FCSTD DOCUMENT  (FreeCAD 0.19R)
Label: frame
License: All rights reserved
LicenseURL: http://en.wikipedia.org/wiki/All_rights_reserved
objects: Part::Cylinder×360, Part::MultiFuse×254, Part::Box×222, Part::Cut×205, Part::Feature×133, Part::Chamfer×65, Part::Fillet×41, Part::Extrusion×23, Part::Cone×16, Part::Mirroring×12, App::DocumentObjectGroup×8, Part::RegularPolygon×4, Mesh::Feature×1, Part::Compound×1
note: 1336 computed .brp shape members not serialized (recipe doc carries the construction recipe); baked Part::Feature solids carry a one-line shape summary decoded from their .brp

FEATURE [Part::Box] Box  label="Cube"
  AttacherType = Attacher::AttachEngine3D
  Height = 1
  Length = 430
  Placement = pos=(65,-96,36) rot=(0,0,1;0rad)
  Width = 176
FEATURE [Part::Box] Box001  label="FLOOR"
  AttacherType = Attacher::AttachEngine3D
  Height = 2
  Length = 1568
  Placement = pos=(-800,-101,-32) rot=(0,0,1;0rad)
  Width = 186
FEATURE [Mesh::Feature] truck  label="TRUCK"
  Placement = pos=(-684,-93,62) rot=(0,0,1;0rad)
FEATURE [Part::Box] Box002  label="Cube002"
  AttacherType = Attacher::AttachEngine3D
  Height = 10
  Length = 430
  Placement = pos=(65,-5,25) rot=(0,0,1;0rad)
  Width = 10
FEATURE [Part::Box] Box003  label="Cube003"
  AttacherType = Attacher::AttachEngine3D
  Height = 10
  Length = 430
  Placement = pos=(65,-65,25) rot=(0,0,1;0rad)
  Width = 10
FEATURE [Part::MultiFuse] Fusion  label="Fusion-006"
  Placement = pos=(0,22,0) rot=(0,0,1;0rad)
  Refine = true
  Shapes = -> [Box003,Box002]
FEATURE [Part::Box] Box006  label="Cube006"
  AttacherType = Attacher::AttachEngine3D
  Height = 1
  Length = 55
  Placement = pos=(495,-96,36) rot=(0,1,0;0.314159rad)
  Width = 176
FEATURE [Part::Feature] Fusion001005002004004005002010002003003003001  label="axle_001"
  shape: bbox 59.64 x 183 x 59.64 mm, 5134 faces, 2 solids (baked)
FEATURE [Part::Feature] Fusion001005002004004005002010002003003003002  label="axle_002"
  Placement = pos=(274,0,0) rot=(0,0,1;0rad)
  shape: bbox 59.64 x 183 x 59.64 mm, 5134 faces, 2 solids (baked)
FEATURE [Part::Feature] Fusion001005002004004005002010002003003003003  label="axle_003"
  Placement = pos=(360,0,0) rot=(0,0,1;0rad)
  shape: bbox 59.64 x 183 x 59.64 mm, 5134 faces, 2 solids (baked)
FEATURE [Part::Feature] Fusion001005002004004005002010002003003003004  label="axle_004"
  Placement = pos=(446,0,0) rot=(0,0,1;0rad)
  shape: bbox 59.64 x 183 x 59.64 mm, 5134 faces, 2 solids (baked)
FEATURE [Part::MultiFuse] Fusion001005002004004005002010002003003003005  label="flat"
  Refine = true
  Shapes = -> [Box006,Box]
FEATURE [Part::Cylinder] Cylinder661  label="Cylinder736"
  Angle = 360
  AttacherType = Attacher::AttachEngine3D
  Height = 128
  Placement = pos=(0,-72,-1) rot=(-1,0,0;1.5708rad)
  Radius = 6
FEATURE [Part::Cylinder] Cylinder663  label="Cylinder738"
  Angle = 360
  AttacherType = Attacher::AttachEngine3D
  Height = 166
  Placement = pos=(0,-91,-1) rot=(-1,0,0;1.5708rad)
  Radius = 2.7
FEATURE [Part::Cylinder] Cylinder666  label="Cylinder741"
  Angle = 360
  AttacherType = Attacher::AttachEngine3D
  Height = 12
  Placement = pos=(4,-50,-7) rot=(0,0,1;0rad)
  Radius = 0.75
FEATURE [Part::Cylinder] Cylinder667  label="Cylinder742"
  Angle = 360
  AttacherType = Attacher::AttachEngine3D
  Height = 12
  Placement = pos=(-4,-50,-7) rot=(0,0,1;0rad)
  Radius = 0.75
FEATURE [Part::MultiFuse] Fusion001005002004004005002010002003003003017005  label="Fusion-019"
  Placement = pos=(0,-15,0) rot=(0,0,1;0rad)
  Refine = true
  Shapes = -> [Cylinder666,Cylinder667]
FEATURE [Part::Cylinder] Cylinder668  label="Cylinder743"
  Angle = 360
  AttacherType = Attacher::AttachEngine3D
  Height = 6
  Placement = pos=(4,-50,-7) rot=(0,0,1;0rad)
  Radius = 1.1
FEATURE [Part::Cylinder] Cylinder669  label="Cylinder744"
  Angle = 360
  AttacherType = Attacher::AttachEngine3D
  Height = 6
  Placement = pos=(-4,-50,-7) rot=(0,0,1;0rad)
  Radius = 1.1
FEATURE [Part::MultiFuse] Fusion001005002004004005002010002003003003017006  label="Fusion-020"
  Placement = pos=(0,-15,0) rot=(0,0,1;0rad)
  Refine = true
  Shapes = -> [Cylinder668,Cylinder669]
FEATURE [Part::Box] Box015  label="Cube015"
  AttacherType = Attacher::AttachEngine3D
  Height = 12
  Length = 12
  Placement = pos=(-6,47,-7) rot=(0,0,1;0rad)
  Width = 4
FEATURE [Part::Box] Box016  label="Cube016"
  AttacherType = Attacher::AttachEngine3D
  Height = 12
  Length = 12
  Placement = pos=(-6,-10,-7) rot=(0,0,1;0rad)
  Width = 4
FEATURE [Part::Box] Box018  label="Cube018"
  AttacherType = Attacher::AttachEngine3D
  Height = 12
  Length = 12
  Placement = pos=(-6,-67,-7) rot=(0,0,1;0rad)
  Width = 4
FEATURE [Part::MultiFuse] Fusion001005002004004005002010002003003003017007  label="Fusion-016"
  Refine = true
  Shapes = -> [Fusion001005002004004005002010002003003003017005,Fusion001005002004004005002010002003003003017006]
FEATURE [Part::Feature] Fusion001005002004004005002010002003003003017007001  label="Fusion-018"
  Placement = pos=(0,57,0) rot=(0,0,1;0rad)
  shape: bbox 10.2 x 2.2 x 12 mm, 10 faces, 2 solids (baked)
FEATURE [Part::Feature] Fusion001005002004004005002010002003003003017007002  label="Fusion-017"
  Placement = pos=(0,114,0) rot=(0,0,1;0rad)
  shape: bbox 10.2 x 2.2 x 12 mm, 10 faces, 2 solids (baked)
FEATURE [Part::Cylinder] Cylinder670  label="Cylinder745"
  Angle = 360
  AttacherType = Attacher::AttachEngine3D
  Height = 12
  Placement = pos=(4,-50,-7) rot=(0,0,1;0rad)
  Radius = 0.75
FEATURE [Part::Cylinder] Cylinder671  label="Cylinder746"
  Angle = 360
  AttacherType = Attacher::AttachEngine3D
  Height = 6
  Placement = pos=(4,-50,-1) rot=(0,0,1;0rad)
  Radius = 1.1
FEATURE [Part::MultiFuse] Fusion001005002004004005002010002003003003017007003  label="Fusion-003"
  Placement = pos=(-4,42,0) rot=(0,0,1;0rad)
  Refine = true
  Shapes = -> [Cylinder670,Cylinder671]
FEATURE [Part::MultiFuse] Fusion001005002004004005002010002003003003017007005  label="Fusion-015"
  Refine = true
  Shapes = -> [Fusion001005002004004005002010002003003003017007,Fusion001005002004004005002010002003003003017007002,Fusion001005002004004005002010002003003003017007001]
FEATURE [Part::Box] Box019  label="Cube019"
  AttacherType = Attacher::AttachEngine3D
  Height = 7
  Length = 16
  Placement = pos=(-8,-72,-8) rot=(0,0,1;0rad)
  Width = 128
FEATURE [Part::Box] Box020  label="Cube020"
  AttacherType = Attacher::AttachEngine3D
  Height = 6
  Length = 16
  Placement = pos=(-8,-72,-1) rot=(0,0,1;0rad)
  Width = 128
FEATURE [Part::Cylinder] Cylinder672  label="Cylinder747"
  Angle = 360
  AttacherType = Attacher::AttachEngine3D
  Height = 8
  Placement = pos=(0,-8,28) rot=(0,0,1;0rad)
  Radius = 35
FEATURE [Part::Box] Box024  label="Cube024"
  AttacherType = Attacher::AttachEngine3D
  Height = 10
  Length = 50
  Placement = pos=(65,-46,25) rot=(0,0,1;0rad)
  Width = 25
FEATURE [Part::Feature] Face001
  shape: bbox 59.35 x 2e-07 x 37.17 mm, 1 faces, 0 solids (baked)
FEATURE [Part::Extrusion] Extrude
  Base = -> Face001
  Dir = (0,1,0)
  DirMode = 0
  FaceMakerClass = Part::FaceMakerBullseye
  LengthFwd = 35
  LengthRev = 0
  Placement = pos=(0,-10,0) rot=(0,0,1;0rad)
  Solid = true
  Symmetric = false
FEATURE [Part::MultiFuse] Fusion001005002004004005002010002003003003017007007  label="Fusion-001"
  Placement = pos=(0,13,0) rot=(0,0,1;0rad)
  Refine = true
  Shapes = -> [Box024,Extrude]
FEATURE [Part::Box] Box025  label="Cube025"
  AttacherType = Attacher::AttachEngine3D
  Height = 15
  Length = 430
  Placement = pos=(65,-101,22) rot=(0,0,1;0rad)
  Width = 5
FEATURE [Part::Cylinder] Cylinder673  label="Cylinder748"
  Angle = 360
  AttacherType = Attacher::AttachEngine3D
  Height = 5
  Placement = pos=(280,-101,1) rot=(-1,0,0;1.5708rad)
  Radius = 34
FEATURE [Part::Cylinder] Cylinder674  label="Cylinder749"
  Angle = 360
  AttacherType = Attacher::AttachEngine3D
  Height = 5
  Placement = pos=(365,-101,1) rot=(-1,0,0;1.5708rad)
  Radius = 34
FEATURE [Part::Cylinder] Cylinder675  label="Cylinder750"
  Angle = 360
  AttacherType = Attacher::AttachEngine3D
  Height = 5
  Placement = pos=(451,-101,1) rot=(-1,0,0;1.5708rad)
  Radius = 34
FEATURE [Part::MultiFuse] Fusion001005002004004005002010002003003003017007008  label="Fusion-000"
  Placement = pos=(-5,0,0) rot=(0,0,1;0rad)
  Refine = true
  Shapes = -> [Cylinder675,Cylinder674,Cylinder673]
FEATURE [Part::Cut] Cut012004
  Base = -> Box025
  Refine = true
  Tool = -> Fusion001005002004004005002010002003003003017007008
FEATURE [Part::Cylinder] Cylinder676  label="Cylinder751"
  Angle = 360
  AttacherType = Attacher::AttachEngine3D
  Height = 1
  Placement = pos=(365,-101,1) rot=(-1,0,0;1.5708rad)
  Radius = 35
FEATURE [Part::Cylinder] Cylinder677  label="Cylinder752"
  Angle = 360
  AttacherType = Attacher::AttachEngine3D
  Height = 1
  Placement = pos=(280,-101,1) rot=(-1,0,0;1.5708rad)
  Radius = 35
FEATURE [Part::Cylinder] Cylinder678  label="Cylinder753"
  Angle = 360
  AttacherType = Attacher::AttachEngine3D
  Height = 1
  Placement = pos=(451,-101,1) rot=(-1,0,0;1.5708rad)
  Radius = 35
FEATURE [Part::MultiFuse] Fusion001005002004004005002010002003003003017007009  label="Fusion-007"
  Placement = pos=(-5,0,0) rot=(0,0,1;0rad)
  Refine = true
  Shapes = -> [Cylinder678,Cylinder676,Cylinder677]
FEATURE [Part::Box] Box026  label="Cube026"
  AttacherType = Attacher::AttachEngine3D
  Height = 13
  Length = 430
  Placement = pos=(65,-101,23) rot=(0,0,1;0rad)
  Width = 1
FEATURE [Part::Cut] Cut012005
  Base = -> Box026
  Refine = true
  Tool = -> Fusion001005002004004005002010002003003003017007009
FEATURE [Part::Cut] Cut012006
  Base = -> Cut012004
  Refine = true
  Tool = -> Cut012005
FEATURE [Part::Feature] Face002
  shape: bbox 80.83 x 2e-07 x 47.48 mm, 1 faces, 0 solids (baked)
FEATURE [Part::Feature] Face003
  shape: bbox 84.57 x 2e-07 x 55.62 mm, 1 faces, 0 solids (baked)
FEATURE [Part::Extrusion] Extrude002
  Base = -> Face002
  Dir = (0,1,0)
  DirMode = 0
  FaceMakerClass = Part::FaceMakerBullseye
  LengthFwd = 1
  LengthRev = 0
  Solid = true
  Symmetric = false
FEATURE [Part::Extrusion] Extrude003
  Base = -> Face003
  Dir = (0,1,0)
  DirMode = 0
  FaceMakerClass = Part::FaceMakerBullseye
  LengthFwd = 5
  LengthRev = 0
  Solid = true
  Symmetric = false
FEATURE [Part::Cut] Cut012012
  Base = -> Extrude003
  Refine = true
  Tool = -> Extrude002
FEATURE [Part::Box] Box027  label="Cube027"
  AttacherType = Attacher::AttachEngine3D
  Height = 15
  Length = 49.5
  Placement = pos=(-35,-66,37) rot=(0,0,-1;0.785398rad)
  Width = 5
FEATURE [Part::Box] Box028  label="Cube028"
  AttacherType = Attacher::AttachEngine3D
  Height = 15
  Length = 49.5
  Placement = pos=(-35,-66,37) rot=(0,0,-1;0.785398rad)
  Width = 5
FEATURE [Part::Mirroring] Part__Mirroring  label="Cube028 (Mirror #1)"
  Base = (0,0,0)
  Normal = (0,1,0)
  Placement = pos=(0,-16,0) rot=(0,0,1;0rad)
  Source = -> Box028
FEATURE [Part::Box] Box029  label="Cube029"
  AttacherType = Attacher::AttachEngine3D
  Height = 15
  Length = 5
  Placement = pos=(-35,-66,37) rot=(0,0,-1;0rad)
  Width = 116
FEATURE [Part::MultiFuse] Fusion001005002004004005002010002003003003017007010  label="Fusion-008"
  Placement = pos=(-5,0,0) rot=(0,0,1;0rad)
  Refine = true
  Shapes = -> [Box027,Part__Mirroring,Box029]
FEATURE [Part::Box] Box030  label="Cube030"
  AttacherType = Attacher::AttachEngine3D
  Height = 13
  Length = 49.5
  Placement = pos=(-35,-102,38) rot=(0,0,-1;0rad)
  Width = 2
FEATURE [Part::Box] Box031  label="Cube031"
  AttacherType = Attacher::AttachEngine3D
  Height = 13
  Length = 49.5
  Placement = pos=(-35,84,38) rot=(0,0,-1;0rad)
  Width = 1
FEATURE [Part::Cylinder] Cylinder679  label="Cylinder754"
  Angle = 46
  AttacherType = Attacher::AttachEngine3D
  Height = 7
  Placement = pos=(0,0,0) rot=(0,0,-1;1.97222rad)
  Radius = 109
FEATURE [Part::Cylinder] Cylinder680  label="Cylinder755"
  Angle = 32
  AttacherType = Attacher::AttachEngine3D
  Height = 7
  Placement = pos=(0,0,0) rot=(0,0,-1;1.85005rad)
  Radius = 109
FEATURE [Part::Cylinder] Cylinder681  label="Cylinder756"
  Angle = 41
  AttacherType = Attacher::AttachEngine3D
  Height = 7
  Placement = pos=(0,0,0) rot=(0,0,-1;1.90241rad)
  Radius = 108
FEATURE [Part::Cylinder] Cylinder682  label="Cylinder757"
  Angle = 26
  AttacherType = Attacher::AttachEngine3D
  Height = 7
  Placement = pos=(0,0,0) rot=(0,0,-1;1.79769rad)
  Radius = 110
FEATURE [Part::Cylinder] Cylinder686
  Angle = 360
  AttacherType = Attacher::AttachEngine3D
  Height = 7
  Placement = pos=(-34.1,-43,15.25) rot=(-1,0,0;1.5708rad)
  Radius = 3.5
FEATURE [Part::Box] Box035  label="Cube035"
  AttacherType = Attacher::AttachEngine3D
  Height = 4.3
  Length = 14
  Placement = pos=(-7,-43,-9) rot=(0,0,1;0rad)
  Width = 7
FEATURE [Part::Cylinder] Cylinder691  label="Cylinder762"
  Angle = 360
  AttacherType = Attacher::AttachEngine3D
  Height = 14
  Placement = pos=(-4.5,-50.5,-7) rot=(0,0,1;0rad)
  Radius = 1.25
FEATURE [Part::Cylinder] Cylinder692  label="Cylinder763"
  Angle = 360
  AttacherType = Attacher::AttachEngine3D
  Height = 14
  Placement = pos=(4.5,-50.5,-7) rot=(0,0,1;0rad)
  Radius = 1.25
FEATURE [Part::MultiFuse] Fusion001005002004004005002010002003003003017007017  label="Fusion-011"
  Placement = pos=(0,4,-3) rot=(0,0,1;0rad)
  Refine = true
  Shapes = -> [Cylinder692,Cylinder691]
FEATURE [Part::Cylinder] Cylinder693  label="Cylinder764"
  Angle = 46
  AttacherType = Attacher::AttachEngine3D
  Height = 7
  Placement = pos=(0,0,0) rot=(0,0,-1;1.97222rad)
  Radius = 108
FEATURE [Part::Cylinder] Cylinder694  label="Cylinder765"
  Angle = 46
  AttacherType = Attacher::AttachEngine3D
  Height = 7
  Placement = pos=(0,0,0) rot=(0,0,-1;1.97222rad)
  Radius = 107
FEATURE [Part::Cut] Cut012021
  Base = -> Cylinder682
  Placement = pos=(0,-1,0) rot=(0,0,1;0rad)
  Refine = true
  Tool = -> Cylinder679
FEATURE [Part::Cut] Cut012022
  Base = -> Cylinder680
  Placement = pos=(0,-0.5,0) rot=(0,0,1;0rad)
  Refine = true
  Tool = -> Cylinder693
FEATURE [Part::Cut] Cut012023
  Base = -> Cylinder681
  Refine = true
  Tool = -> Cylinder694
FEATURE [Part::MultiFuse] Fusion001005002004004005002010002003003003017007018  label="Fusion-012"
  Placement = pos=(0,-36,114) rot=(1,0,0;1.5708rad)
  Refine = true
  Shapes = -> [Cut012021,Cut012022,Cut012023]
FEATURE [Part::Cylinder] Cylinder695
  Angle = 360
  AttacherType = Attacher::AttachEngine3D
  Height = 7
  Placement = pos=(-34.1,-43,15.25) rot=(-1,0,0;1.5708rad)
  Radius = 1.5
FEATURE [Part::MultiFuse] Fusion001005002004004005002010002003003003017007019  label="Fusion-013"
  Refine = true
  Shapes = -> [Fusion001005002004004005002010002003003003017007018,Cylinder686]
FEATURE [Part::Cut] Cut012024
  Base = -> Fusion001005002004004005002010002003003003017007019
  Refine = true
  Tool = -> Cylinder695
FEATURE [Part::Fillet] Fillet001003
  Base = -> Cut012024
  Edges = 1 edges r=4: [Edge6]
  Placement = pos=(0,0,-12) rot=(0,0,1;0rad)
FEATURE [Part::MultiFuse] Fusion001005002004004005002010002003003003017007020  label="Fusion-014"
  Refine = true
  Shapes = -> [Box035,Fillet001003]
FEATURE [Part::Box] Box037  label="Cube037"
  AttacherType = Attacher::AttachEngine3D
  Height = 4.3
  Length = 15
  Placement = pos=(-7.5,-43.25,-9) rot=(0,0,1;0rad)
  Width = 7.5
FEATURE [Part::Box] Box038  label="Cube038"
  AttacherType = Attacher::AttachEngine3D
  Height = 1
  Length = 8.5
  Placement = pos=(-4.25,-43,-9) rot=(0,0,1;0rad)
  Width = 7
FEATURE [Part::Box] Box039  label="Cube039"
  AttacherType = Attacher::AttachEngine3D
  Height = 2
  Length = 2
  Placement = pos=(-6.25,-43,-10) rot=(0,0,1;0rad)
  Width = 7
FEATURE [Part::Box] Box040  label="Cube040"
  AttacherType = Attacher::AttachEngine3D
  Height = 2
  Length = 15
  Placement = pos=(-7.5,-49.5,-11) rot=(0,0,1;0rad)
  Width = 20
FEATURE [Part::Box] Box041  label="Cube041"
  AttacherType = Attacher::AttachEngine3D
  Height = 2
  Length = 15
  Placement = pos=(-7.5,-43.25,-11) rot=(0,0,1;0rad)
  Width = 7.5
FEATURE [Part::Cut] Cut012027
  Base = -> Box040
  Refine = true
  Tool = -> Box041
FEATURE [Part::Box] Box042  label="Cube042"
  AttacherType = Attacher::AttachEngine3D
  Height = 2
  Length = 8
  Placement = pos=(-4,-44,-11) rot=(0,0,1;0rad)
  Width = 9
FEATURE [Part::Fillet] Fillet001006
  Base = -> Cut012027
  Edges = 8 edges r=3: [Edge2,Edge4,Edge9,Edge12,Edge14,Edge16,Edge21,Edge24]
FEATURE [Part::MultiFuse] Fusion001005002004004005002010002003003003017007022  label="Fusion-022"
  Placement = pos=(0,0,1) rot=(0,0,1;0rad)
  Refine = true
  Shapes = -> [Box042,Fillet001006]
FEATURE [Part::Fillet] Fillet001007
  Base = -> Fusion001005002004004005002010002003003003017007020
  Edges = 10 edges r=1: [Edge5,Edge7,Edge20,Edge21,Edge32,Edge33,Edge73,Edge74,Edge84,Edge85]
FEATURE [Part::Cut] Cut012028
  Base = -> Fillet001007
  Refine = true
  Tool = -> Box038
FEATURE [Part::Box] Box043  label="Cube043"
  AttacherType = Attacher::AttachEngine3D
  Height = 2
  Length = 2
  Placement = pos=(4.25,-43,-10) rot=(0,0,1;0rad)
  Width = 7
FEATURE [Part::MultiFuse] Fusion001005002004004005002010002003003003017007023  label="Fusion-023"
  Refine = true
  Shapes = -> [Box039,Box043]
FEATURE [Part::Chamfer] Chamfer003
  Base = -> Fusion001005002004004005002010002003003003017007023
  Edges = 2 edges r=1: [Edge4,Edge20]
FEATURE [Part::MultiFuse] Fusion001005002004004005002010002003003003017007024  label="axle-leafspring-left_"
  Refine = true
  Shapes = -> [Cut012028,Chamfer003]
FEATURE [Part::Cylinder] Cylinder696  label="Cylinder766"
  Angle = 360
  AttacherType = Attacher::AttachEngine3D
  Height = 14
  Placement = pos=(-4.5,-50.5,-7) rot=(0,0,1;0rad)
  Radius = 1.25
FEATURE [Part::Cylinder] Cylinder697  label="Cylinder767"
  Angle = 360
  AttacherType = Attacher::AttachEngine3D
  Height = 14
  Placement = pos=(4.5,-50.5,-7) rot=(0,0,1;0rad)
  Radius = 1.25
FEATURE [Part::MultiFuse] Fusion001005002004004005002010002003003003017007024004  label="Fusion-028"
  Placement = pos=(0,18,-3) rot=(0,0,1;0rad)
  Refine = true
  Shapes = -> [Cylinder697,Cylinder696]
FEATURE [Part::Cylinder] Cylinder698  label="Cylinder768"
  Angle = 360
  AttacherType = Attacher::AttachEngine3D
  Height = 13
  Placement = pos=(-4.5,-50.5,-7) rot=(0,0,1;0rad)
  Radius = 3
FEATURE [Part::Cylinder] Cylinder699  label="Cylinder769"
  Angle = 360
  AttacherType = Attacher::AttachEngine3D
  Height = 13
  Placement = pos=(4.5,-50.5,-7) rot=(0,0,1;0rad)
  Radius = 3
FEATURE [Part::MultiFuse] Fusion001005002004004005002010002003003003017007024005  label="Fusion-029"
  Placement = pos=(0,4,-1) rot=(0,0,1;0rad)
  Refine = true
  Shapes = -> [Cylinder699,Cylinder698]
FEATURE [Part::Cylinder] Cylinder700  label="Cylinder770"
  Angle = 360
  AttacherType = Attacher::AttachEngine3D
  Height = 13
  Placement = pos=(4.5,-50.5,-7) rot=(0,0,1;0rad)
  Radius = 3
FEATURE [Part::Cylinder] Cylinder701  label="Cylinder771"
  Angle = 360
  AttacherType = Attacher::AttachEngine3D
  Height = 13
  Placement = pos=(-4.5,-50.5,-7) rot=(0,0,1;0rad)
  Radius = 3
FEATURE [Part::MultiFuse] Fusion001005002004004005002010002003003003017007024006  label="Fusion-030"
  Placement = pos=(0,18,-1) rot=(0,0,1;0rad)
  Refine = true
  Shapes = -> [Cylinder700,Cylinder701]
FEATURE [Part::MultiFuse] Fusion001005002004004005002010002003003003017007024007  label="Fusion-031"
  Refine = true
  Shapes = -> [Fusion001005002004004005002010002003003003017007024005,Fusion001005002004004005002010002003003003017007024006]
FEATURE [Part::MultiFuse] Fusion001005002004004005002010002003003003017007024008  label="Fusion-032"
  Refine = true
  Shapes = -> [Fusion001005002004004005002010002003003003017007024004,Fusion001005002004004005002010002003003003017007017]
FEATURE [Part::Cylinder] Cylinder702  label="Cylinder772"
  Angle = 360
  AttacherType = Attacher::AttachEngine3D
  Height = 14
  Placement = pos=(-4.5,-50.5,-7) rot=(0,0,1;0rad)
  Radius = 1.5
FEATURE [Part::Cylinder] Cylinder703  label="Cylinder773"
  Angle = 360
  AttacherType = Attacher::AttachEngine3D
  Height = 14
  Placement = pos=(4.5,-50.5,-7) rot=(0,0,1;0rad)
  Radius = 1.5
FEATURE [Part::MultiFuse] Fusion001005002004004005002010002003003003017007024009  label="Fusion-033"
  Placement = pos=(0,4,-3) rot=(0,0,1;0rad)
  Refine = true
  Shapes = -> [Cylinder703,Cylinder702]
FEATURE [Part::Cylinder] Cylinder704  label="Cylinder774"
  Angle = 360
  AttacherType = Attacher::AttachEngine3D
  Height = 14
  Placement = pos=(4.5,-50.5,-7) rot=(0,0,1;0rad)
  Radius = 1.5
FEATURE [Part::Cylinder] Cylinder705  label="Cylinder775"
  Angle = 360
  AttacherType = Attacher::AttachEngine3D
  Height = 14
  Placement = pos=(-4.5,-50.5,-7) rot=(0,0,1;0rad)
  Radius = 1.5
FEATURE [Part::MultiFuse] Fusion001005002004004005002010002003003003017007024011  label="Fusion-035"
  Placement = pos=(0,18,-3) rot=(0,0,1;0rad)
  Refine = true
  Shapes = -> [Cylinder704,Cylinder705]
FEATURE [Part::MultiFuse] Fusion001005002004004005002010002003003003017007024010  label="Fusion-034"
  Refine = true
  Shapes = -> [Fusion001005002004004005002010002003003003017007024011,Fusion001005002004004005002010002003003003017007024009]
FEATURE [Part::Cut] Cut012029  label="axle-leafspring-lock-left"
  Base = -> Fusion001005002004004005002010002003003003017007022
  Refine = true
  Tool = -> Fusion001005002004004005002010002003003003017007024010
FEATURE [Part::Cylinder] Cylinder706  label="Cylinder776"
  Angle = 360
  AttacherType = Attacher::AttachEngine3D
  Height = 13
  Placement = pos=(-4.5,-50.5,-7) rot=(0,0,1;0rad)
  Radius = 3
FEATURE [Part::Cylinder] Cylinder707  label="Cylinder777"
  Angle = 360
  AttacherType = Attacher::AttachEngine3D
  Height = 13
  Placement = pos=(4.5,-50.5,-7) rot=(0,0,1;0rad)
  Radius = 3
FEATURE [Part::MultiFuse] Fusion001005002004004005002010002003003003017007024014  label="Fusion-038"
  Placement = pos=(0,4,-1) rot=(0,0,1;0rad)
  Refine = true
  Shapes = -> [Cylinder707,Cylinder706]
FEATURE [Part::Cylinder] Cylinder708  label="Cylinder778"
  Angle = 360
  AttacherType = Attacher::AttachEngine3D
  Height = 13
  Placement = pos=(-4.5,-50.5,-7) rot=(0,0,1;0rad)
  Radius = 3
FEATURE [Part::Cylinder] Cylinder709  label="Cylinder779"
  Angle = 360
  AttacherType = Attacher::AttachEngine3D
  Height = 13
  Placement = pos=(4.5,-50.5,-7) rot=(0,0,1;0rad)
  Radius = 3
FEATURE [Part::MultiFuse] Fusion001005002004004005002010002003003003017007024013  label="Fusion-037"
  Placement = pos=(0,18,-1) rot=(0,0,1;0rad)
  Refine = true
  Shapes = -> [Cylinder709,Cylinder708]
FEATURE [Part::MultiFuse] Fusion001005002004004005002010002003003003017007024015  label="Fusion-039"
  Placement = pos=(0,63,0) rot=(0,0,1;0rad)
  Refine = true
  Shapes = -> [Fusion001005002004004005002010002003003003017007024014,Fusion001005002004004005002010002003003003017007024013]
FEATURE [Part::Box] Box044  label="Cube044"
  AttacherType = Attacher::AttachEngine3D
  Height = 2
  Length = 15
  Placement = pos=(-7.5,-49.5,-11) rot=(0,0,1;0rad)
  Width = 20
FEATURE [Part::Box] Box045  label="Cube045"
  AttacherType = Attacher::AttachEngine3D
  Height = 2
  Length = 15
  Placement = pos=(-7.5,-43.25,-11) rot=(0,0,1;0rad)
  Width = 7.5
FEATURE [Part::Cut] Cut012030
  Base = -> Box044
  Refine = true
  Tool = -> Box045
FEATURE [Part::Fillet] Fillet001008
  Base = -> Cut012030
  Edges = 8 edges r=3: [Edge2,Edge4,Edge9,Edge12,Edge14,Edge16,Edge21,Edge24]
FEATURE [Part::Box] Box046  label="Cube046"
  AttacherType = Attacher::AttachEngine3D
  Height = 2
  Length = 8
  Placement = pos=(-4,-44,-11) rot=(0,0,1;0rad)
  Width = 9
FEATURE [Part::MultiFuse] Fusion001005002004004005002010002003003003017007024016  label="Fusion-040"
  Placement = pos=(0,0,1) rot=(0,0,1;0rad)
  Refine = true
  Shapes = -> [Box046,Fillet001008]
FEATURE [Part::Cylinder] Cylinder710  label="Cylinder780"
  Angle = 360
  AttacherType = Attacher::AttachEngine3D
  Height = 14
  Placement = pos=(4.5,-50.5,-7) rot=(0,0,1;0rad)
  Radius = 1.5
FEATURE [Part::Cylinder] Cylinder711  label="Cylinder781"
  Angle = 360
  AttacherType = Attacher::AttachEngine3D
  Height = 14
  Placement = pos=(-4.5,-50.5,-7) rot=(0,0,1;0rad)
  Radius = 1.5
FEATURE [Part::Cylinder] Cylinder712  label="Cylinder782"
  Angle = 360
  AttacherType = Attacher::AttachEngine3D
  Height = 14
  Placement = pos=(4.5,-50.5,-7) rot=(0,0,1;0rad)
  Radius = 1.5
FEATURE [Part::MultiFuse] Fusion001005002004004005002010002003003003017007024018  label="Fusion-042"
  Placement = pos=(0,18,-3) rot=(0,0,1;0rad)
  Refine = true
  Shapes = -> [Cylinder712,Cylinder711]
FEATURE [Part::Cylinder] Cylinder713  label="Cylinder783"
  Angle = 360
  AttacherType = Attacher::AttachEngine3D
  Height = 14
  Placement = pos=(-4.5,-50.5,-7) rot=(0,0,1;0rad)
  Radius = 1.5
FEATURE [Part::MultiFuse] Fusion001005002004004005002010002003003003017007024017  label="Fusion-041"
  Placement = pos=(0,4,-3) rot=(0,0,1;0rad)
  Refine = true
  Shapes = -> [Cylinder710,Cylinder713]
FEATURE [Part::MultiFuse] Fusion001005002004004005002010002003003003017007024019  label="Fusion-043"
  Refine = true
  Shapes = -> [Fusion001005002004004005002010002003003003017007024018,Fusion001005002004004005002010002003003003017007024017]
FEATURE [Part::Cut] Cut012031  label="axle-leafspring-lock-right"
  Base = -> Fusion001005002004004005002010002003003003017007024016
  Placement = pos=(0,63,0) rot=(0,0,1;0rad)
  Refine = true
  Tool = -> Fusion001005002004004005002010002003003003017007024019
FEATURE [Part::Cylinder] Cylinder714  label="Cylinder784"
  Angle = 360
  AttacherType = Attacher::AttachEngine3D
  Height = 14
  Placement = pos=(-4.5,-50.5,-7) rot=(0,0,1;0rad)
  Radius = 1.25
FEATURE [Part::Cylinder] Cylinder715  label="Cylinder785"
  Angle = 360
  AttacherType = Attacher::AttachEngine3D
  Height = 14
  Placement = pos=(4.5,-50.5,-7) rot=(0,0,1;0rad)
  Radius = 1.25
FEATURE [Part::MultiFuse] Fusion001005002004004005002010002003003003017007024020  label="Fusion-044"
  Placement = pos=(0,4,-3) rot=(0,0,1;0rad)
  Refine = true
  Shapes = -> [Cylinder715,Cylinder714]
FEATURE [Part::Cylinder] Cylinder716  label="Cylinder786"
  Angle = 360
  AttacherType = Attacher::AttachEngine3D
  Height = 14
  Placement = pos=(4.5,-50.5,-7) rot=(0,0,1;0rad)
  Radius = 1.25
FEATURE [Part::Cylinder] Cylinder717  label="Cylinder787"
  Angle = 360
  AttacherType = Attacher::AttachEngine3D
  Height = 14
  Placement = pos=(-4.5,-50.5,-7) rot=(0,0,1;0rad)
  Radius = 1.25
FEATURE [Part::MultiFuse] Fusion001005002004004005002010002003003003017007024022  label="Fusion-046"
  Placement = pos=(0,18,-3) rot=(0,0,1;0rad)
  Refine = true
  Shapes = -> [Cylinder716,Cylinder717]
FEATURE [Part::MultiFuse] Fusion001005002004004005002010002003003003017007024021  label="Fusion-045"
  Placement = pos=(0,63,0) rot=(0,0,1;0rad)
  Refine = true
  Shapes = -> [Fusion001005002004004005002010002003003003017007024022,Fusion001005002004004005002010002003003003017007024020]
FEATURE [Part::MultiFuse] Fusion001005002004004005002010002003003003017007024023  label="Fusion-047"
  Placement = pos=(0,0,0.5) rot=(0,0,1;0rad)
  Refine = true
  Shapes = -> [Fusion001005002004004005002010002003003003017007024008,Fusion001005002004004005002010002003003003017007024021]
FEATURE [Part::Box] Box047  label="Cube047"
  AttacherType = Attacher::AttachEngine3D
  Height = 4.3
  Length = 15
  Placement = pos=(-7.5,19.75,-9) rot=(0,0,1;0rad)
  Width = 7.5
FEATURE [Part::MultiFuse] Fusion001005002004004005002010002003003003017007024024  label="Fusion-048"
  Refine = true
  Shapes = -> [Box047,Box037]
FEATURE [Part::Cut] Cut012032
  Base = -> Cylinder661
  Refine = true
  Tool = -> Fusion001005002004004005002010002003003003017007024024
FEATURE [Part::MultiFuse] Fusion001005002004004005002010002003003003017007024025  label="Fusion-049"
  Refine = true
  Shapes = -> [Fusion001005002004004005002010002003003003017007024007,Fusion001005002004004005002010002003003003017007024015,Cut012032]
FEATURE [Part::Cut] Cut012033
  Base = -> Fusion001005002004004005002010002003003003017007024025
  Refine = true
  Tool = -> Fusion001005002004004005002010002003003003017007024023
FEATURE [Part::MultiFuse] Fusion001005002004004005002010002003003003017007024026  label="Fusion-050"
  Refine = true
  Shapes = -> [Cut012033,Box018,Box016,Box015]
FEATURE [Part::MultiFuse] Fusion001005002004004005002010002003003003017007024027  label="Fusion-051"
  Refine = true
  Shapes = -> [Fusion001005002004004005002010002003003003017007005,Fusion001005002004004005002010002003003003017007003]
FEATURE [Part::Cut] Cut012034
  Base = -> Fusion001005002004004005002010002003003003017007024026
  Refine = true
  Tool = -> Fusion001005002004004005002010002003003003017007024027
FEATURE [Part::Cut] Cut012035
  Base = -> Cut012034
  Refine = true
  Tool = -> Cylinder663
FEATURE [Part::Box] Box048  label="Cube048"
  AttacherType = Attacher::AttachEngine3D
  Height = 14
  Length = 10
  Placement = pos=(-39,-46,0) rot=(0,0,1;0rad)
  Width = 13
FEATURE [Part::Box] Box049  label="Cube049"
  AttacherType = Attacher::AttachEngine3D
  Height = 7
  Length = 15
  Placement = pos=(-39,-46,7) rot=(0,0,1;0rad)
  Width = 13
FEATURE [Part::Box] Box050  label="Cube050"
  AttacherType = Attacher::AttachEngine3D
  Height = 14
  Length = 15
  Placement = pos=(-39,-36,0) rot=(0,0,1;0rad)
  Width = 3
FEATURE [Part::Box] Box051  label="Cube051"
  AttacherType = Attacher::AttachEngine3D
  Height = 7
  Length = 15
  Placement = pos=(-39,-43.25,0) rot=(0,0,1;0rad)
  Width = 7.5
FEATURE [Part::MultiFuse] Fusion001005002004004005002010002003003003017007024028  label="Fusion-052"
  Refine = true
  Shapes = -> [Box048,Box049,Box050]
FEATURE [Part::Cut] Cut012035004
  Base = -> Fusion001005002004004005002010002003003003017007024028
  Refine = true
  Tool = -> Box051
FEATURE [Part::Fillet] Fillet001009
  Base = -> Cut012035004
  Edges = 3 edges r=3: [Edge4,Edge13,Edge22]
FEATURE [Part::Chamfer] Chamfer004
  Base = -> Fillet001009
  Edges = 1 edges r=7: [Edge24]
FEATURE [Part::Cylinder] Cylinder718  label="Cylinder788"
  Angle = 360
  AttacherType = Attacher::AttachEngine3D
  Height = 7.5
  Placement = pos=(-34.1,0,3.25) rot=(-1,0,0;1.5708rad)
  Radius = 1.5
FEATURE [Part::Cylinder] Cylinder719  label="Cylinder789"
  Angle = 360
  AttacherType = Attacher::AttachEngine3D
  Height = 15
  Placement = pos=(-34.1,0,3.25) rot=(-1,0,0;1.5708rad)
  Radius = 1.2
FEATURE [Part::MultiFuse] Fusion001005002004004005002010002003003003017007024029  label="Fusion-053"
  Placement = pos=(0,-47,0) rot=(0,0,1;0rad)
  Refine = true
  Shapes = -> [Cylinder719,Cylinder718]
FEATURE [Part::Cut] Cut012035005
  Base = -> Chamfer004
  Refine = true
  Tool = -> Fusion001005002004004005002010002003003003017007024029
FEATURE [Part::Box] Box052  label="Cube052"
  AttacherType = Attacher::AttachEngine3D
  Height = 22
  Length = 78
  Placement = pos=(-39,-46,14) rot=(0,0,1;0rad)
  Width = 13
FEATURE [Part::Box] Box053  label="Cube053"
  AttacherType = Attacher::AttachEngine3D
  Height = 7
  Length = 14
  Placement = pos=(25,-46,7) rot=(0,0,1;0rad)
  Width = 13
FEATURE [Part::Box] Box054  label="Cube054"
  AttacherType = Attacher::AttachEngine3D
  Height = 11
  Length = 15
  Placement = pos=(25,-36,-4) rot=(0,0,1;0rad)
  Width = 3
FEATURE [Part::Box] Box055  label="Cube055"
  AttacherType = Attacher::AttachEngine3D
  Height = 18
  Length = 10
  Placement = pos=(30,-46,-4) rot=(0,0,1;0rad)
  Width = 13
FEATURE [Part::Box] Box056  label="Cube056"
  AttacherType = Attacher::AttachEngine3D
  Height = 11
  Length = 15
  Placement = pos=(25,-43.25,-4) rot=(0,0,1;0rad)
  Width = 7.5
FEATURE [Part::Cylinder] Cylinder723  label="Cylinder793"
  Angle = 360
  AttacherType = Attacher::AttachEngine3D
  Height = 13
  Placement = pos=(34,-46,-1.55) rot=(-1,0,0;1.5708rad)
  Radius = 1
FEATURE [Part::Fillet] Fillet001012
  Base = -> Cut012035005
  Edges = 1 edges r=3: [Edge13]
FEATURE [Part::Box] Box057  label="Cube057"
  AttacherType = Attacher::AttachEngine3D
  Height = 8
  Length = 50
  Placement = pos=(-25,-46,14) rot=(0,0,1;0rad)
  Width = 3
FEATURE [Part::Cut] Cut012035007
  Base = -> Box052
  Refine = true
  Tool = -> Box057
FEATURE [Part::Box] Box058  label="Cube058"
  AttacherType = Attacher::AttachEngine3D
  Height = 14
  Length = 39
  Placement = pos=(-39,-43,22) rot=(0,0,1;0rad)
  Width = 70
FEATURE [Part::Box] Box059  label="Cube059"
  AttacherType = Attacher::AttachEngine3D
  Height = 10
  Length = 10
  Placement = pos=(-49,-43,12) rot=(0,0,1;0rad)
  Width = 10
FEATURE [Part::Box] Box060  label="Cube060"
  AttacherType = Attacher::AttachEngine3D
  Height = 10
  Length = 10
  Placement = pos=(-49,-40.75,12) rot=(0,0,1;0rad)
  Width = 5.5
FEATURE [Part::Cut] Cut012035009
  Base = -> Box059
  Refine = true
  Tool = -> Box060
FEATURE [Part::Fillet] Fillet001013
  Base = -> Cut012035009
  Edges = 4 edges r=4: [Edge1,Edge3,Edge13,Edge15]
FEATURE [Part::Cylinder] Cylinder724  label="Cylinder794"
  Angle = 360
  AttacherType = Attacher::AttachEngine3D
  Height = 15
  Placement = pos=(-34.1,0,3.25) rot=(-1,0,0;1.5708rad)
  Radius = 1.2
FEATURE [Part::Cylinder] Cylinder725  label="Cylinder795"
  Angle = 360
  AttacherType = Attacher::AttachEngine3D
  Height = 7.5
  Placement = pos=(-34.1,0,3.25) rot=(-1,0,0;1.5708rad)
  Radius = 1.5
FEATURE [Part::MultiFuse] Fusion001005002004004005002010002003003003017007024035  label="Fusion-059"
  Placement = pos=(-10,-45,13.5) rot=(0,0,1;0rad)
  Refine = true
  Shapes = -> [Cylinder724,Cylinder725]
FEATURE [Part::Cut] Cut012035010
  Base = -> Fillet001013
  Placement = pos=(0,0,6) rot=(0,0,1;0rad)
  Refine = true
  Tool = -> Fusion001005002004004005002010002003003003017007024035
FEATURE [Part::Cylinder] Cylinder726  label="Cylinder796"
  Angle = 360
  AttacherType = Attacher::AttachEngine3D
  Height = 4
  Placement = pos=(0,-8,32) rot=(0,0,1;0rad)
  Radius = 30.2
FEATURE [Part::Cut] Cut012035011
  Base = -> Cylinder672
  Refine = true
  Tool = -> Cylinder726
FEATURE [Part::Cylinder] Cylinder727  label="Cylinder797"
  Angle = 360
  AttacherType = Attacher::AttachEngine3D
  Height = 1
  Placement = pos=(0,-8,31) rot=(0,0,1;0rad)
  Radius = 21
FEATURE [Part::Cut] Cut012035012
  Base = -> Cut012035011
  Refine = true
  Tool = -> Cylinder727
FEATURE [Part::Cylinder] Cylinder728  label="Cylinder798"
  Angle = 360
  AttacherType = Attacher::AttachEngine3D
  Height = 5
  Placement = pos=(0,-8,28) rot=(0,0,1;0rad)
  Radius = 30
FEATURE [Part::Cylinder] Cylinder729  label="Cylinder799"
  Angle = 360
  AttacherType = Attacher::AttachEngine3D
  Height = 5
  Placement = pos=(0,-8,28) rot=(0,0,1;0rad)
  Radius = 20
FEATURE [Part::Cut] Cut012035013  label="bearing"
  Base = -> Cylinder728
  Placement = pos=(0,0,4) rot=(0,0,1;0rad)
  Refine = true
  Tool = -> Cylinder729
FEATURE [Part::Cylinder] Cylinder730  label="Cylinder800"
  Angle = 360
  AttacherType = Attacher::AttachEngine3D
  Height = 4
  Placement = pos=(0,-8,34) rot=(0,0,1;0rad)
  Radius = 34
FEATURE [Part::Cut] Cut012035014
  Base = -> Cut012035012
  Refine = true
  Tool = -> Cylinder730
FEATURE [Part::Chamfer] Chamfer007002
  Base = -> Cut012035014
  Edges = 1 edges r=1: [Edge7]
FEATURE [Part::Cylinder] Cylinder743  label="Cylinder813"
  Angle = 360
  AttacherType = Attacher::AttachEngine3D
  Height = 4
  Placement = pos=(0,-8,22) rot=(0,0,1;0rad)
  Radius = 5.6
FEATURE [Part::Cylinder] Cylinder744  label="Cylinder814"
  Angle = 360
  AttacherType = Attacher::AttachEngine3D
  Height = 10
  Placement = pos=(0,-8,22) rot=(0,0,1;0rad)
  Radius = 2.7
FEATURE [Part::Cylinder] Cylinder745  label="Cylinder815"
  Angle = 360
  AttacherType = Attacher::AttachEngine3D
  Height = 9
  Placement = pos=(33,-43.25,5) rot=(-1,0,0;1.5708rad)
  Radius = 4
FEATURE [Part::Box] Box062  label="Cube062"
  AttacherType = Attacher::AttachEngine3D
  Height = 2
  Length = 8
  Placement = pos=(29,-43.25,5) rot=(0,0,1;0rad)
  Width = 8.5
FEATURE [Part::Cylinder] Cylinder747  label="Cylinder817"
  Angle = 360
  AttacherType = Attacher::AttachEngine3D
  Height = 9
  Placement = pos=(-4.5,-50.5,-7) rot=(0,0,1;0rad)
  Radius = 1.6
FEATURE [Part::Cylinder] Cylinder748  label="Cylinder818"
  Angle = 360
  AttacherType = Attacher::AttachEngine3D
  Height = 9
  Placement = pos=(4.5,-50.5,-7) rot=(0,0,1;0rad)
  Radius = 1.6
FEATURE [Part::MultiFuse] Fusion001005002004004005002010002003003003017007024041010004  label="Fusion-074"
  Placement = pos=(0,4,-3) rot=(0,0,1;0rad)
  Refine = true
  Shapes = -> [Cylinder748,Cylinder747]
FEATURE [Part::Cylinder] Cylinder749  label="Cylinder819"
  Angle = 360
  AttacherType = Attacher::AttachEngine3D
  Height = 9
  Placement = pos=(-4.5,-50.5,-7) rot=(0,0,1;0rad)
  Radius = 1.6
FEATURE [Part::Cylinder] Cylinder750  label="Cylinder820"
  Angle = 360
  AttacherType = Attacher::AttachEngine3D
  Height = 9
  Placement = pos=(4.5,-50.5,-7) rot=(0,0,1;0rad)
  Radius = 1.6
FEATURE [Part::MultiFuse] Fusion001005002004004005002010002003003003017007024041010005  label="Fusion-075"
  Placement = pos=(0,18,-3) rot=(0,0,1;0rad)
  Refine = true
  Shapes = -> [Cylinder750,Cylinder749]
FEATURE [Part::MultiFuse] Fusion001005002004004005002010002003003003017007024041010006  label="Fusion-076"
  Refine = true
  Shapes = -> [Fusion001005002004004005002010002003003003017007024041010005,Fusion001005002004004005002010002003003003017007024041010004]
FEATURE [Part::Cylinder] Cylinder751  label="Cylinder821"
  Angle = 360
  AttacherType = Attacher::AttachEngine3D
  Height = 9
  Placement = pos=(-4.5,-50.5,-7) rot=(0,0,1;0rad)
  Radius = 1.6
FEATURE [Part::Cylinder] Cylinder752  label="Cylinder822"
  Angle = 360
  AttacherType = Attacher::AttachEngine3D
  Height = 9
  Placement = pos=(4.5,-50.5,-7) rot=(0,0,1;0rad)
  Radius = 1.6
FEATURE [Part::MultiFuse] Fusion001005002004004005002010002003003003017007024041010007  label="Fusion-077"
  Placement = pos=(0,4,-3) rot=(0,0,1;0rad)
  Refine = true
  Shapes = -> [Cylinder752,Cylinder751]
FEATURE [Part::Cylinder] Cylinder753  label="Cylinder823"
  Angle = 360
  AttacherType = Attacher::AttachEngine3D
  Height = 9
  Placement = pos=(4.5,-50.5,-7) rot=(0,0,1;0rad)
  Radius = 1.6
FEATURE [Part::Cylinder] Cylinder754  label="Cylinder824"
  Angle = 360
  AttacherType = Attacher::AttachEngine3D
  Height = 9
  Placement = pos=(-4.5,-50.5,-7) rot=(0,0,1;0rad)
  Radius = 1.6
FEATURE [Part::MultiFuse] Fusion001005002004004005002010002003003003017007024041010009  label="Fusion-079"
  Placement = pos=(0,18,-3) rot=(0,0,1;0rad)
  Refine = true
  Shapes = -> [Cylinder753,Cylinder754]
FEATURE [Part::MultiFuse] Fusion001005002004004005002010002003003003017007024041010008  label="Fusion-078"
  Placement = pos=(0,63,0) rot=(0,0,1;0rad)
  Refine = true
  Shapes = -> [Fusion001005002004004005002010002003003003017007024041010009,Fusion001005002004004005002010002003003003017007024041010007]
FEATURE [Part::MultiFuse] Fusion001005002004004005002010002003003003017007024041010010  label="Fusion-080"
  Refine = true
  Shapes = -> [Fusion001005002004004005002010002003003003017007024041010006,Fusion001005002004004005002010002003003003017007024041010008]
FEATURE [Part::Cut] Cut012035015003002
  Base = -> Cut012035
  Refine = true
  Tool = -> Fusion001005002004004005002010002003003003017007024041010010
FEATURE [Part::Feature] Cut012035015003002001  label="Cut012035015003003"
  shape: bbox 15 x 128 x 13 mm, 125 faces (baked)
FEATURE [Part::Cut] Cut012035015003002002  label="axle-upper-part"
  Base = -> Cut012035015003002
  Refine = true
  Tool = -> Box019
FEATURE [Part::Cut] Cut012035015003002003  label="axle-lower-part"
  Base = -> Cut012035015003002001
  Refine = true
  Tool = -> Box020
FEATURE [Part::Box] Box063  label="Cube063"
  AttacherType = Attacher::AttachEngine3D
  Height = 3
  Length = 70
  Placement = pos=(-35,-43,37) rot=(0,0,1;0rad)
  Width = 70
FEATURE [Part::Cylinder] Cylinder755  label="Cylinder825"
  Angle = 360
  AttacherType = Attacher::AttachEngine3D
  Height = 8
  Placement = pos=(0,-8,31.5) rot=(0,0,1;0rad)
  Radius = 19.5
FEATURE [Part::Cylinder] Cylinder756  label="Cylinder826"
  Angle = 360
  AttacherType = Attacher::AttachEngine3D
  Height = 3
  Placement = pos=(0,-8,34.5) rot=(0,0,1;0rad)
  Radius = 33.5
FEATURE [Part::Cylinder] Cylinder757  label="Cylinder827"
  Angle = 360
  AttacherType = Attacher::AttachEngine3D
  Height = 3
  Placement = pos=(0,-8,34.5) rot=(0,0,1;0rad)
  Radius = 30.2
FEATURE [Part::Cut] Cut012035015003002004  label="Cut0000"
  Base = -> Cylinder756
  Refine = true
  Tool = -> Cylinder757
FEATURE [Part::Chamfer] Chamfer007008
  Base = -> Cut012035015003002004
  Edges = 1 edges r=1.3: [Edge5]
FEATURE [Part::MultiFuse] Fusion001005002004004005002010002003003003017007024041010011  label="Fusion-081"
  Refine = true
  Shapes = -> [Box063,Cylinder755,Chamfer007008]
FEATURE [Part::Cylinder] Cylinder758  label="Cylinder828"
  Angle = 360
  AttacherType = Attacher::AttachEngine3D
  Height = 10
  Placement = pos=(0,-8,31.5) rot=(0,0,1;0rad)
  Radius = 2.5
FEATURE [Part::Cut] Cut012035015003002005
  Base = -> Fusion001005002004004005002010002003003003017007024041010011
  Refine = true
  Tool = -> Cylinder758
FEATURE [Part::Cylinder] Cylinder759  label="Cylinder829"
  Angle = 360
  AttacherType = Attacher::AttachEngine3D
  Height = 10
  Placement = pos=(30,-38,30) rot=(0,0,1;0rad)
  Radius = 1.6
FEATURE [Part::Cylinder] Cylinder760  label="Cylinder830"
  Angle = 360
  AttacherType = Attacher::AttachEngine3D
  Height = 10
  Placement = pos=(-30,-38,30) rot=(0,0,1;0rad)
  Radius = 1.6
FEATURE [Part::Cylinder] Cylinder761  label="Cylinder831"
  Angle = 360
  AttacherType = Attacher::AttachEngine3D
  Height = 10
  Placement = pos=(30,22,30) rot=(0,0,1;0rad)
  Radius = 1.6
FEATURE [Part::Cylinder] Cylinder762  label="Cylinder832"
  Angle = 360
  AttacherType = Attacher::AttachEngine3D
  Height = 10
  Placement = pos=(-30,22,30) rot=(0,0,1;0rad)
  Radius = 1.6
FEATURE [Part::MultiFuse] Fusion001005002004004005002010002003003003017007024041010012  label="Fusion-082"
  Refine = true
  Shapes = -> [Cylinder762,Cylinder759,Cylinder761,Cylinder760]
FEATURE [Part::Cut] Cut012035015003002006
  Base = -> Cut012035015003002005
  Refine = true
  Tool = -> Fusion001005002004004005002010002003003003017007024041010012
FEATURE [Part::Cylinder] Cylinder763  label="Cylinder833"
  Angle = 360
  AttacherType = Attacher::AttachEngine3D
  Height = 10
  Placement = pos=(0,5,30) rot=(0,0,1;0rad)
  Radius = 1.25
FEATURE [Part::Cylinder] Cylinder764  label="Cylinder834"
  Angle = 360
  AttacherType = Attacher::AttachEngine3D
  Height = 10
  Placement = pos=(0,-21,30) rot=(0,0,1;0rad)
  Radius = 1.25
FEATURE [Part::MultiFuse] Fusion001005002004004005002010002003003003017007024041010013  label="Fusion-083"
  Refine = true
  Shapes = -> [Cylinder764,Cylinder763]
FEATURE [Part::Cut] Cut012035015003002007  label="rotation-upper-platform_"
  Base = -> Cut012035015003002006
  Refine = true
  Tool = -> Fusion001005002004004005002010002003003003017007024041010013
FEATURE [Part::Box] Box064  label="Cube064"
  AttacherType = Attacher::AttachEngine3D
  Height = 10
  Length = 55
  Placement = pos=(-35,-43,40) rot=(0,0,1;0rad)
  Width = 35
FEATURE [Part::Cylinder] Cylinder766  label="Cylinder836"
  Angle = 360
  AttacherType = Attacher::AttachEngine3D
  Height = 10
  Placement = pos=(-30,-38,30) rot=(0,0,1;0rad)
  Radius = 1.25
FEATURE [Part::Cylinder] Cylinder767  label="Cylinder837"
  Angle = 360
  AttacherType = Attacher::AttachEngine3D
  Height = 10
  Placement = pos=(30,-38,30) rot=(0,0,1;0rad)
  Radius = 1.25
FEATURE [Part::Cylinder] Cylinder768  label="Cylinder838"
  Angle = 360
  AttacherType = Attacher::AttachEngine3D
  Height = 10
  Placement = pos=(0,-21,40) rot=(0,0,1;0rad)
  Radius = 1.6
FEATURE [Part::MultiFuse] Fusion001005002004004005002010002003003003017007024041010015  label="Fusion-085"
  Placement = pos=(0,0,10) rot=(0,0,1;0rad)
  Refine = true
  Shapes = -> [Cylinder766,Cylinder767]
FEATURE [Part::Cylinder] Cylinder769  label="Cylinder839"
  Angle = 360
  AttacherType = Attacher::AttachEngine3D
  Height = 3
  Placement = pos=(0,-21,47) rot=(0,0,1;0rad)
  Radius = 3.2
FEATURE [Part::MultiFuse] Fusion001005002004004005002010002003003003017007024041010016  label="Fusion-086"
  Refine = true
  Shapes = -> [Cylinder769,Cylinder768]
FEATURE [Part::Cylinder] Cylinder770  label="Cylinder840"
  Angle = 360
  AttacherType = Attacher::AttachEngine3D
  Height = 25
  Placement = pos=(-23,-43,45) rot=(-1,0,0;1.5708rad)
  Radius = 3.2
FEATURE [Part::Cylinder] Cylinder771  label="Cylinder841"
  Angle = 360
  AttacherType = Attacher::AttachEngine3D
  Height = 35
  Placement = pos=(-23,-43,45) rot=(-1,0,0;1.5708rad)
  Radius = 1.6
FEATURE [Part::Cylinder] Cylinder772  label="Cylinder842"
  Angle = 360
  AttacherType = Attacher::AttachEngine3D
  Height = 50
  Placement = pos=(-23,-43,45) rot=(-1,0,0;1.5708rad)
  Radius = 1.25
FEATURE [Part::MultiFuse] Fusion001005002004004005002010002003003003017007024041010017  label="Fusion-087"
  Refine = true
  Shapes = -> [Cylinder772,Cylinder771,Cylinder770]
FEATURE [Part::Cylinder] Cylinder773  label="Cylinder843"
  Angle = 360
  AttacherType = Attacher::AttachEngine3D
  Height = 35
  Placement = pos=(-23,-43,45) rot=(-1,0,0;1.5708rad)
  Radius = 1.6
FEATURE [Part::Cylinder] Cylinder774  label="Cylinder844"
  Angle = 360
  AttacherType = Attacher::AttachEngine3D
  Height = 25
  Placement = pos=(-23,-43,45) rot=(-1,0,0;1.5708rad)
  Radius = 3.2
FEATURE [Part::Cylinder] Cylinder775  label="Cylinder845"
  Angle = 360
  AttacherType = Attacher::AttachEngine3D
  Height = 50
  Placement = pos=(-23,-43,45) rot=(-1,0,0;1.5708rad)
  Radius = 1.25
FEATURE [Part::MultiFuse] Fusion001005002004004005002010002003003003017007024041010018  label="Fusion-088"
  Placement = pos=(38,0,0) rot=(0,0,1;0rad)
  Refine = true
  Shapes = -> [Cylinder775,Cylinder773,Cylinder774]
FEATURE [Part::Cylinder] Cylinder776  label="Cylinder846"
  Angle = 360
  AttacherType = Attacher::AttachEngine3D
  Height = 25
  Placement = pos=(-23,-43,45) rot=(-1,0,0;1.5708rad)
  Radius = 3.2
FEATURE [Part::Cylinder] Cylinder777  label="Cylinder847"
  Angle = 360
  AttacherType = Attacher::AttachEngine3D
  Height = 50
  Placement = pos=(-23,-43,45) rot=(-1,0,0;1.5708rad)
  Radius = 1.25
FEATURE [Part::Cylinder] Cylinder778  label="Cylinder848"
  Angle = 360
  AttacherType = Attacher::AttachEngine3D
  Height = 35
  Placement = pos=(-23,-43,45) rot=(-1,0,0;1.5708rad)
  Radius = 1.6
FEATURE [Part::MultiFuse] Fusion001005002004004005002010002003003003017007024041010019  label="Fusion-089"
  Placement = pos=(68,0,0) rot=(0,0,1;0rad)
  Refine = true
  Shapes = -> [Cylinder777,Cylinder778,Cylinder776]
FEATURE [Part::Cylinder] Cylinder779  label="Cylinder849"
  Angle = 360
  AttacherType = Attacher::AttachEngine3D
  Height = 25
  Placement = pos=(-23,-43,45) rot=(-1,0,0;1.5708rad)
  Radius = 3.2
FEATURE [Part::Cylinder] Cylinder780  label="Cylinder850"
  Angle = 360
  AttacherType = Attacher::AttachEngine3D
  Height = 50
  Placement = pos=(-23,-43,45) rot=(-1,0,0;1.5708rad)
  Radius = 1.25
FEATURE [Part::Cylinder] Cylinder781  label="Cylinder851"
  Angle = 360
  AttacherType = Attacher::AttachEngine3D
  Height = 35
  Placement = pos=(-23,-43,45) rot=(-1,0,0;1.5708rad)
  Radius = 1.6
FEATURE [Part::MultiFuse] Fusion001005002004004005002010002003003003017007024041010020  label="Fusion-090"
  Placement = pos=(83,0,-11.5) rot=(0,0,1;0rad)
  Refine = true
  Shapes = -> [Cylinder780,Cylinder781,Cylinder779]
FEATURE [Part::Cylinder] Cylinder788  label="Cylinder858"
  Angle = 360
  AttacherType = Attacher::AttachEngine3D
  Height = 35
  Placement = pos=(-23,-43,45) rot=(-1,0,0;1.5708rad)
  Radius = 1.6
FEATURE [Part::MultiFuse] Fusion001005002004004005002010002003003003017007024041010014  label="Fusion-084"
  Refine = true
  Shapes = -> [Fusion001005002004004005002010002003003003017007007,Box064,Cylinder788]
FEATURE [Part::Cylinder] Cylinder789  label="Cylinder859"
  Angle = 360
  AttacherType = Attacher::AttachEngine3D
  Height = 24.5
  Placement = pos=(70,-43,30) rot=(-1,0,0;1.5708rad)
  Radius = 1.6
FEATURE [Part::Cylinder] Cylinder790  label="Cylinder860"
  Angle = 360
  AttacherType = Attacher::AttachEngine3D
  Height = 24.5
  Placement = pos=(90,-43,30) rot=(-1,0,0;1.5708rad)
  Radius = 1.6
FEATURE [Part::Cylinder] Cylinder791  label="Cylinder861"
  Angle = 360
  AttacherType = Attacher::AttachEngine3D
  Height = 24.5
  Placement = pos=(110,-43,30) rot=(-1,0,0;1.5708rad)
  Radius = 1.6
FEATURE [Part::MultiFuse] Fusion001005002004004005002010002003003003017007024041010024  label="Fusion-094"
  Refine = true
  Shapes = -> [Cylinder789,Cylinder791,Cylinder790]
FEATURE [Part::MultiFuse] Fusion001005002004004005002010002003003003017007024041010025  label="Fusion-095"
  Refine = true
  Shapes = -> [Fusion001005002004004005002010002003003003017007024041010024,Fusion001005002004004005002010002003003003017007024041010015,Fusion001005002004004005002010002003003003017007024041010016]
FEATURE [Part::Cylinder] Cylinder792  label="Cylinder862"
  Angle = 360
  AttacherType = Attacher::AttachEngine3D
  Height = 5
  Placement = pos=(-40,14,45) rot=(0,1,0;1.5708rad)
  Radius = 1.6
FEATURE [Part::Cylinder] Cylinder793  label="Cylinder863"
  Angle = 360
  AttacherType = Attacher::AttachEngine3D
  Height = 5
  Placement = pos=(-40,-30,45) rot=(0,1,0;1.5708rad)
  Radius = 1.6
FEATURE [Part::Cone] Cone
  Angle = 360
  AttacherType = Attacher::AttachEngine3D
  Height = 2.5
  Placement = pos=(-40,-30,45) rot=(0,1,0;1.5708rad)
  Radius1 = 3
  Radius2 = 1.6
FEATURE [Part::Cone] Cone001
  Angle = 360
  AttacherType = Attacher::AttachEngine3D
  Height = 2.5
  Placement = pos=(-40,14,45) rot=(0,1,0;1.5708rad)
  Radius1 = 3
  Radius2 = 1.6
FEATURE [Part::Cylinder] Cylinder794  label="Cylinder864"
  Angle = 360
  AttacherType = Attacher::AttachEngine3D
  Height = 15
  Placement = pos=(-40,14,45) rot=(0,1,0;1.5708rad)
  Radius = 1.25
FEATURE [Part::Cylinder] Cylinder795  label="Cylinder865"
  Angle = 360
  AttacherType = Attacher::AttachEngine3D
  Height = 15
  Placement = pos=(-40,-30,45) rot=(0,1,0;1.5708rad)
  Radius = 1.25
FEATURE [Part::MultiFuse] Fusion001005002004004005002010002003003003017007024041010023002  label="Fusion-097"
  Refine = true
  Shapes = -> [Cylinder792,Cylinder794,Cone001]
FEATURE [Part::MultiFuse] Fusion001005002004004005002010002003003003017007024041010023003  label="Fusion-098"
  Refine = true
  Shapes = -> [Cylinder793,Cylinder795,Cone]
FEATURE [Part::Feature] Fusion001005002004004005002010002003003003017007024041010023003001  label="Fusion-100"
  shape: bbox 15 x 6 x 6 mm, 6 faces (baked)
FEATURE [Part::MultiFuse] Fusion001005002004004005002010002003003003017007024041010023003002  label="Fusion-101"
  Refine = true
  Shapes = -> [Fusion001005002004004005002010002003003003017007024041010023002,Fusion001005002004004005002010002003003003017007024041010023003]
FEATURE [Part::Feature] Face
  shape: bbox 2e-07 x 5.5 x 16.5 mm, 1 faces, 0 solids (baked)
FEATURE [Part::Extrusion] Extrude004
  Base = -> Face
  Dir = (-1,0,0)
  DirMode = 0
  FaceMakerClass = Part::FaceMakerBullseye
  LengthFwd = 3
  LengthRev = 0
  Solid = true
  Symmetric = false
FEATURE [Part::MultiFuse] Fusion001005002004004005002010002003003003017007024041010023003003  label="Fusion-102"
  Refine = true
  Shapes = -> [Cut012012,Extrude004]
FEATURE [Part::Box] Box065  label="Cube065"
  AttacherType = Attacher::AttachEngine3D
  Height = 15
  Length = 5
  Placement = pos=(-3,-101,37) rot=(0,0,-1;0rad)
  Width = 186
FEATURE [Part::Box] Box066  label="Cube066"
  AttacherType = Attacher::AttachEngine3D
  Height = 15
  Length = 2
  Placement = pos=(-5,-101,37) rot=(0,0,-1;0rad)
  Width = 5
FEATURE [Part::Box] Box067  label="Cube067"
  AttacherType = Attacher::AttachEngine3D
  Height = 15
  Length = 2
  Placement = pos=(-5,80,37) rot=(0,0,-1;0rad)
  Width = 5
FEATURE [Part::MultiFuse] Fusion001005002004004005002010002003003003017007024041010023003003003  label="Fusion-105"
  Refine = true
  Shapes = -> [Fusion001005002004004005002010002003003003017007010,Box066,Box067]
FEATURE [Part::MultiFuse] Fusion001005002004004005002010002003003003017007024041010023003003004  label="Fusion-106"
  Refine = true
  Shapes = -> [Box065,Box030,Box031]
FEATURE [Part::Cut] Cut012035015003002009004
  Base = -> Fusion001005002004004005002010002003003003017007024041010023003003003
  Refine = true
  Tool = -> Fusion001005002004004005002010002003003003017007024041010023003003004
FEATURE [Part::Feature] Fusion001005002004004005002010002003003003017007024041010023003003006006003001  label="Fusion-121"
  shape: bbox 75.97 x 184 x 4 mm, 48 faces, 8 solids (baked)
FEATURE [Part::Cut] Cut012035015003002009007
  Base = -> Cut012035015003002009004
  Refine = true
  Tool = -> Fusion001005002004004005002010002003003003017007024041010023003003006006003001
FEATURE [Part::Cut] Cut012035015003002009008  label="border-front"
  Base = -> Cut012035015003002009007
  Refine = true
  Tool = -> Fusion001005002004004005002010002003003003017007024041010023003002
FEATURE [Part::Cylinder] Cylinder812  label="Cylinder882"
  Angle = 360
  AttacherType = Attacher::AttachEngine3D
  Height = 4
  Placement = pos=(0,0,0) rot=(-1,0,0;1.5708rad)
  Radius = 1.2
FEATURE [Part::Cylinder] Cylinder813  label="Cylinder883"
  Angle = 360
  AttacherType = Attacher::AttachEngine3D
  Height = 4
  Placement = pos=(0,0,0) rot=(-1,0,0;1.5708rad)
  Radius = 1.2
FEATURE [Part::Cone] Cone010
  Angle = 360
  AttacherType = Attacher::AttachEngine3D
  Height = 1
  Placement = pos=(0,0,0) rot=(-1,0,0;1.5708rad)
  Radius1 = 2
  Radius2 = 1.2
FEATURE [Part::Cylinder] Cylinder814  label="Cylinder884"
  Angle = 360
  AttacherType = Attacher::AttachEngine3D
  Height = 7
  Placement = pos=(0,0,0) rot=(-1,0,0;1.5708rad)
  Radius = 0.8
FEATURE [Part::Cone] Cone011
  Angle = 360
  AttacherType = Attacher::AttachEngine3D
  Height = 1
  Placement = pos=(0,0,0) rot=(-1,0,0;1.5708rad)
  Radius1 = 2
  Radius2 = 1.2
FEATURE [Part::MultiFuse] Fusion001005002004004005002010002003003003017007024041010023003003006006003002  label="Fusion-122"
  Placement = pos=(46,-100,47) rot=(0,0,1;0rad)
  Refine = true
  Shapes = -> [Cone010,Cylinder812,Cylinder814]
FEATURE [Part::Cylinder] Cylinder815  label="Cylinder885"
  Angle = 360
  AttacherType = Attacher::AttachEngine3D
  Height = 7
  Placement = pos=(0,0,0) rot=(-1,0,0;1.5708rad)
  Radius = 0.8
FEATURE [Part::MultiFuse] Fusion001005002004004005002010002003003003017007024041010023003003006006003003  label="Fusion-123"
  Placement = pos=(2,-100,47) rot=(0,0,1;0rad)
  Refine = true
  Shapes = -> [Cone011,Cylinder813,Cylinder815]
FEATURE [Part::MultiFuse] Fusion001005002004004005002010002003003003017007024041010023003003006006003004  label="Fusion-124"
  Refine = true
  Shapes = -> [Fusion001005002004004005002010002003003003017007024041010023003003006006003002,Fusion001005002004004005002010002003003003017007024041010023003003006006003003]
FEATURE [Part::RegularPolygon] RegularPolygon  label="Regular polygon"
  AttacherType = Attacher::AttachEngine3D
  Circumradius = 3
  Polygon = 6
FEATURE [Part::Extrusion] Extrude005
  Base = -> RegularPolygon
  Dir = (0,0,1)
  DirMode = 2
  FaceMakerClass = Part::FaceMakerBullseye
  LengthFwd = 10.3
  LengthRev = 0
  Placement = pos=(110,-8,30) rot=(1,0,0;1.5708rad)
  Solid = true
  Symmetric = false
FEATURE [Part::RegularPolygon] RegularPolygon001  label="Regular polygon001"
  AttacherType = Attacher::AttachEngine3D
  Circumradius = 3
  Polygon = 6
FEATURE [Part::Extrusion] Extrude006
  Base = -> RegularPolygon001
  Dir = (0,0,1)
  DirMode = 2
  FaceMakerClass = Part::FaceMakerBullseye
  LengthFwd = 10.3
  LengthRev = 0
  Placement = pos=(90,-8,30) rot=(1,0,0;1.5708rad)
  Solid = true
  Symmetric = false
FEATURE [Part::RegularPolygon] RegularPolygon002  label="Regular polygon002"
  AttacherType = Attacher::AttachEngine3D
  Circumradius = 3
  Polygon = 6
FEATURE [Part::Extrusion] Extrude007
  Base = -> RegularPolygon002
  Dir = (0,0,1)
  DirMode = 2
  FaceMakerClass = Part::FaceMakerBullseye
  LengthFwd = 10.3
  LengthRev = 0
  Placement = pos=(70,-8,30) rot=(1,0,0;1.5708rad)
  Solid = true
  Symmetric = false
FEATURE [Part::MultiFuse] Fusion001005002004004005002010002003003003017007024041010023003003006006003005  label="Fusion-125"
  Refine = true
  Shapes = -> [Extrude005,Extrude006,Extrude007]
FEATURE [Part::MultiFuse] Fusion001005002004004005002010002003003003017007024041010023003003006006003006  label="Fusion000"
  Refine = true
  Shapes = -> [Fusion001005002004004005002010002003003003017007024041010017,Fusion001005002004004005002010002003003003017007024041010018,Fusion001005002004004005002010002003003003017007024041010019,Fusion001005002004004005002010002003003003017007024041010020]
FEATURE [Part::Feature] Fusion001005002004004005002010002003003003017007024041010023003003006006003006001  label="Fusion001"
  shape: bbox 89.4 x 50 x 17.9 mm, 28 faces, 4 solids (baked)
FEATURE [Part::RegularPolygon] RegularPolygon003  label="Regular polygon003"
  AttacherType = Attacher::AttachEngine3D
  Circumradius = 4.7
  Polygon = 6
FEATURE [Part::Extrusion] Extrude008
  Base = -> RegularPolygon003
  Dir = (0,0,1)
  DirMode = 2
  FaceMakerClass = Part::FaceMakerBullseye
  LengthFwd = 10
  LengthRev = 0
  Placement = pos=(0,-8,40) rot=(0,0,1;0rad)
  Solid = true
  Symmetric = false
FEATURE [Part::Cut] Cut012035015003002009009
  Base = -> Fusion001005002004004005002010002003003003017007024041010014
  Refine = true
  Tool = -> Extrude008
FEATURE [Part::Cut] Cut012035015003002009010
  Base = -> Cut012035015003002009009
  Refine = true
  Tool = -> Fusion001005002004004005002010002003003003017007024041010025
FEATURE [Part::Cylinder] Cylinder816  label="Cylinder886"
  Angle = 360
  AttacherType = Attacher::AttachEngine3D
  Height = 3
  Placement = pos=(-12,-46,44) rot=(-1,0,0;1.5708rad)
  Radius = 1.6
FEATURE [Part::Cylinder] Cylinder817  label="Cylinder887"
  Angle = 360
  AttacherType = Attacher::AttachEngine3D
  Height = 15
  Placement = pos=(-12,-46,44) rot=(-1,0,0;1.5708rad)
  Radius = 1.25
FEATURE [Part::MultiFuse] Fusion001005002004004005002010002003003003017007024041010023003003006006003006002  label="Fusion-126"
  Placement = pos=(0,0,-0.5) rot=(0,0,1;0rad)
  Refine = true
  Shapes = -> [Cylinder817,Cylinder816]
FEATURE [Part::Cylinder] Cylinder818  label="Cylinder888"
  Angle = 360
  AttacherType = Attacher::AttachEngine3D
  Height = 3
  Placement = pos=(-12,-46,44) rot=(-1,0,0;1.5708rad)
  Radius = 1.6
FEATURE [Part::Cylinder] Cylinder819  label="Cylinder889"
  Angle = 360
  AttacherType = Attacher::AttachEngine3D
  Height = 15
  Placement = pos=(-12,-46,44) rot=(-1,0,0;1.5708rad)
  Radius = 1.25
FEATURE [Part::MultiFuse] Fusion001005002004004005002010002003003003017007024041010023003003006006003006003  label="Fusion-127"
  Placement = pos=(50,0,-0.5) rot=(0,0,1;0rad)
  Refine = true
  Shapes = -> [Cylinder819,Cylinder818]
FEATURE [Part::Cylinder] Cylinder822  label="Cylinder892"
  Angle = 360
  AttacherType = Attacher::AttachEngine3D
  Height = 3
  Placement = pos=(-12,-46,44) rot=(-1,0,0;1.5708rad)
  Radius = 1.6
FEATURE [Part::Cylinder] Cylinder823  label="Cylinder893"
  Angle = 360
  AttacherType = Attacher::AttachEngine3D
  Height = 15
  Placement = pos=(-12,-46,44) rot=(-1,0,0;1.5708rad)
  Radius = 1.25
FEATURE [Part::MultiFuse] Fusion001005002004004005002010002003003003017007024041010023003003006006003006004  label="Fusion-128"
  Placement = pos=(60,0,-5) rot=(0,0,1;0rad)
  Refine = true
  Shapes = -> [Cylinder823,Cylinder822]
FEATURE [Part::Cylinder] Cylinder824  label="Cylinder894"
  Angle = 360
  AttacherType = Attacher::AttachEngine3D
  Height = 3
  Placement = pos=(-12,-46,44) rot=(-1,0,0;1.5708rad)
  Radius = 1.6
FEATURE [Part::Cylinder] Cylinder825  label="Cylinder895"
  Angle = 360
  AttacherType = Attacher::AttachEngine3D
  Height = 15
  Placement = pos=(-12,-46,44) rot=(-1,0,0;1.5708rad)
  Radius = 1.25
FEATURE [Part::MultiFuse] Fusion001005002004004005002010002003003003017007024041010023003003006006003006005  label="Fusion-129"
  Placement = pos=(74.5,0,-15) rot=(0,0,1;0rad)
  Refine = true
  Shapes = -> [Cylinder825,Cylinder824]
FEATURE [Part::MultiFuse] Fusion001005002004004005002010002003003003017007024041010023003003006006003006007  label="Fusion-131"
  Refine = true
  Shapes = -> [Fusion001005002004004005002010002003003003017007024041010023003003006006003006003,Fusion001005002004004005002010002003003003017007024041010023003003006006003006002]
FEATURE [Part::MultiFuse] Fusion001005002004004005002010002003003003017007024041010023003003006006003006008  label="Fusion-132"
  Refine = true
  Shapes = -> [Fusion001005002004004005002010002003003003017007024041010023003003006006003006004,Fusion001005002004004005002010002003003003017007024041010023003003006006003006005]
FEATURE [Part::Cut] Cut012035015003002009014
  Base = -> Cut012035015003002009010
  Refine = true
  Tool = -> Fusion001005002004004005002010002003003003017007024041010023003003006006003005
FEATURE [Part::Cut] Cut012035015003002009015
  Base = -> Cut012035015003002009014
  Refine = true
  Tool = -> Fusion001005002004004005002010002003003003017007024041010023003003006006003006007
FEATURE [Part::Cut] Cut012035015003002009022
  Base = -> Cut012035015003002009015
  Refine = true
  Tool = -> Fusion001005002004004005002010002003003003017007024041010023003003006006003006008
FEATURE [Part::Cut] Cut012035015003002009023
  Base = -> Cut012035015003002009022
  Refine = true
  Tool = -> Fusion001005002004004005002010002003003003017007024041010023003001
FEATURE [Part::Cylinder] Cylinder831  label="Cylinder901"
  Angle = 360
  AttacherType = Attacher::AttachEngine3D
  Height = 10
  Placement = pos=(53,-38,34) rot=(0,1,0;0.785398rad)
  Radius = 1.25
FEATURE [Part::Cut] Cut012035015003002009024  label="frame-front-left-000"
  Base = -> Cut012035015003002009023
  Refine = true
  Tool = -> Cylinder831
FEATURE [Part::Feature] Cut012035015003002009024001  label="frame-front-left-001"
  shape: bbox 150 x 35 x 37.17 mm, 66 faces (baked)
FEATURE [Part::Mirroring] Part__Mirroring004  label="frame-front-right-000"
  Base = (0,0,0)
  Normal = (0,1,0)
  Placement = pos=(0,-16,0) rot=(0,0,1;0rad)
  Source = -> Cut012035015003002009024001
FEATURE [Part::Cut] Cut012035015003002009024002  label="frame-front-left"
  Base = -> Cut012035015003002009024
  Refine = true
  Tool = -> Fusion001005002004004005002010002003003003017007024041010023003003006006003006
FEATURE [Part::Cut] Cut012035015003002009024003  label="frame-front-right"
  Base = -> Part__Mirroring004
  Refine = true
  Tool = -> Fusion001005002004004005002010002003003003017007024041010023003003006006003006001
FEATURE [Part::Cylinder] Cylinder837  label="Cylinder907"
  Angle = 360
  AttacherType = Attacher::AttachEngine3D
  Height = 8
  Placement = pos=(0,-8,28) rot=(0,0,1;0rad)
  Radius = 35
FEATURE [Part::MultiFuse] Fusion001005002004004005002010002003003003017007024041006  label="Fusion-071"
  Refine = true
  Shapes = -> [Cylinder743,Cylinder744]
FEATURE [Part::Box] Box081  label="Cube081"
  AttacherType = Attacher::AttachEngine3D
  Height = 6
  Length = 78
  Placement = pos=(-39,-43,22) rot=(0,0,1;0rad)
  Width = 70
FEATURE [Part::MultiFuse] Fusion001005002004004005002010002003003003017007024041010023003003006006003006008008  label="Fusion-141"
  Refine = true
  Shapes = -> [Box058,Box081]
FEATURE [Part::Cut] Cut012035015003002009024007
  Base = -> Fusion001005002004004005002010002003003003017007024041010023003003006006003006008008
  Refine = true
  Tool = -> Cylinder837
FEATURE [Part::MultiFuse] Fusion001005002004004005002010002003003003017007024041010023003003006006003006008009  label="Fusion-142"
  Refine = true
  Shapes = -> [Cut012035015003002009024007,Chamfer007002]
FEATURE [Part::Box] Box082  label="Cube082"
  AttacherType = Attacher::AttachEngine3D
  Height = 14
  Length = 14.2
  Placement = pos=(-39,-43,22) rot=(0,0,1;0rad)
  Width = 10.2
FEATURE [Part::Box] Box083  label="Cube083"
  AttacherType = Attacher::AttachEngine3D
  Height = 14
  Length = 14.2
  Placement = pos=(-39,16.8,22) rot=(0,0,1;0rad)
  Width = 10.2
FEATURE [Part::Box] Box084  label="Cube084"
  AttacherType = Attacher::AttachEngine3D
  Height = 14
  Length = 50
  Placement = pos=(-25,-46,22) rot=(0,0,1;0rad)
  Width = 13
FEATURE [Part::Cut] Cut012035015003002009024011
  Base = -> Cut012035007
  Refine = true
  Tool = -> Box084
FEATURE [Part::Box] Box085  label="Cube085"
  AttacherType = Attacher::AttachEngine3D
  Height = 14
  Length = 14
  Placement = pos=(25,-46,28) rot=(0,0,1;0rad)
  Width = 13
FEATURE [Part::Cut] Cut012035015003002009024012
  Base = -> Cut012035015003002009024011
  Refine = true
  Tool = -> Box085
FEATURE [Part::Box] Box086  label="Cube086"
  AttacherType = Attacher::AttachEngine3D
  Height = 10
  Length = 50
  Placement = pos=(-25,-46,4) rot=(0,0,1;0rad)
  Width = 13
FEATURE [Part::Box] Box087  label="Cube087"
  AttacherType = Attacher::AttachEngine3D
  Height = 14
  Length = 14.2
  Placement = pos=(24.8,16.8,22) rot=(0,0,1;0rad)
  Width = 10.2
FEATURE [Part::Box] Box088  label="Cube088"
  AttacherType = Attacher::AttachEngine3D
  Height = 14
  Length = 14.2
  Placement = pos=(24.8,-43,22) rot=(0,0,1;0rad)
  Width = 10.2
FEATURE [Part::MultiFuse] Fusion001005002004004005002010002003003003017007024041010023003003006006003006008013  label="Fusion-147"
  Refine = true
  Shapes = -> [Box083,Box088,Box087,Box082]
FEATURE [Part::Cut] Cut012035015003002009024015
  Base = -> Fusion001005002004004005002010002003003003017007024041010023003003006006003006008009
  Refine = true
  Tool = -> Fusion001005002004004005002010002003003003017007024041006
FEATURE [Part::Cut] Cut012035015003002009024016
  Base = -> Cut012035015003002009024015
  Refine = true
  Tool = -> Fusion001005002004004005002010002003003003017007024041010023003003006006003006008013
FEATURE [Part::Cylinder] Cylinder840  label="Cylinder910"
  Angle = 360
  AttacherType = Attacher::AttachEngine3D
  Height = 12
  Placement = pos=(-32,-45,29) rot=(-1,0,0;1.5708rad)
  Radius = 1.6
FEATURE [Part::Cylinder] Cylinder841  label="Cylinder911"
  Angle = 360
  AttacherType = Attacher::AttachEngine3D
  Height = 21
  Placement = pos=(-32,-41,29) rot=(-1,0,0;1.5708rad)
  Radius = 1.2
FEATURE [Part::Cylinder] Cylinder844  label="Cylinder914"
  Angle = 360
  AttacherType = Attacher::AttachEngine3D
  Height = 8
  Placement = pos=(25,-29,14) rot=(0,0,1;0rad)
  Radius = 1.6
FEATURE [Part::Cylinder] Cylinder846  label="Cylinder916"
  Angle = 360
  AttacherType = Attacher::AttachEngine3D
  Height = 8
  Placement = pos=(-25,-29,14) rot=(0,0,1;0rad)
  Radius = 1.6
FEATURE [Part::Cylinder] Cylinder847  label="Cylinder917"
  Angle = 360
  AttacherType = Attacher::AttachEngine3D
  Height = 13.5
  Placement = pos=(25,-29,14) rot=(0,0,1;0rad)
  Radius = 1.2
FEATURE [Part::Cylinder] Cylinder848  label="Cylinder918"
  Angle = 360
  AttacherType = Attacher::AttachEngine3D
  Height = 17
  Placement = pos=(-25,-29,14) rot=(0,0,1;0rad)
  Radius = 1.2
FEATURE [Part::MultiFuse] Fusion001005002004004005002010002003003003017007024041010023003003006006003006008017  label="Fusion-151"
  Placement = pos=(6,-9,0) rot=(0,0,1;0rad)
  Refine = true
  Shapes = -> [Cylinder848,Cylinder846]
FEATURE [Part::MultiFuse] Fusion001005002004004005002010002003003003017007024041010023003003006006003006008018  label="Fusion-152"
  Placement = pos=(-6,-9,0) rot=(0,0,1;0rad)
  Refine = true
  Shapes = -> [Cylinder844,Cylinder847]
FEATURE [Part::Cylinder] Cylinder849  label="Cylinder919"
  Angle = 360
  AttacherType = Attacher::AttachEngine3D
  Height = 3
  Placement = pos=(-32,-45,29) rot=(-1,0,0;1.5708rad)
  Radius = 2.8
FEATURE [Part::MultiFuse] Fusion001005002004004005002010002003003003017007024041010023003003006006003006008019  label="Fusion-153"
  Refine = true
  Shapes = -> [Cylinder840,Cylinder849,Cylinder841]
FEATURE [Part::Cylinder] Cylinder850  label="Cylinder920"
  Angle = 360
  AttacherType = Attacher::AttachEngine3D
  Height = 3
  Placement = pos=(-32,-45,29) rot=(-1,0,0;1.5708rad)
  Radius = 2.8
FEATURE [Part::Cylinder] Cylinder851  label="Cylinder921"
  Angle = 360
  AttacherType = Attacher::AttachEngine3D
  Height = 21
  Placement = pos=(-32,-41,29) rot=(-1,0,0;1.5708rad)
  Radius = 1.2
FEATURE [Part::Cylinder] Cylinder852  label="Cylinder922"
  Angle = 360
  AttacherType = Attacher::AttachEngine3D
  Height = 12
  Placement = pos=(-32,-45,29) rot=(-1,0,0;1.5708rad)
  Radius = 1.6
FEATURE [Part::MultiFuse] Fusion001005002004004005002010002003003003017007024041010023003003006006003006008020  label="Fusion-154"
  Placement = pos=(67,0,-5) rot=(0,0,1;0rad)
  Refine = true
  Shapes = -> [Cylinder852,Cylinder850,Cylinder851]
FEATURE [Part::Feature] Fusion001005002004004005002010002003003003017007024041010023003003006006003006008021001  label="Fusion-156"
  shape: bbox 72.6 x 25 x 17.8 mm, 24 faces, 4 solids (baked)
FEATURE [Part::Feature] Part__Mirroring005001  label="Fusion-157"
  Placement = pos=(0,-16,0) rot=(0,0,1;0rad)
  shape: bbox 72.6 x 25 x 17.8 mm, 24 faces, 4 solids (baked)
FEATURE [Part::MultiFuse] Fusion001005002004004005002010002003003003017007024041010023003003006006003006008021002  label="Fusion-158"
  Refine = true
  Shapes = -> [Part__Mirroring005001,Fusion001005002004004005002010002003003003017007024041010023003003006006003006008021001]
FEATURE [Part::Cut] Cut012035015003002009024017  label="rotation-lower-platform_"
  Base = -> Cut012035015003002009024016
  Refine = true
  Tool = -> Fusion001005002004004005002010002003003003017007024041010023003003006006003006008021002
FEATURE [Part::Feature] Face005
  Placement = pos=(0,0,-2) rot=(0,0,1;0rad)
  shape: bbox 93.5 x 193.6 x 2e-07 mm, 1 faces, 0 solids (baked)
FEATURE [Part::Extrusion] Extrude010
  Base = -> Face005
  Dir = (0,0,1)
  DirMode = 0
  FaceMakerClass = Part::FaceMakerBullseye
  LengthFwd = 2
  LengthRev = 0
  Solid = true
  Symmetric = false
FEATURE [Part::Cut] Cut012035015003002009024019
  Base = -> Fusion001005002004004005002010002003003003017007024041010023003003
  Refine = true
  Tool = -> Fusion001005002004004005002010002003003003017007024041010023003003006006003004
FEATURE [Part::Feature] Face006
  shape: bbox 16.5 x 193.6 x 16.5 mm, 1 faces, 0 solids (baked)
FEATURE [Part::Extrusion] Extrude011
  Base = -> Face006
  Dir = (0,0,-1)
  DirMode = 0
  FaceMakerClass = Part::FaceMakerBullseye
  LengthFwd = 2
  LengthRev = 0
  Solid = false
  Symmetric = false
FEATURE [Part::Feature] Cut012035015003002009024006001  label="Cut012035015003002009024020"
  shape: bbox 34.48 x 53 x 31.93 mm, 29 faces (baked)
FEATURE [Part::Feature] Part__Mirroring005002002002001  label="Cut012035015003002009024021 (Mirror #3)001"
  Placement = pos=(0,-16,0) rot=(0,0,1;0rad)
  shape: bbox 34.48 x 53 x 31.93 mm, 29 faces (baked)
FEATURE [Part::Box] Box089  label="Cube089"
  AttacherType = Attacher::AttachEngine3D
  Height = 29
  Length = 109
  Placement = pos=(-39,-43.2,23) rot=(0,0,1;0rad)
  Width = 70.4
FEATURE [Part::MultiFuse] Fusion001005002004004005002010002003003003017007024041010023003003006006003006008021003  label="Fusion-159"
  Refine = true
  Shapes = -> [Cut012035015003002009024006001,Part__Mirroring005002002002001]
FEATURE [Part::Cut] Cut012035015003002009024006002
  Base = -> Fusion001005002004004005002010002003003003017007024041010023003003006006003006008021003
  Refine = true
  Tool = -> Box089
FEATURE [Part::Box] Box090  label="Cube090"
  AttacherType = Attacher::AttachEngine3D
  Height = 29
  Length = 109
  Placement = pos=(-39,-43.2,23) rot=(0,0,1;0rad)
  Width = 70.4
FEATURE [Part::Feature] Cut012035015003002009024005001  label="Cut012035015003002009024006003"
  shape: bbox 85 x 53.18 x 10 mm, 49 faces (baked)
FEATURE [Part::Feature] Part__Mirroring005002002002002001  label="Cut012035015003002009024006004 (Mirror #3)001"
  Placement = pos=(0,-16,0) rot=(0,0,1;0rad)
  shape: bbox 85 x 53.18 x 10 mm, 49 faces (baked)
FEATURE [Part::MultiFuse] Fusion001005002004004005002010002003003003017007024041010023003003006006003006008021005  label="Fusion-161"
  Refine = true
  Shapes = -> [Part__Mirroring005002002002002001,Cut012035015003002009024005001]
FEATURE [Part::Cut] Cut012035015003002009024006003  label="Cut012035015003002009024006004"
  Base = -> Fusion001005002004004005002010002003003003017007024041010023003003006006003006008021005
  Refine = true
  Tool = -> Box090
FEATURE [Part::MultiFuse] Fusion001005002004004005002010002003003003017007024041010023003003006006003006008021006  label="upper-plate-front"
  Refine = true
  Shapes = -> [Cut012035015003002009024006003,Extrude010]
FEATURE [Part::Box] Box091  label="Cube091"
  AttacherType = Attacher::AttachEngine3D
  Height = 3
  Length = 2.2
  Placement = pos=(48,-96,49) rot=(0,0,1;0rad)
  Width = 176
FEATURE [Part::Box] Box092  label="Cube092"
  AttacherType = Attacher::AttachEngine3D
  Height = 14
  Length = 2.2
  Placement = pos=(64.8,-96,25) rot=(0,0,1;0rad)
  Width = 176
FEATURE [Part::MultiFuse] Fusion001005002004004005002010002003003003017007024041010023003003006006003006008021007  label="Fusion-162"
  Refine = true
  Shapes = -> [Box092,Box091]
FEATURE [Part::MultiFuse] Fusion001005002004004005002010002003003003017007024041010023003003006006003006008021008  label="Fusion-163"
  Refine = true
  Shapes = -> [Extrude011,Cut012035015003002009024006002]
FEATURE [Part::Cut] Cut012035015003002009024006004  label="upper-plate-front-slope_"
  Base = -> Fusion001005002004004005002010002003003003017007024041010023003003006006003006008021008
  Refine = true
  Tool = -> Fusion001005002004004005002010002003003003017007024041010023003003006006003006008021007
FEATURE [Part::Cylinder] Cylinder853  label="Cylinder923"
  Angle = 360
  AttacherType = Attacher::AttachEngine3D
  Height = 4
  Placement = pos=(0,0,0) rot=(-1,0,0;1.5708rad)
  Radius = 1.2
FEATURE [Part::Cone] Cone012
  Angle = 360
  AttacherType = Attacher::AttachEngine3D
  Height = 1
  Placement = pos=(0,0,0) rot=(-1,0,0;1.5708rad)
  Radius1 = 2
  Radius2 = 1.2
FEATURE [Part::Cylinder] Cylinder854  label="Cylinder924"
  Angle = 360
  AttacherType = Attacher::AttachEngine3D
  Height = 7
  Placement = pos=(0,0,0) rot=(-1,0,0;1.5708rad)
  Radius = 0.8
FEATURE [Part::MultiFuse] Fusion001005002004004005002010002003003003017007024041010023003003006006003006008021009  label="Fusion-164"
  Placement = pos=(52,-100,43.5) rot=(0,0,1;0rad)
  Refine = true
  Shapes = -> [Cone012,Cylinder853,Cylinder854]
FEATURE [Part::Cone] Cone013
  Angle = 360
  AttacherType = Attacher::AttachEngine3D
  Height = 1
  Placement = pos=(0,0,0) rot=(-1,0,0;1.5708rad)
  Radius1 = 2
  Radius2 = 1.2
FEATURE [Part::Cylinder] Cylinder855  label="Cylinder925"
  Angle = 360
  AttacherType = Attacher::AttachEngine3D
  Height = 4
  Placement = pos=(0,0,0) rot=(-1,0,0;1.5708rad)
  Radius = 1.2
FEATURE [Part::Cylinder] Cylinder856  label="Cylinder926"
  Angle = 360
  AttacherType = Attacher::AttachEngine3D
  Height = 7
  Placement = pos=(0,0,0) rot=(-1,0,0;1.5708rad)
  Radius = 0.8
FEATURE [Part::MultiFuse] Fusion001005002004004005002010002003003003017007024041010023003003006006003006008021010  label="Fusion-165"
  Placement = pos=(60,-100,35.5) rot=(0,0,1;0rad)
  Refine = true
  Shapes = -> [Cone013,Cylinder855,Cylinder856]
FEATURE [Part::MultiFuse] Fusion001005002004004005002010002003003003017007024041010023003003006006003006008021011  label="Fusion-166"
  Refine = true
  Shapes = -> [Fusion001005002004004005002010002003003003017007024041010023003003006006003006008021010,Fusion001005002004004005002010002003003003017007024041010023003003006006003006008021009]
FEATURE [Part::Cut] Cut012035015003002009024006005  label="border-front-left"
  Base = -> Cut012035015003002009024019
  Refine = true
  Tool = -> Fusion001005002004004005002010002003003003017007024041010023003003006006003006008021011
FEATURE [Part::Feature] Part__Mirroring005002002002002002001  label="border-front-right"
  Placement = pos=(0,-16,0) rot=(0,0,1;0rad)
  shape: bbox 84.57 x 5.5 x 55.62 mm, 28 faces (baked)
FEATURE [Part::Box] Box093  label="Cube093"
  AttacherType = Attacher::AttachEngine3D
  Height = 14
  Length = 10
  Placement = pos=(-39,-46,0) rot=(0,0,1;0rad)
  Width = 13
FEATURE [Part::Box] Box094  label="Cube094"
  AttacherType = Attacher::AttachEngine3D
  Height = 7
  Length = 15
  Placement = pos=(-39,-46,7) rot=(0,0,1;0rad)
  Width = 13
FEATURE [Part::Box] Box095  label="Cube095"
  AttacherType = Attacher::AttachEngine3D
  Height = 14
  Length = 15
  Placement = pos=(-39,-36,0) rot=(0,0,1;0rad)
  Width = 3
FEATURE [Part::Box] Box096  label="Cube096"
  AttacherType = Attacher::AttachEngine3D
  Height = 7
  Length = 15
  Placement = pos=(-39,-43.25,0) rot=(0,0,1;0rad)
  Width = 7.5
FEATURE [Part::MultiFuse] Fusion001005002004004005002010002003003003017007024041010023003003006006003006008021012  label="Fusion-167"
  Refine = true
  Shapes = -> [Box093,Box094,Box095]
FEATURE [Part::Cut] Cut012035015003002009024006006
  Base = -> Fusion001005002004004005002010002003003003017007024041010023003003006006003006008021012
  Refine = true
  Tool = -> Box096
FEATURE [Part::Fillet] Fillet001016
  Base = -> Cut012035015003002009024006006
  Edges = 3 edges r=3: [Edge4,Edge13,Edge22]
FEATURE [Part::Chamfer] Chamfer007018
  Base = -> Fillet001016
  Edges = 1 edges r=7: [Edge24]
FEATURE [Part::Cylinder] Cylinder857  label="Cylinder927"
  Angle = 360
  AttacherType = Attacher::AttachEngine3D
  Height = 7.5
  Placement = pos=(-34.1,0,3.25) rot=(-1,0,0;1.5708rad)
  Radius = 1.5
FEATURE [Part::Cylinder] Cylinder858  label="Cylinder928"
  Angle = 360
  AttacherType = Attacher::AttachEngine3D
  Height = 15
  Placement = pos=(-34.1,0,3.25) rot=(-1,0,0;1.5708rad)
  Radius = 1.2
FEATURE [Part::MultiFuse] Fusion001005002004004005002010002003003003017007024041010023003003006006003006008021013  label="Fusion-168"
  Placement = pos=(0,-47,0) rot=(0,0,1;0rad)
  Refine = true
  Shapes = -> [Cylinder858,Cylinder857]
FEATURE [Part::Cut] Cut012035015003002009024006007
  Base = -> Chamfer007018
  Refine = true
  Tool = -> Fusion001005002004004005002010002003003003017007024041010023003003006006003006008021013
FEATURE [Part::Fillet] Fillet001017
  Base = -> Cut012035015003002009024006007
  Edges = 1 edges r=3: [Edge13]
FEATURE [Part::Box] Box098  label="Cube098"
  AttacherType = Attacher::AttachEngine3D
  Height = 7
  Length = 14
  Placement = pos=(25,-46,7) rot=(0,0,1;0rad)
  Width = 13
FEATURE [Part::Box] Box099  label="Cube099"
  AttacherType = Attacher::AttachEngine3D
  Height = 11
  Length = 15
  Placement = pos=(25,-36,-4) rot=(0,0,1;0rad)
  Width = 3
FEATURE [Part::Box] Box100  label="Cube100"
  AttacherType = Attacher::AttachEngine3D
  Height = 18
  Length = 10
  Placement = pos=(30,-46,-4) rot=(0,0,1;0rad)
  Width = 13
FEATURE [Part::Box] Box101  label="Cube101"
  AttacherType = Attacher::AttachEngine3D
  Height = 11
  Length = 15
  Placement = pos=(25,-43.25,-4) rot=(0,0,1;0rad)
  Width = 7.5
FEATURE [Part::MultiFuse] Fusion001005002004004005002010002003003003017007024041010023003003006006003006008021014  label="Fusion-169"
  Refine = true
  Shapes = -> [Box100,Box098,Box099]
FEATURE [Part::Cut] Cut012035015003002009024006008
  Base = -> Fusion001005002004004005002010002003003003017007024041010023003003006006003006008021014
  Refine = true
  Tool = -> Box101
FEATURE [Part::Fillet] Fillet001019
  Base = -> Cut012035015003002009024006008
  Edges = 3 edges r=3: [Edge4,Edge13,Edge16]
FEATURE [Part::Chamfer] Chamfer007019
  Base = -> Fillet001019
  Edges = 1 edges: [Edge30 r1=11 r2=6]
FEATURE [Part::Cylinder] Cylinder859  label="Cylinder929"
  Angle = 360
  AttacherType = Attacher::AttachEngine3D
  Height = 13
  Placement = pos=(35,-46,-1.55) rot=(-1,0,0;1.5708rad)
  Radius = 1
FEATURE [Part::Fillet] Fillet001020
  Base = -> Chamfer007019
  Edges = 1 edges r=3: [Edge12]
FEATURE [Part::Cylinder] Cylinder862  label="Cylinder932"
  Angle = 360
  AttacherType = Attacher::AttachEngine3D
  Height = 13
  Placement = pos=(33,-46,5) rot=(-1,0,0;1.5708rad)
  Radius = 4
FEATURE [Part::Cut] Cut012035015003002009024006012
  Base = -> Fillet001020
  Placement = pos=(-1,0,0) rot=(0,0,1;0rad)
  Refine = true
  Tool = -> Cylinder859
FEATURE [Part::Box] Box105  label="Cube105"
  AttacherType = Attacher::AttachEngine3D
  Height = 2
  Length = 8
  Placement = pos=(29,-43.25,5) rot=(0,0,1;0rad)
  Width = 7.5
FEATURE [Part::MultiFuse] Fusion001005002004004005002010002003003003017007024041010023003003006006003006008021016  label="Fusion-171"
  Refine = true
  Shapes = -> [Box105,Cylinder862,Cut012035015003002009024006012]
FEATURE [Part::MultiFuse] Fusion001005002004004005002010002003003003017007024041010023003003006006003006008021017  label="Fusion-172"
  Refine = true
  Shapes = -> [Fusion001005002004004005002010002003003003017007024041010023003003006006003006008021016,Fillet001017]
FEATURE [Part::Box] Box108  label="Cube108"
  AttacherType = Attacher::AttachEngine3D
  Height = 10
  Length = 50
  Placement = pos=(-25,-46,4) rot=(0,0,1;0rad)
  Width = 13
FEATURE [Part::Cut] Cut012035015003002009024006015
  Base = -> Fusion001005002004004005002010002003003003017007024041010023003003006006003006008021017
  Placement = pos=(450,0,0) rot=(0,0,1;0rad)
  Refine = true
  Tool = -> Box108
FEATURE [Part::Cylinder] Cylinder863  label="Cylinder933"
  Angle = 360
  AttacherType = Attacher::AttachEngine3D
  Height = 12
  Placement = pos=(-32,-45,29) rot=(-1,0,0;1.5708rad)
  Radius = 1.6
FEATURE [Part::Cylinder] Cylinder864  label="Cylinder934"
  Angle = 360
  AttacherType = Attacher::AttachEngine3D
  Height = 21
  Placement = pos=(-32,-41,29) rot=(-1,0,0;1.5708rad)
  Radius = 1.2
FEATURE [Part::Cylinder] Cylinder865  label="Cylinder935"
  Angle = 360
  AttacherType = Attacher::AttachEngine3D
  Height = 8
  Placement = pos=(25,-29,14) rot=(0,0,1;0rad)
  Radius = 1.6
FEATURE [Part::Cylinder] Cylinder866  label="Cylinder936"
  Angle = 360
  AttacherType = Attacher::AttachEngine3D
  Height = 8
  Placement = pos=(-25,-29,14) rot=(0,0,1;0rad)
  Radius = 1.6
FEATURE [Part::Cylinder] Cylinder867  label="Cylinder937"
  Angle = 360
  AttacherType = Attacher::AttachEngine3D
  Height = 13.5
  Placement = pos=(25,-29,14) rot=(0,0,1;0rad)
  Radius = 1.2
FEATURE [Part::Cylinder] Cylinder868  label="Cylinder938"
  Angle = 360
  AttacherType = Attacher::AttachEngine3D
  Height = 17
  Placement = pos=(-25,-29,14) rot=(0,0,1;0rad)
  Radius = 1.2
FEATURE [Part::MultiFuse] Fusion001005002004004005002010002003003003017007024041010023003003006006003006008021019  label="Fusion-174"
  Placement = pos=(6,-9,0) rot=(0,0,1;0rad)
  Refine = true
  Shapes = -> [Cylinder868,Cylinder866]
FEATURE [Part::MultiFuse] Fusion001005002004004005002010002003003003017007024041010023003003006006003006008021020  label="Fusion-175"
  Placement = pos=(-6,-9,0) rot=(0,0,1;0rad)
  Refine = true
  Shapes = -> [Cylinder865,Cylinder867]
FEATURE [Part::Cylinder] Cylinder869  label="Cylinder939"
  Angle = 360
  AttacherType = Attacher::AttachEngine3D
  Height = 3
  Placement = pos=(-32,-45,29) rot=(-1,0,0;1.5708rad)
  Radius = 2.8
FEATURE [Part::MultiFuse] Fusion001005002004004005002010002003003003017007024041010023003003006006003006008021021  label="Fusion-176"
  Refine = true
  Shapes = -> [Cylinder863,Cylinder869,Cylinder864]
FEATURE [Part::Cylinder] Cylinder870  label="Cylinder940"
  Angle = 360
  AttacherType = Attacher::AttachEngine3D
  Height = 3
  Placement = pos=(-32,-45,29) rot=(-1,0,0;1.5708rad)
  Radius = 2.8
FEATURE [Part::Cylinder] Cylinder871  label="Cylinder941"
  Angle = 360
  AttacherType = Attacher::AttachEngine3D
  Height = 21
  Placement = pos=(-32,-41,29) rot=(-1,0,0;1.5708rad)
  Radius = 1.2
FEATURE [Part::Cylinder] Cylinder872  label="Cylinder942"
  Angle = 360
  AttacherType = Attacher::AttachEngine3D
  Height = 12
  Placement = pos=(-32,-45,29) rot=(-1,0,0;1.5708rad)
  Radius = 1.6
FEATURE [Part::MultiFuse] Fusion001005002004004005002010002003003003017007024041010023003003006006003006008021022  label="Fusion-177"
  Placement = pos=(67,0,-5) rot=(0,0,1;0rad)
  Refine = true
  Shapes = -> [Cylinder872,Cylinder870,Cylinder871]
FEATURE [Part::MultiFuse] Fusion001005002004004005002010002003003003017007024041010023003003006006003006008021023  label="Fusion-178"
  Refine = true
  Shapes = -> [Fusion001005002004004005002010002003003003017007024041010023003003006006003006008021019,Fusion001005002004004005002010002003003003017007024041010023003003006006003006008021022,Fusion001005002004004005002010002003003003017007024041010023003003006006003006008021021,Fusion001005002004004005002010002003003003017007024041010023003003006006003006008021020]
FEATURE [Part::Box] Box110  label="Cube110"
  AttacherType = Attacher::AttachEngine3D
  Height = 10
  Length = 78
  Placement = pos=(411,-43.2,25) rot=(0,0,1;0rad)
  Width = 10.2
FEATURE [Part::Box] Box111  label="Cube111"
  AttacherType = Attacher::AttachEngine3D
  Height = 11
  Length = 50
  Placement = pos=(425,-43,14) rot=(0,0,1;0rad)
  Width = 10
FEATURE [Part::Box] Box112  label="Cube112"
  AttacherType = Attacher::AttachEngine3D
  Height = 21
  Length = 14
  Placement = pos=(411,-46,14) rot=(0,0,1;0rad)
  Width = 13
FEATURE [Part::Box] Box113  label="Cube113"
  AttacherType = Attacher::AttachEngine3D
  Height = 21
  Length = 14
  Placement = pos=(475,-46,14) rot=(0,0,1;0rad)
  Width = 13
FEATURE [Part::MultiFuse] Fusion001005002004004005002010002003003003017007024041010023003003006006003006008021024  label="Fusion-179"
  Refine = true
  Shapes = -> [Box112,Box111,Box113]
FEATURE [Part::Cut] Cut012035015003002009024006016
  Base = -> Fusion001005002004004005002010002003003003017007024041010023003003006006003006008021024
  Refine = true
  Tool = -> Box110
FEATURE [Part::MultiFuse] Fusion001005002004004005002010002003003003017007024041010023003003006006003006008021025  label="Fusion-180"
  Refine = true
  Shapes = -> [Cut012035015003002009024006015,Cut012035015003002009024006016]
FEATURE [Part::Cylinder] Cylinder873  label="Cylinder943"
  Angle = 360
  AttacherType = Attacher::AttachEngine3D
  Height = 24.5
  Placement = pos=(70,-43,30) rot=(-1,0,0;1.5708rad)
  Radius = 1.7
FEATURE [Part::Cylinder] Cylinder874  label="Cylinder944"
  Angle = 360
  AttacherType = Attacher::AttachEngine3D
  Height = 24.5
  Placement = pos=(90,-43,30) rot=(-1,0,0;1.5708rad)
  Radius = 1.7
FEATURE [Part::Cylinder] Cylinder875  label="Cylinder945"
  Angle = 360
  AttacherType = Attacher::AttachEngine3D
  Height = 24.5
  Placement = pos=(110,-43,30) rot=(-1,0,0;1.5708rad)
  Radius = 1.7
FEATURE [Part::MultiFuse] Fusion001005002004004005002010002003003003017007024041010023003003006006003006008021026  label="Fusion-181"
  Refine = true
  Shapes = -> [Cylinder873,Cylinder875,Cylinder874]
FEATURE [Part::Box] Box114  label="Cube114"
  AttacherType = Attacher::AttachEngine3D
  Height = 10.6
  Length = 50
  Placement = pos=(65,-33,24.7) rot=(0,0,1;0rad)
  Width = 10
FEATURE [Part::Box] Box115  label="Cube115"
  AttacherType = Attacher::AttachEngine3D
  Height = 14
  Length = 50
  Placement = pos=(65,-37,23) rot=(0,0,1;0rad)
  Width = 10
FEATURE [Part::Cut] Cut012035015003002009024006017
  Base = -> Box115
  Refine = true
  Tool = -> Box114
FEATURE [Part::Cut] Cut012035015003002009024006018  label="frame-front-HOLES"
  Base = -> Cut012035015003002009024006017
  Refine = true
  Tool = -> Fusion001005002004004005002010002003003003017007024041010023003003006006003006008021026
FEATURE [Part::Cylinder] Cylinder876  label="Cylinder946"
  Angle = 360
  AttacherType = Attacher::AttachEngine3D
  Height = 11
  Placement = pos=(431,-38,14) rot=(0,0,1;0rad)
  Radius = 1.6
FEATURE [Part::Cylinder] Cylinder877  label="Cylinder947"
  Angle = 360
  AttacherType = Attacher::AttachEngine3D
  Height = 11
  Placement = pos=(469,-38,14) rot=(0,0,1;0rad)
  Radius = 1.6
FEATURE [Part::Cylinder] Cylinder878  label="Cylinder948"
  Angle = 360
  AttacherType = Attacher::AttachEngine3D
  Height = 11
  Placement = pos=(418,-49,30) rot=(-1,0,0;1.5708rad)
  Radius = 1.6
FEATURE [Part::Cylinder] Cylinder879  label="Cylinder949"
  Angle = 360
  AttacherType = Attacher::AttachEngine3D
  Height = 4.4
  Placement = pos=(418,-49,30) rot=(-1,0,0;1.5708rad)
  Radius = 3.2
FEATURE [Part::MultiFuse] Fusion001005002004004005002010002003003003017007024041010023003003006006003006008021027  label="Fusion-182"
  Refine = true
  Shapes = -> [Cylinder879,Cylinder878]
FEATURE [Part::Cylinder] Cylinder880  label="Cylinder950"
  Angle = 360
  AttacherType = Attacher::AttachEngine3D
  Height = 11
  Placement = pos=(418,-49,30) rot=(-1,0,0;1.5708rad)
  Radius = 1.6
FEATURE [Part::Cylinder] Cylinder881  label="Cylinder951"
  Angle = 360
  AttacherType = Attacher::AttachEngine3D
  Height = 4.4
  Placement = pos=(418,-49,30) rot=(-1,0,0;1.5708rad)
  Radius = 3.2
FEATURE [Part::MultiFuse] Fusion001005002004004005002010002003003003017007024041010023003003006006003006008021028  label="Fusion-183"
  Placement = pos=(64,0,0) rot=(0,0,1;0rad)
  Refine = true
  Shapes = -> [Cylinder881,Cylinder880]
FEATURE [Part::MultiFuse] Fusion001005002004004005002010002003003003017007024041010023003003006006003006008021029  label="Fusion-184"
  Refine = true
  Shapes = -> [Cylinder876,Fusion001005002004004005002010002003003003017007024041010023003003006006003006008021028,Cylinder877,Fusion001005002004004005002010002003003003017007024041010023003003006006003006008021027]
FEATURE [Part::Cylinder] Cylinder882  label="Cylinder952"
  Angle = 360
  AttacherType = Attacher::AttachEngine3D
  Height = 11
  Placement = pos=(418,-49,30) rot=(-1,0,0;1.5708rad)
  Radius = 1.7
FEATURE [Part::Cylinder] Cylinder883  label="Cylinder953"
  Angle = 360
  AttacherType = Attacher::AttachEngine3D
  Height = 11
  Placement = pos=(431,-38,14) rot=(0,0,1;0rad)
  Radius = 1.7
FEATURE [Part::Cylinder] Cylinder884  label="Cylinder954"
  Angle = 360
  AttacherType = Attacher::AttachEngine3D
  Height = 1
  Placement = pos=(418,-49,30) rot=(-1,0,0;1.5708rad)
  Radius = 3.2
FEATURE [Part::Cylinder] Cylinder885  label="Cylinder955"
  Angle = 360
  AttacherType = Attacher::AttachEngine3D
  Height = 11
  Placement = pos=(469,-38,14) rot=(0,0,1;0rad)
  Radius = 1.7
FEATURE [Part::Cylinder] Cylinder886  label="Cylinder956"
  Angle = 360
  AttacherType = Attacher::AttachEngine3D
  Height = 11
  Placement = pos=(418,-49,30) rot=(-1,0,0;1.5708rad)
  Radius = 1.7
FEATURE [Part::MultiFuse] Fusion001005002004004005002010002003003003017007024041010023003003006006003006008021030  label="Fusion-185"
  Placement = pos=(64,0,0) rot=(0,0,1;0rad)
  Refine = true
  Shapes = -> [Cylinder884,Cylinder886]
FEATURE [Part::Cylinder] Cylinder887  label="Cylinder957"
  Angle = 360
  AttacherType = Attacher::AttachEngine3D
  Height = 1
  Placement = pos=(418,-49,30) rot=(-1,0,0;1.5708rad)
  Radius = 3.2
FEATURE [Part::MultiFuse] Fusion001005002004004005002010002003003003017007024041010023003003006006003006008021032  label="Fusion-187"
  Refine = true
  Shapes = -> [Cylinder887,Cylinder882]
FEATURE [Part::Box] Box116  label="Cube116"
  AttacherType = Attacher::AttachEngine3D
  Height = 10.6
  Length = 78
  Placement = pos=(411,-43.3,24.7) rot=(0,0,1;0rad)
  Width = 10.6
FEATURE [Part::Box] Box117  label="Cube117"
  AttacherType = Attacher::AttachEngine3D
  Height = 13
  Length = 78
  Placement = pos=(411,-46,22) rot=(0,0,1;0rad)
  Width = 15
FEATURE [Part::Cut] Cut012035015003002009024006020
  Base = -> Box117
  Refine = true
  Tool = -> Box116
FEATURE [Part::MultiFuse] Fusion001005002004004005002010002003003003017007024041010023003003006006003006008021033  label="Fusion-188"
  Refine = true
  Shapes = -> [Cylinder883,Fusion001005002004004005002010002003003003017007024041010023003003006006003006008021032,Cylinder885,Fusion001005002004004005002010002003003003017007024041010023003003006006003006008021030]
FEATURE [Part::Cut] Cut012035015003002009024006021  label="frame-rear-axle-HOLES"
  Base = -> Cut012035015003002009024006020
  Refine = true
  Tool = -> Fusion001005002004004005002010002003003003017007024041010023003003006006003006008021033
FEATURE [Part::Cylinder] Cylinder888  label="Cylinder958"
  Angle = 360
  AttacherType = Attacher::AttachEngine3D
  Height = 182
  Placement = pos=(490,-99,30) rot=(-1,0,0;1.5708rad)
  Radius = 2.5
FEATURE [Part::Box] Box118  label="Cube118"
  AttacherType = Attacher::AttachEngine3D
  Height = 10
  Length = 50
  Placement = pos=(445,-33,25) rot=(0,0,1;0rad)
  Width = 25
FEATURE [Part::Box] Box123  label="Cube123"
  AttacherType = Attacher::AttachEngine3D
  Height = 5
  Length = 11
  Placement = pos=(-51.5,19.5,28.5) rot=(0,0,1;0rad)
  Width = 5
FEATURE [Part::Box] Box124  label="Cube124"
  AttacherType = Attacher::AttachEngine3D
  Height = 5
  Length = 11
  Placement = pos=(-51.5,-40.5,28.5) rot=(0,0,1;0rad)
  Width = 5
FEATURE [Part::Box] Box125  label="Cube125"
  AttacherType = Attacher::AttachEngine3D
  Height = 5
  Length = 106
  Placement = pos=(-51.5,24.5,28.5) rot=(0,0,1;3.42084rad)
  Width = 5
FEATURE [Part::Box] Box127  label="Cube127"
  AttacherType = Attacher::AttachEngine3D
  Height = 5
  Length = 14
  Placement = pos=(-160,-12,28.5) rot=(0,0,1;0rad)
  Width = 8
FEATURE [Part::Box] Box128  label="Cube128"
  AttacherType = Attacher::AttachEngine3D
  Height = 5
  Length = 5
  Placement = pos=(-68.5,-34.5,28.5) rot=(0,0,1;0rad)
  Width = 53
FEATURE [Part::Box] Box129  label="Cube129"
  AttacherType = Attacher::AttachEngine3D
  Height = 5
  Length = 10
  Placement = pos=(-119.5,-28.5,28.5) rot=(0,0,1;0rad)
  Width = 33
FEATURE [Part::Chamfer] Chamfer007023
  Base = -> Box129
  Edges = 2 edges: [Edge1 r1=3 r2=5,Edge3 r1=3 r2=5]
  Placement = pos=(17,4,0) rot=(0,0,1;0rad)
FEATURE [Part::Cylinder] Cylinder897  label="Cylinder967"
  Angle = 360
  AttacherType = Attacher::AttachEngine3D
  Height = 10
  Placement = pos=(-66,-34.5,24) rot=(0,0,1;0rad)
  Radius = 0.8
FEATURE [Part::Cylinder] Cylinder898  label="Cylinder968"
  Angle = 360
  AttacherType = Attacher::AttachEngine3D
  Height = 10
  Placement = pos=(-66,-28.5,24) rot=(0,0,1;0rad)
  Radius = 0.8
FEATURE [Part::MultiFuse] Fusion001005002004004005002010002003003003017007024041010023003003006006003006008021041  label="Fusion-196"
  Refine = true
  Shapes = -> [Cylinder897,Cylinder898]
FEATURE [Part::Cylinder] Cylinder899  label="Cylinder969"
  Angle = 360
  AttacherType = Attacher::AttachEngine3D
  Height = 10
  Placement = pos=(-66,-34.5,24) rot=(0,0,1;0rad)
  Radius = 0.8
FEATURE [Part::Cylinder] Cylinder900  label="Cylinder970"
  Angle = 360
  AttacherType = Attacher::AttachEngine3D
  Height = 10
  Placement = pos=(-66,-28.5,24) rot=(0,0,1;0rad)
  Radius = 0.8
FEATURE [Part::MultiFuse] Fusion001005002004004005002010002003003003017007024041010023003003006006003006008021042  label="Fusion-197"
  Placement = pos=(0,47,0) rot=(0,0,1;0rad)
  Refine = true
  Shapes = -> [Cylinder899,Cylinder900]
FEATURE [Part::Cylinder] Cylinder901  label="Cylinder971"
  Angle = 360
  AttacherType = Attacher::AttachEngine3D
  Height = 25
  Placement = pos=(-161,-8,30.75) rot=(0,1,0;1.5708rad)
  Radius = 1.5
FEATURE [Part::Cylinder] Cylinder902  label="Cylinder972"
  Angle = 360
  AttacherType = Attacher::AttachEngine3D
  Height = 65
  Placement = pos=(-44.1,-40.5,30.75) rot=(-1,0,0;1.5708rad)
  Radius = 1.5
FEATURE [Part::MultiFuse] Fusion001005002004004005002010002003003003017007024041010023003003006006003006008021043  label="Fusion-198"
  Placement = pos=(0,0,-8) rot=(0,0,1;0rad)
  Refine = true
  Shapes = -> [Fusion001005002004004005002010002003003003017007024041010023003003006006003006008021041,Fusion001005002004004005002010002003003003017007024041010023003003006006003006008021042,Cylinder901,Cylinder902]
FEATURE [Part::Feature] Part__Mirroring005002002002002002002002001  label="Cube130 (Mirror #3)001"
  Placement = pos=(0,-16,0) rot=(0,0,1;0rad)
  shape: bbox 103.3 x 34.02 x 5 mm, 6 faces (baked)
FEATURE [Part::MultiFuse] Fusion001005002004004005002010002003003003017007024041010023003003006006003006008021044  label="Fusion-199"
  Placement = pos=(0,0,-8) rot=(0,0,1;0rad)
  Refine = true
  Shapes = -> [Box123,Chamfer007023,Part__Mirroring005002002002002002002002001,Box127,Box128,Box125,Box124]
FEATURE [Part::Cylinder] Cylinder903  label="Cylinder973"
  Angle = 360
  AttacherType = Attacher::AttachEngine3D
  Height = 182
  Placement = pos=(403,-99,30) rot=(-1,0,0;1.5708rad)
  Radius = 2.5
FEATURE [Part::Cylinder] Cylinder904  label="Cylinder974"
  Angle = 360
  AttacherType = Attacher::AttachEngine3D
  Height = 182
  Placement = pos=(317,-99,30) rot=(-1,0,0;1.5708rad)
  Radius = 2.5
FEATURE [Part::Cylinder] Cylinder905  label="Cylinder975"
  Angle = 360
  AttacherType = Attacher::AttachEngine3D
  Height = 182
  Placement = pos=(231,-99,30) rot=(-1,0,0;1.5708rad)
  Radius = 2.5
FEATURE [Part::Cylinder] Cylinder906  label="Cylinder976"
  Angle = 360
  AttacherType = Attacher::AttachEngine3D
  Height = 184
  Placement = pos=(317,-100,30) rot=(-1,0,0;1.5708rad)
  Radius = 1.65
FEATURE [Part::Cylinder] Cylinder907  label="Cylinder977"
  Angle = 360
  AttacherType = Attacher::AttachEngine3D
  Height = 184
  Placement = pos=(231,-100,30) rot=(-1,0,0;1.5708rad)
  Radius = 1.65
FEATURE [Part::Cylinder] Cylinder908  label="Cylinder978"
  Angle = 360
  AttacherType = Attacher::AttachEngine3D
  Height = 184
  Placement = pos=(403,-100,30) rot=(-1,0,0;1.5708rad)
  Radius = 1.65
FEATURE [Part::Cylinder] Cylinder911  label="Cylinder981"
  Angle = 360
  AttacherType = Attacher::AttachEngine3D
  Height = 184
  Placement = pos=(414,-100,30) rot=(-1,0,0;1.5708rad)
  Radius = 1.65
FEATURE [Part::Cylinder] Cylinder912  label="Cylinder982"
  Angle = 360
  AttacherType = Attacher::AttachEngine3D
  Height = 184
  Placement = pos=(392,-100,30) rot=(-1,0,0;1.5708rad)
  Radius = 1.65
FEATURE [Part::Cylinder] Cylinder913  label="Cylinder983"
  Angle = 360
  AttacherType = Attacher::AttachEngine3D
  Height = 184
  Placement = pos=(328,-100,30) rot=(-1,0,0;1.5708rad)
  Radius = 1.65
FEATURE [Part::Cylinder] Cylinder914  label="Cylinder984"
  Angle = 360
  AttacherType = Attacher::AttachEngine3D
  Height = 184
  Placement = pos=(306,-100,30) rot=(-1,0,0;1.5708rad)
  Radius = 1.65
FEATURE [Part::Cylinder] Cylinder915  label="Cylinder985"
  Angle = 360
  AttacherType = Attacher::AttachEngine3D
  Height = 184
  Placement = pos=(242,-100,30) rot=(-1,0,0;1.5708rad)
  Radius = 1.65
FEATURE [Part::Box] Box133  label="Cube133"
  AttacherType = Attacher::AttachEngine3D
  Height = 10
  Length = 193
  Placement = pos=(226,-46,25) rot=(0,0,1;0rad)
  Width = 3
FEATURE [Part::MultiFuse] Fusion001005002004004005002010002003003003017007024041010023003003006006003006008021045  label="Fusion-200"
  Refine = true
  Shapes = -> [Cylinder906,Cylinder907,Cylinder908,Cylinder911,Cylinder912,Cylinder913,Cylinder914,Cylinder915]
FEATURE [Part::Cut] Cut
  Base = -> Box133
  Placement = pos=(0,-8,68) rot=(1,0,0;1.5708rad)
  Refine = true
  Tool = -> Fusion001005002004004005002010002003003003017007024041010023003003006006003006008021045
FEATURE [Part::Cylinder] Cylinder
  Angle = 360
  AttacherType = Attacher::AttachEngine3D
  Height = 30
  Placement = pos=(255,-38,0) rot=(0,0,1;0rad)
  Radius = 1.65
FEATURE [Part::Cylinder] Cylinder916  label="Cylinder986"
  Angle = 360
  AttacherType = Attacher::AttachEngine3D
  Height = 30
  Placement = pos=(293,-38,0) rot=(0,0,1;0rad)
  Radius = 1.65
FEATURE [Part::Cylinder] Cylinder917  label="Cylinder987"
  Angle = 360
  AttacherType = Attacher::AttachEngine3D
  Height = 30
  Placement = pos=(341,-38,0) rot=(0,0,1;0rad)
  Radius = 1.65
FEATURE [Part::Cylinder] Cylinder918  label="Cylinder988"
  Angle = 360
  AttacherType = Attacher::AttachEngine3D
  Height = 30
  Placement = pos=(379,-38,0) rot=(0,0,1;0rad)
  Radius = 1.65
FEATURE [Part::MultiFuse] Fusion001005002004004005002010002003003003017007024041010023003003006006003006008021046  label="Fusion-201"
  Refine = true
  Shapes = -> [Cylinder,Cylinder917,Cylinder916,Cylinder918]
FEATURE [Part::Cut] Cut012035015003002009024006019003  label="leafspring-attach-rear-HOLESTOOL"
  Base = -> Cut
  Refine = true
  Tool = -> Fusion001005002004004005002010002003003003017007024041010023003003006006003006008021046
FEATURE [Part::Box] Box134  label="Cube134"
  AttacherType = Attacher::AttachEngine3D
  Height = 17.6
  Length = 8
  Placement = pos=(547,-96,2.5) rot=(0,0,1;0rad)
  Width = 88
FEATURE [Part::Cylinder] Cylinder919  label="Cylinder989"
  Angle = 360
  AttacherType = Attacher::AttachEngine3D
  Height = 59
  Placement = pos=(560,-101,10.8) rot=(-1,0,0;1.5708rad)
  Radius = 1.5
FEATURE [Part::Box] Box138  label="Cube138"
  AttacherType = Attacher::AttachEngine3D
  Height = 15
  Length = 1
  Placement = pos=(554,-101,2.5) rot=(0,0,1;0rad)
  Width = 5
FEATURE [Part::Feature] Face010
  shape: bbox 74.7 x 2e-07 x 37.45 mm, 1 faces, 0 solids (baked)
FEATURE [Part::Feature] Face011
  shape: bbox 76.16 x 2e-07 x 40.23 mm, 1 faces, 0 solids (baked)
FEATURE [Part::Extrusion] Extrude013
  Base = -> Face010
  Dir = (0,1,0)
  DirMode = 0
  FaceMakerClass = Part::FaceMakerBullseye
  LengthFwd = 1
  LengthRev = 0
  Solid = true
  Symmetric = false
FEATURE [Part::Extrusion] Extrude014
  Base = -> Face011
  Dir = (0,1,0)
  DirMode = 0
  FaceMakerClass = Part::FaceMakerBullseye
  LengthFwd = 5
  LengthRev = 0
  Solid = true
  Symmetric = false
FEATURE [Part::Cut] Cut012035015003002009024006019004
  Base = -> Extrude013
  Refine = true
  Tool = -> Box138
FEATURE [Part::Cylinder] Cylinder920  label="Cylinder990"
  Angle = 46
  AttacherType = Attacher::AttachEngine3D
  Height = 7
  Placement = pos=(0,0,0) rot=(0,0,-1;1.97222rad)
  Radius = 109
FEATURE [Part::Cylinder] Cylinder921  label="Cylinder991"
  Angle = 32
  AttacherType = Attacher::AttachEngine3D
  Height = 7
  Placement = pos=(0,0,0) rot=(0,0,-1;1.85005rad)
  Radius = 109
FEATURE [Part::Cylinder] Cylinder922  label="Cylinder992"
  Angle = 41
  AttacherType = Attacher::AttachEngine3D
  Height = 7
  Placement = pos=(0,0,0) rot=(0,0,-1;1.90241rad)
  Radius = 108
FEATURE [Part::Cylinder] Cylinder923  label="Cylinder993"
  Angle = 26
  AttacherType = Attacher::AttachEngine3D
  Height = 7
  Placement = pos=(0,0,0) rot=(0,0,-1;1.79769rad)
  Radius = 110
FEATURE [Part::Cut] Cut012035015003002009024006019007
  Base = -> Cylinder923
  Placement = pos=(0,-1,0) rot=(0,0,1;0rad)
  Refine = true
  Tool = -> Cylinder920
FEATURE [Part::Cylinder] Cylinder924  label="Cylinder994"
  Angle = 360
  AttacherType = Attacher::AttachEngine3D
  Height = 7
  Placement = pos=(-34.1,-43,15.25) rot=(-1,0,0;1.5708rad)
  Radius = 3.5
FEATURE [Part::Box] Box139  label="Cube139"
  AttacherType = Attacher::AttachEngine3D
  Height = 4.3
  Length = 14
  Placement = pos=(-7,-43,-9) rot=(0,0,1;0rad)
  Width = 7
FEATURE [Part::Cylinder] Cylinder925  label="Cylinder995"
  Angle = 46
  AttacherType = Attacher::AttachEngine3D
  Height = 7
  Placement = pos=(0,0,0) rot=(0,0,-1;1.97222rad)
  Radius = 108
FEATURE [Part::Cut] Cut012035015003002009024006019008
  Base = -> Cylinder921
  Placement = pos=(0,-0.5,0) rot=(0,0,1;0rad)
  Refine = true
  Tool = -> Cylinder925
FEATURE [Part::Cylinder] Cylinder926  label="Cylinder996"
  Angle = 46
  AttacherType = Attacher::AttachEngine3D
  Height = 7
  Placement = pos=(0,0,0) rot=(0,0,-1;1.97222rad)
  Radius = 107
FEATURE [Part::Cut] Cut012035015003002009024006019006
  Base = -> Cylinder922
  Refine = true
  Tool = -> Cylinder926
FEATURE [Part::MultiFuse] Fusion001005002004004005002010002003003003017007024041010023003003006006003006008021047  label="Fusion-202"
  Placement = pos=(0,-36,114) rot=(1,0,0;1.5708rad)
  Refine = true
  Shapes = -> [Cut012035015003002009024006019007,Cut012035015003002009024006019008,Cut012035015003002009024006019006]
FEATURE [Part::Cylinder] Cylinder927  label="Cylinder997"
  Angle = 360
  AttacherType = Attacher::AttachEngine3D
  Height = 7
  Placement = pos=(-34.1,-43,15.25) rot=(-1,0,0;1.5708rad)
  Radius = 1.5
FEATURE [Part::MultiFuse] Fusion001005002004004005002010002003003003017007024041010023003003006006003006008021048  label="Fusion-203"
  Refine = true
  Shapes = -> [Fusion001005002004004005002010002003003003017007024041010023003003006006003006008021047,Cylinder924]
FEATURE [Part::Cut] Cut012035015003002009024006019009
  Base = -> Fusion001005002004004005002010002003003003017007024041010023003003006006003006008021048
  Refine = true
  Tool = -> Cylinder927
FEATURE [Part::Box] Box140  label="Cube140"
  AttacherType = Attacher::AttachEngine3D
  Height = 1
  Length = 8.5
  Placement = pos=(-4.25,-43,-9) rot=(0,0,1;0rad)
  Width = 7
FEATURE [Part::Box] Box141  label="Cube141"
  AttacherType = Attacher::AttachEngine3D
  Height = 2
  Length = 2
  Placement = pos=(-6.25,-43,-10) rot=(0,0,1;0rad)
  Width = 7
FEATURE [Part::Box] Box142  label="Cube142"
  AttacherType = Attacher::AttachEngine3D
  Height = 2
  Length = 2
  Placement = pos=(4.25,-43,-10) rot=(0,0,1;0rad)
  Width = 7
FEATURE [Part::MultiFuse] Fusion001005002004004005002010002003003003017007024041010023003003006006003006008021050  label="Fusion-205"
  Refine = true
  Shapes = -> [Box141,Box142]
FEATURE [Part::Chamfer] Chamfer007024
  Base = -> Fusion001005002004004005002010002003003003017007024041010023003003006006003006008021050
  Edges = 2 edges r=1: [Edge4,Edge20]
FEATURE [Part::Chamfer] Chamfer
  Base = -> Cut012035015003002009024006019009
  Edges = 1 edges: [Edge6 r1=2.6 r2=15]
  Placement = pos=(0,0,-12) rot=(0,0,1;0rad)
FEATURE [Part::MultiFuse] Fusion001005002004004005002010002003003003017007024041010023003003006006003006008021051  label="Fusion-206"
  Refine = true
  Shapes = -> [Chamfer,Box139]
FEATURE [Part::Cut] Cut012035015003002009024006019010
  Base = -> Fusion001005002004004005002010002003003003017007024041010023003003006006003006008021051
  Refine = true
  Tool = -> Box140
FEATURE [Part::Fillet] Fillet
  Base = -> Cut012035015003002009024006019010
  Edges = 10 edges r=1: [Edge7,Edge11,Edge24,Edge28,Edge31,Edge49,Edge51,Edge55,Edge68,Edge72]
FEATURE [Part::MultiFuse] Fusion001005002004004005002010002003003003017007024041010023003003006006003006008021052  label="axle-leafspring-left_OLD"
  Refine = true
  Shapes = -> [Chamfer007024,Fillet]
FEATURE [Part::Box] Box144  label="Cube144"
  AttacherType = Attacher::AttachEngine3D
  Height = 10
  Length = 11
  Placement = pos=(484,-76,25) rot=(0,0,1;0rad)
  Width = 10
FEATURE [Part::Cylinder] Cylinder928  label="Cylinder998"
  Angle = 360
  AttacherType = Attacher::AttachEngine3D
  Height = 182
  Placement = pos=(546,-99,13) rot=(-1,0,0;1.5708rad)
  Radius = 2.5
FEATURE [Part::Box] Box145  label="Cube145"
  AttacherType = Attacher::AttachEngine3D
  Height = 15
  Length = 11
  Placement = pos=(555,-48,2.5) rot=(0,0,1;0rad)
  Width = 4
FEATURE [Part::Chamfer] Chamfer007025
  Base = -> Box145
  Edges = 1 edges: [Edge6 r1=3.6 r2=10.999]
FEATURE [Part::Chamfer] Chamfer007026
  Base = -> Chamfer007025
  Edges = 1 edges: [Edge3 r1=1.1 r2=10.999]
FEATURE [Part::Fillet] Fillet001021
  Base = -> Chamfer007026
  Edges = 2 edges r=4: [Edge2,Edge3]
FEATURE [Part::Chamfer] Chamfer007027
  Base = -> Box134
  Edges = 1 edges: [Edge6 r1=2.6 r2=7.999]
FEATURE [Part::Chamfer] Chamfer007028
  Base = -> Chamfer007027
  Edges = 1 edges: [Edge11 r1=7.999 r2=2.6]
FEATURE [Part::Cone] Cone015
  Angle = 360
  AttacherType = Attacher::AttachEngine3D
  Height = 1
  Placement = pos=(0,0,0) rot=(-1,0,0;1.5708rad)
  Radius1 = 2
  Radius2 = 1.2
FEATURE [Part::Cylinder] Cylinder931  label="Cylinder1001"
  Angle = 360
  AttacherType = Attacher::AttachEngine3D
  Height = 4
  Placement = pos=(0,0,0) rot=(-1,0,0;1.5708rad)
  Radius = 1.2
FEATURE [Part::Cylinder] Cylinder932  label="Cylinder1002"
  Angle = 360
  AttacherType = Attacher::AttachEngine3D
  Height = 17
  Placement = pos=(0,0,0) rot=(-1,0,0;1.5708rad)
  Radius = 0.8
FEATURE [Part::MultiFuse] Fusion001005002004004005002010002003003003017007024041010023003003006006003006008021054  label="Fusion-208"
  Placement = pos=(551,-100,15) rot=(0,0,1;0rad)
  Refine = true
  Shapes = -> [Cone015,Cylinder931,Cylinder932]
FEATURE [Part::Feature] Fusion001005002004004005002010002003003003017007024041010023003003006006003006008021054001  label="Fusion-209"
  Placement = pos=(551,-100,7.5) rot=(0,0,1;0rad)
  shape: bbox 4 x 17 x 4 mm, 6 faces (baked)
FEATURE [Part::Feature] Fusion001005002004004005002010002003003003017007024041010023003003006006003006008021054002  label="Fusion-210"
  Placement = pos=(531,-100,19) rot=(0,0,1;0rad)
  shape: bbox 4 x 17 x 4 mm, 6 faces (baked)
FEATURE [Part::Feature] Fusion001005002004004005002010002003003003017007024041010023003003006006003006008021054003  label="Fusion-211"
  Placement = pos=(499,-100,29.5) rot=(0,0,1;0rad)
  shape: bbox 4 x 17 x 4 mm, 6 faces (baked)
FEATURE [Part::Feature] Fusion001005002004004005002010002003003003017007024041010023003003006006003006008021054004  label="Fusion-212"
  Placement = pos=(505,-100,27.4) rot=(0,0,1;0rad)
  shape: bbox 4 x 17 x 4 mm, 6 faces (baked)
FEATURE [Part::MultiFuse] Fusion001005002004004005002010002003003003017007024041010023003003006006003006008021054005  label="Fusion-217"
  Refine = true
  Shapes = -> [Fusion001005002004004005002010002003003003017007024041010023003003006006003006008021054001,Fusion001005002004004005002010002003003003017007024041010023003003006006003006008021054003,Fusion001005002004004005002010002003003003017007024041010023003003006006003006008021054004,Fusion001005002004004005002010002003003003017007024041010023003003006006003006008021054002,+1 more]
FEATURE [Part::Cylinder] Cylinder933  label="Cylinder1003"
  Angle = 360
  AttacherType = Attacher::AttachEngine3D
  Height = 83
  Placement = pos=(538,-96,16) rot=(-1,0,0;1.5708rad)
  Radius = 3.25
FEATURE [Part::Cylinder] Cylinder934  label="Cylinder1004"
  Angle = 360
  AttacherType = Attacher::AttachEngine3D
  Height = 88
  Placement = pos=(538,-96,16) rot=(-1,0,0;1.5708rad)
  Radius = 1.7
FEATURE [Part::Cylinder] Cylinder935  label="Cylinder1005"
  Angle = 360
  AttacherType = Attacher::AttachEngine3D
  Height = 118
  Placement = pos=(538,-96,16) rot=(-1,0,0;1.5708rad)
  Radius = 1.25
FEATURE [Part::MultiFuse] Fusion001005002004004005002010002003003003017007024041010023003003006006003006008021054006  label="Fusion-213"
  Refine = true
  Shapes = -> [Cylinder935,Cylinder933,Cylinder934]
FEATURE [Part::Feature] Fusion001005002004004005002010002003003003017007024041010023003003006006003006008021054006001  label="Fusion-214"
  Placement = pos=(-26,0,9) rot=(0,0,1;0rad)
  shape: bbox 6.5 x 118 x 6.5 mm, 7 faces (baked)
FEATURE [Part::Feature] Fusion001005002004004005002010002003003003017007024041010023003003006006003006008021054006002  label="Fusion-215"
  Placement = pos=(-81,0,14) rot=(0,0,1;0rad)
  shape: bbox 6.5 x 118 x 6.5 mm, 7 faces (baked)
FEATURE [Part::Feature] Fusion001005002004004005002010002003003003017007024041010023003003006006003006008021054006003  label="Fusion-216"
  Placement = pos=(-67,0,14) rot=(0,0,1;0rad)
  shape: bbox 6.5 x 118 x 6.5 mm, 7 faces (baked)
FEATURE [Part::Cylinder] Cylinder936  label="Cylinder1006"
  Angle = 360
  AttacherType = Attacher::AttachEngine3D
  Height = 30
  Placement = pos=(478,-45,30) rot=(-1,0,0;1.5708rad)
  Radius = 1.25
FEATURE [Part::Cylinder] Cylinder937  label="Cylinder1007"
  Angle = 360
  AttacherType = Attacher::AttachEngine3D
  Height = 30
  Placement = pos=(464,-45,30) rot=(-1,0,0;1.5708rad)
  Radius = 1.25
FEATURE [Part::Cylinder] Cylinder938  label="Cylinder1008"
  Angle = 360
  AttacherType = Attacher::AttachEngine3D
  Height = 30
  Placement = pos=(450,-45,30) rot=(-1,0,0;1.5708rad)
  Radius = 1.25
FEATURE [Part::MultiFuse] Fusion001005002004004005002010002003003003017007024041010023003003006006003006008021054006004  label="rear-platform-joining-screws"
  Refine = true
  Shapes = -> [Fusion001005002004004005002010002003003003017007024041010023003003006006003006008021054006003,Fusion001005002004004005002010002003003003017007024041010023003003006006003006008021054006002,Fusion001005002004004005002010002003003003017007024041010023003003006006003006008021054006001,Fusion001005002004004005002010002003003003017007024041010023003003006006003006008021054006]
FEATURE [Part::Feature] Fusion001005002004004005002010002003003003017007024041010023003003006006003006008021054005001  label="Fusion-218"
  shape: bbox 56 x 17 x 26 mm, 30 faces, 5 solids (baked)
FEATURE [Part::Cylinder] Cylinder939  label="Cylinder1009"
  Angle = 360
  AttacherType = Attacher::AttachEngine3D
  Height = 184
  Placement = pos=(490,-100,30) rot=(-1,0,0;1.5708rad)
  Radius = 2.7
FEATURE [Part::Cylinder] Cylinder940  label="Cylinder1010"
  Angle = 360
  AttacherType = Attacher::AttachEngine3D
  Height = 182
  Placement = pos=(546,-99,13) rot=(-1,0,0;1.5708rad)
  Radius = 2.7
FEATURE [Part::MultiFuse] Fusion001005002004004005002010002003003003017007024041010023003003006006003006008021054006005  label="Fusion"
  Refine = true
  Shapes = -> [Cylinder939,Cylinder938,Cylinder940,Cylinder937,Cylinder936,Fusion001005002004004005002010002003003003017007024041010023003003006006003006008021054005001]
FEATURE [Part::Cut] Cut012035015003002009024006019011
  Base = -> Fillet001021
  Refine = true
  Tool = -> Cylinder919
FEATURE [Part::Feature] Cut012035015003002009024006019011001  label="Cut012035015003002009024006019012"
  Placement = pos=(0,-52,0) rot=(0,0,1;0rad)
  shape: bbox 11 x 4 x 15 mm, 11 faces (baked)
FEATURE [Part::Cylinder] Cylinder941  label="Cylinder1011"
  Angle = 360
  AttacherType = Attacher::AttachEngine3D
  Height = 59
  Placement = pos=(561.2,-101,9.2) rot=(-1,0,0;1.5708rad)
  Radius = 1.5
FEATURE [Part::Box] Box146  label="Cube146"
  AttacherType = Attacher::AttachEngine3D
  Height = 42.5
  Length = 11
  Placement = pos=(502,-81,31) rot=(0,1,0;1.88496rad)
  Width = 56
FEATURE [Part::Feature] Face013
  shape: bbox 74.39 x 2e-07 x 37.47 mm, 1 faces, 0 solids (baked)
FEATURE [Part::Extrusion] Extrude016
  Base = -> Face013
  Dir = (0,1,0)
  DirMode = 0
  FaceMakerClass = Part::FaceMakerBullseye
  LengthFwd = 88
  LengthRev = 0
  Solid = true
  Symmetric = false
FEATURE [Part::MultiFuse] Fusion001005002004004005002010002003003003017007024041010023003003006006003006008021054006004002  label="Fusion-220"
  Refine = true
  Shapes = -> [Box118,Extrude016,Cut012035015003002009024006019011,Chamfer007028,Box144]
FEATURE [Part::Cut] Cut012035015003002009024006019011003
  Base = -> Fusion001005002004004005002010002003003003017007024041010023003003006006003006008021054006004002
  Refine = true
  Tool = -> Fusion001005002004004005002010002003003003017007024041010023003003006006003006008021054006005
FEATURE [Part::Cut] Cut012035015003002009024006019011004
  Base = -> Cut012035015003002009024006019011003
  Refine = true
  Tool = -> Box146
FEATURE [Part::Chamfer] Chamfer007029
  Base = -> Cut012035015003002009024006019011004
  Edges = 1 edges: [Edge111 r1=9.2 r2=20]
FEATURE [Part::Feature] Face015
  shape: bbox 31.48 x 2e-07 x 30.83 mm, 1 faces, 0 solids (baked)
FEATURE [Part::Extrusion] Extrude017
  Base = -> Face015
  Dir = (0,1,0)
  DirMode = 0
  FaceMakerClass = Part::FaceMakerBullseye
  LengthFwd = 16
  LengthRev = 0
  Solid = true
  Symmetric = false
FEATURE [Part::Fillet] Fillet001022
  Base = -> Extrude017
  Edges = 2 edges r=12: [Edge8,Edge17]
FEATURE [Part::Box] Box149  label="Cube149"
  AttacherType = Attacher::AttachEngine3D
  Height = 19
  Length = 14
  Placement = pos=(562.173,-77.3,-13) rot=(0,0,1;0rad)
  Width = 10.6
FEATURE [Part::Cut] Cut012035015003002009024006019011006
  Base = -> Fillet001022
  Refine = true
  Tool = -> Box149
FEATURE [Part::Cylinder] Cylinder942  label="Cylinder1012"
  Angle = 360
  AttacherType = Attacher::AttachEngine3D
  Height = 59
  Placement = pos=(568,-101,-7) rot=(-1,0,0;1.5708rad)
  Radius = 1.5
FEATURE [Part::Cut] Cut012035015003002009024006019011007
  Base = -> Cut012035015003002009024006019011006
  Refine = true
  Tool = -> Cylinder942
FEATURE [Part::Cylinder] Cylinder943  label="Cylinder1013"
  Angle = 360
  AttacherType = Attacher::AttachEngine3D
  Height = 10
  Placement = pos=(551,-38,2.5) rot=(0,0,1;0rad)
  Radius = 1.25
FEATURE [Part::Box] Box150  label="Cube150"
  AttacherType = Attacher::AttachEngine3D
  Height = 5
  Length = 8
  Placement = pos=(547,-44,2.5) rot=(0,0,1;0rad)
  Width = 36
FEATURE [Part::Cylinder] Cylinder944  label="Cylinder1014"
  Angle = 360
  AttacherType = Attacher::AttachEngine3D
  Height = 16
  Placement = pos=(542,-78,2.5) rot=(0,1,0;0.296706rad)
  Radius = 0.9
FEATURE [Part::Cylinder] Cylinder945  label="Cylinder1015"
  Angle = 360
  AttacherType = Attacher::AttachEngine3D
  Height = 16
  Placement = pos=(542,-66,2.5) rot=(0,1,0;0.296706rad)
  Radius = 0.9
FEATURE [Part::Cylinder] Cylinder946  label="Cylinder1016"
  Angle = 360
  AttacherType = Attacher::AttachEngine3D
  Height = 10
  Placement = pos=(483,-20,24.5) rot=(0,1,0;0rad)
  Radius = 0.9
FEATURE [Part::Cylinder] Cylinder947  label="Cylinder1017"
  Angle = 360
  AttacherType = Attacher::AttachEngine3D
  Height = 10
  Placement = pos=(451,-20,24.5) rot=(0,1,0;0rad)
  Radius = 0.9
FEATURE [Part::MultiFuse] Fusion001005002004004005002010002003003003017007024041010023003003006006003006008021054006004004  label="Fusion-222"
  Refine = true
  Shapes = -> [Cylinder943,Cylinder944,Cylinder945,Cylinder946,Cylinder947]
FEATURE [Part::Cylinder] Cylinder948  label="Cylinder1018"
  Angle = 360
  AttacherType = Attacher::AttachEngine3D
  Height = 10
  Placement = pos=(541,-92,11) rot=(0,1,0;0.296706rad)
  Radius = 0.9
FEATURE [Part::Cylinder] Cylinder949  label="Cylinder1019"
  Angle = 360
  AttacherType = Attacher::AttachEngine3D
  Height = 10
  Placement = pos=(541,-22,11) rot=(0,1,0;0.296706rad)
  Radius = 0.9
FEATURE [Part::Cylinder] Cylinder950  label="Cylinder1020"
  Angle = 360
  AttacherType = Attacher::AttachEngine3D
  Height = 10
  Placement = pos=(496,-22,25.5) rot=(0,1,0;0.296706rad)
  Radius = 0.9
FEATURE [Part::Cylinder] Cylinder951  label="Cylinder1021"
  Angle = 360
  AttacherType = Attacher::AttachEngine3D
  Height = 10
  Placement = pos=(496,-92,25.5) rot=(0,1,0;0.296706rad)
  Radius = 0.9
FEATURE [Part::MultiFuse] Fusion001005002004004005002010002003003003017007024041010023003003006006003006008021054006004005  label="Fusion-223"
  Refine = true
  Shapes = -> [Cylinder948,Cylinder951,Cylinder950,Cylinder949]
FEATURE [Part::MultiFuse] Fusion001005002004004005002010002003003003017007024041010023003003006006003006008021054006004006  label="Fusion-224"
  Refine = true
  Shapes = -> [Fusion001005002004004005002010002003003003017007024041010023003003006006003006008021054006004004,Fusion001005002004004005002010002003003003017007024041010023003003006006003006008021054006004005]
FEATURE [Part::MultiFuse] Fusion001005002004004005002010002003003003017007024041010023003003006006003006008021054006004007  label="Fusion-225"
  Refine = true
  Shapes = -> [Chamfer007029,Box150]
FEATURE [Part::Box] Box151  label="Cube151"
  AttacherType = Attacher::AttachEngine3D
  Height = 1
  Length = 55
  Placement = pos=(495,-96,36) rot=(0,1,0;0.314159rad)
  Width = 176
FEATURE [Part::MultiFuse] Fusion001005002004004005002010002003003003017007024041010023003003006006003006008021054006004008  label="Fusion-226"
  Refine = true
  Shapes = -> [Cut012035015003002009024006019011007,Fusion001005002004004005002010002003003003017007024041010023003003006006003006008021054006004007]
FEATURE [Part::Cut] Cut012035015003002009024006019011008
  Base = -> Fusion001005002004004005002010002003003003017007024041010023003003006006003006008021054006004008
  Refine = true
  Tool = -> Fusion001005002004004005002010002003003003017007024041010023003003006006003006008021054006004006
FEATURE [Part::Cut] Cut012035015003002009024006019011009  label="rear-platform-base-left"
  Base = -> Cut012035015003002009024006019011008
  Refine = true
  Tool = -> Box151
FEATURE [Part::Feature] Cut012035015003002009024006019011009001  label="rear-platform-base001"
  shape: bbox 131.3 x 88 x 55.12 mm, 107 faces (baked)
FEATURE [Part::Mirroring] Part__Mirroring005002002002002002002002002004  label="rear-platform-base-right"
  Base = (0,0,0)
  Normal = (0,1,0)
  Placement = pos=(0,-16,0) rot=(0,0,1;0rad)
  Source = -> Cut012035015003002009024006019011009001
FEATURE [Part::Feature] Fusion001005002004004005002010002003003003017007024041010023003003006006003006008021054006004009  label="rear-platform-joining-screws001"
  shape: bbox 87.5 x 118 x 20.5 mm, 28 faces, 4 solids (baked)
FEATURE [Part::Cut] Cut012035015003002009024006019011009002  label="rear-platform-left-OLD"
  Base = -> Cut012035015003002009024006019011009
  Refine = true
  Tool = -> Fusion001005002004004005002010002003003003017007024041010023003003006006003006008021054006004
FEATURE [Part::Cut] Cut012035015003002009024006019011009003  label="rear-platform-right-OLD"
  Base = -> Part__Mirroring005002002002002002002002002004
  Refine = true
  Tool = -> Fusion001005002004004005002010002003003003017007024041010023003003006006003006008021054006004009
FEATURE [Part::Feature] Fusion001005002004004005002010002003003003017007024041010023003003006006003006008021054006004010  label="Fusion-227"
  Placement = pos=(480,-100,29.5) rot=(0,0,1;0rad)
  shape: bbox 4 x 17 x 4 mm, 6 faces (baked)
FEATURE [Part::Feature] Fusion001005002004004005002010002003003003017007024041010023003003006006003006008021054006004013001  label="Fusion-230"
  shape: bbox 22 x 17 x 4 mm, 12 faces, 2 solids (baked)
FEATURE [Part::Feature] Fusion001005002004004005002010002003003003017007024041010023003003006006003006008021054006004013002  label="Fusion-231"
  Placement = pos=(-86,0,0) rot=(0,0,1;0rad)
  shape: bbox 22 x 17 x 4 mm, 12 faces, 2 solids (baked)
FEATURE [Part::Feature] Fusion001005002004004005002010002003003003017007024041010023003003006006003006008021054006004013003  label="Fusion-232"
  Placement = pos=(-172,0,0) rot=(0,0,1;0rad)
  shape: bbox 22 x 17 x 4 mm, 12 faces, 2 solids (baked)
FEATURE [Part::Box] Box152  label="Cube152"
  AttacherType = Attacher::AttachEngine3D
  Height = 10
  Length = 19.5
  Placement = pos=(475,-96,26) rot=(0,0,1;0rad)
  Width = 10
FEATURE [Part::Box] Box154  label="Cube154"
  AttacherType = Attacher::AttachEngine3D
  Height = 9
  Length = 9.5
  Placement = pos=(485,-56,27) rot=(0,0,1;0rad)
  Width = 10
FEATURE [Part::Box] Box155  label="Cube155"
  AttacherType = Attacher::AttachEngine3D
  Height = 5
  Length = 5
  Placement = pos=(487.5,-96,25) rot=(0,0,1;0rad)
  Width = 50
FEATURE [Part::MultiFuse] Fusion001005002004004005002010002003003003017007024041010023003003006006003006008021054006004013004  label="Fusion-233"
  Refine = true
  Shapes = -> [Box152,Box154]
FEATURE [Part::Cylinder] Cylinder952  label="Cylinder1022"
  Angle = 360
  AttacherType = Attacher::AttachEngine3D
  Height = 53
  Placement = pos=(490,-99,30) rot=(-1,0,0;1.5708rad)
  Radius = 2.7
FEATURE [Part::MultiFuse] Fusion001005002004004005002010002003003003017007024041010023003003006006003006008021054006004013005  label="Fusion-234"
  Refine = true
  Shapes = -> [Box155,Cylinder952]
FEATURE [Part::Cut] Cut012035015003002009024006019011009004
  Base = -> Fusion001005002004004005002010002003003003017007024041010023003003006006003006008021054006004013004
  Refine = true
  Tool = -> Fusion001005002004004005002010002003003003017007024041010023003003006006003006008021054006004013005
FEATURE [Part::Chamfer] Chamfer007030
  Base = -> Cut012035015003002009024006019011009004
  Edges = 2 edges: [Edge22 r1=0.5 r2=1.5,Edge48 r1=0.5 r2=1.5]
FEATURE [Part::Chamfer] Chamfer007031
  Base = -> Chamfer007030
  Edges = 2 edges: [Edge28 r1=0.5 r2=1.5,Edge57 r1=0.5 r2=1.5]
FEATURE [Part::Box] Box156  label="Cube156"
  AttacherType = Attacher::AttachEngine3D
  Height = 1
  Length = 19.5
  Placement = pos=(475,-96,35) rot=(0,0,1;0rad)
  Width = 88
FEATURE [Part::Feature] Fusion001005002004004005002010002003003003017007024041010023003003006006003006008021054006004013005001  label="Fusion-235"
  Placement = pos=(-87,0,0) rot=(0,0,1;0rad)
  shape: bbox 5.4 x 53 x 7.7 mm, 7 faces (baked)
FEATURE [Part::Box] Box157  label="Cube157"
  AttacherType = Attacher::AttachEngine3D
  Height = 10
  Length = 30
  Placement = pos=(388,-96,26) rot=(0,0,1;0rad)
  Width = 10
FEATURE [Part::Box] Box158  label="Cube158"
  AttacherType = Attacher::AttachEngine3D
  Height = 9
  Length = 10
  Placement = pos=(398,-56,27) rot=(0,0,1;0rad)
  Width = 10
FEATURE [Part::Chamfer] Chamfer007032
  Base = -> Chamfer007031
  Edges = 1 edges r=3: [Edge27]
FEATURE [Part::MultiFuse] Fusion001005002004004005002010002003003003017007024041010023003003006006003006008021054006004013005002  label="Fusion-237"
  Refine = true
  Shapes = -> [Box156,Chamfer007032]
FEATURE [Part::Feature] Fusion001005002004004005002010002003003003017007024041010023003003006006003006008021054006004013005003  label="Fusion-238"
  Placement = pos=(480,-100,29.5) rot=(0,0,1;0rad)
  shape: bbox 4 x 17 x 4 mm, 6 faces (baked)
FEATURE [Part::Cut] Cut012035015003002009024006019011009005  label="Cut-000"
  Base = -> Fusion001005002004004005002010002003003003017007024041010023003003006006003006008021054006004013005002
  Refine = true
  Tool = -> Fusion001005002004004005002010002003003003017007024041010023003003006006003006008021054006004013005003
FEATURE [Part::Cylinder] Cylinder953  label="Cylinder1023"
  Angle = 360
  AttacherType = Attacher::AttachEngine3D
  Height = 10
  Placement = pos=(484,-92,26) rot=(0,1,0;0rad)
  Radius = 0.9
FEATURE [Part::Cut] Cut012035015003002009024006019011009006  label="Cut-001"
  Base = -> Cut012035015003002009024006019011009005
  Refine = true
  Tool = -> Cylinder953
FEATURE [Part::Chamfer] Chamfer007033
  Base = -> Box157
  Edges = 2 edges r=3: [Edge4,Edge8]
FEATURE [Part::MultiFuse] Fusion001005002004004005002010002003003003017007024041010023003003006006003006008021054006004013005005  label="Fusion-240"
  Refine = true
  Shapes = -> [Box158,Chamfer007033]
FEATURE [Part::Cut] Cut012035015003002009024006019011009006002  label="Cut-003"
  Base = -> Fusion001005002004004005002010002003003003017007024041010023003003006006003006008021054006004013005005
  Refine = true
  Tool = -> Fusion001005002004004005002010002003003003017007024041010023003003006006003006008021054006004013005001
FEATURE [Part::Chamfer] Chamfer007034
  Base = -> Cut012035015003002009024006019011009006002
  Edges = 2 edges: [Edge22 r1=0.5 r2=1.5,Edge53 r1=0.5 r2=1.5]
FEATURE [Part::Chamfer] Chamfer007035
  Base = -> Chamfer007034
  Edges = 1 edges: [Edge28 r1=0.5 r2=1.5]
FEATURE [Part::Chamfer] Chamfer007036
  Base = -> Chamfer007035
  Edges = 1 edges: [Edge64 r1=1.5 r2=0.5]
FEATURE [Part::Cylinder] Cylinder954  label="Cylinder1024"
  Angle = 360
  AttacherType = Attacher::AttachEngine3D
  Height = 10
  Placement = pos=(408,-92,26) rot=(0,1,0;0rad)
  Radius = 0.9
FEATURE [Part::Box] Box159  label="Cube159"
  AttacherType = Attacher::AttachEngine3D
  Height = 1
  Length = 30
  Placement = pos=(388,-96,35) rot=(0,0,1;0rad)
  Width = 88
FEATURE [Part::Feature] Fusion001005002004004005002010002003003003017007024041010023003003006006003006008021054006004013005006  label="Fusion-241"
  shape: bbox 22 x 17 x 4 mm, 12 faces, 2 solids (baked)
FEATURE [Part::MultiFuse] Fusion001005002004004005002010002003003003017007024041010023003003006006003006008021054006004013005007  label="Fusion-242"
  Refine = true
  Shapes = -> [Chamfer007036,Box159]
FEATURE [Part::Cut] Cut012035015003002009024006019011009006003  label="Cut-004"
  Base = -> Fusion001005002004004005002010002003003003017007024041010023003003006006003006008021054006004013005007
  Refine = true
  Tool = -> Fusion001005002004004005002010002003003003017007024041010023003003006006003006008021054006004013005006
FEATURE [Part::Cut] Cut012035015003002009024006019011009006004  label="Cut-005"
  Base = -> Cut012035015003002009024006019011009006003
  Refine = true
  Tool = -> Cylinder954
FEATURE [Part::Chamfer] Chamfer007037
  Base = -> Cut012035015003002009024006019011009006004
  Edges = 2 edges r=7.999: [Edge55,Edge57]
FEATURE [Part::Chamfer] Chamfer007038
  Base = -> Cut012035015003002009024006019011009006
  Edges = 1 edges r=7.999: [Edge8]
FEATURE [Part::Cylinder] Cylinder963  label="Cylinder1033"
  Angle = 360
  AttacherType = Attacher::AttachEngine3D
  Height = 10
  Placement = pos=(-15,-8,31) rot=(0,0,1;0rad)
  Radius = 1.25
FEATURE [Part::Cylinder] Cylinder964  label="Cylinder1034"
  Angle = 360
  AttacherType = Attacher::AttachEngine3D
  Height = 10
  Placement = pos=(15,-8,31) rot=(0,0,1;0rad)
  Radius = 1.25
FEATURE [Part::Cylinder] Cylinder965  label="Cylinder1035"
  Angle = 121
  AttacherType = Attacher::AttachEngine3D
  Height = 3.5
  Placement = pos=(0,-8,31) rot=(0,0,-1;1.05592rad)
  Radius = 18.5
FEATURE [Part::Cylinder] Cylinder966  label="Cylinder1036"
  Angle = 121
  AttacherType = Attacher::AttachEngine3D
  Height = 3.5
  Placement = pos=(0,-8,31) rot=(0,0,-1;1.05592rad)
  Radius = 11.5
FEATURE [Part::Cut] Cut012035015003002009024006019011009006017  label="Cut-014"
  Base = -> Cylinder965
  Refine = true
  Tool = -> Cylinder966
FEATURE [Part::Fillet] Fillet001025
  Base = -> Cut012035015003002009024006019011009006017
  Edges = 4 edges r=3.4: [Edge2,Edge4,Edge9,Edge12]
FEATURE [Part::Feature] Fillet001025001  label="Fillet001026"
  shape: bbox 11.8 x 29.06 x 3.5 mm, 10 faces (baked)
FEATURE [Part::Mirroring] Part__Mirroring005002002002002002002002002005  label="Fillet001026 (Mirror #4)"
  Base = (0,0,0)
  Normal = (1,0,0)
  Source = -> Fillet001025001
FEATURE [Part::MultiFuse] Fusion001005002004004005002010002003003003017007024041010023003003006006003006008021054006004013005009020003  label="Fusion-267"
  Refine = true
  Shapes = -> [Part__Mirroring005002002002002002002002002005,Fillet001025]
FEATURE [Part::MultiFuse] Fusion001005002004004005002010002003003003017007024041010023003003006006003006008021054006004013005009020003002  label="Fusion-269"
  Placement = pos=(0,0,-9) rot=(0,0,1;0rad)
  Refine = true
  Shapes = -> [Cylinder963,Cylinder964]
FEATURE [Part::Cut] Cut012035015003002009024006019011009006018  label="rotation-upper-platform"
  Base = -> Cut012035015003002007
  Refine = true
  Tool = -> Fusion001005002004004005002010002003003003017007024041010023003003006006003006008021054006004013005009020003
FEATURE [Part::Cut] Cut012035015003002009024006019011009006019  label="rotation-lower-platform"
  Base = -> Cut012035015003002009024017
  Refine = true
  Tool = -> Fusion001005002004004005002010002003003003017007024041010023003003006006003006008021054006004013005009020003002
FEATURE [Part::Cylinder] Cylinder967  label="Cylinder1037"
  Angle = 360
  AttacherType = Attacher::AttachEngine3D
  Height = 182
  Placement = pos=(120,-99,30) rot=(-1,0,0;1.5708rad)
  Radius = 2.5
FEATURE [Part::Box] Box179  label="Cube179"
  AttacherType = Attacher::AttachEngine3D
  Height = 10
  Length = 60
  Placement = pos=(65,-46,25) rot=(0,0,1;0rad)
  Width = 3
FEATURE [Part::Cylinder] Cylinder968  label="Cylinder1038"
  Angle = 360
  AttacherType = Attacher::AttachEngine3D
  Height = 20
  Placement = pos=(120,-46,30) rot=(-1,0,0;1.5708rad)
  Radius = 1.5
FEATURE [Part::Cylinder] Cylinder969  label="Cylinder1039"
  Angle = 360
  AttacherType = Attacher::AttachEngine3D
  Height = 20
  Placement = pos=(110,-46,30) rot=(-1,0,0;1.5708rad)
  Radius = 1.5
FEATURE [Part::Cylinder] Cylinder970  label="Cylinder1040"
  Angle = 360
  AttacherType = Attacher::AttachEngine3D
  Height = 20
  Placement = pos=(90,-46,30) rot=(-1,0,0;1.5708rad)
  Radius = 1.5
FEATURE [Part::Cylinder] Cylinder971  label="Cylinder1041"
  Angle = 360
  AttacherType = Attacher::AttachEngine3D
  Height = 20
  Placement = pos=(70,-46,30) rot=(-1,0,0;1.5708rad)
  Radius = 1.5
FEATURE [Part::MultiFuse] Fusion001005002004004005002010002003003003017007024041010023003003006006003006008021054006004013005009020003003  label="Fusion-270"
  Refine = true
  Shapes = -> [Cylinder968,Cylinder971,Cylinder970,Cylinder969]
FEATURE [Part::Cut] Cut012035015003002009024006019011009006020  label="attach-front-HOLESTOOL"
  Base = -> Box179
  Refine = true
  Tool = -> Fusion001005002004004005002010002003003003017007024041010023003003006006003006008021054006004013005009020003003
FEATURE [Part::Box] Box186  label="Cube186"
  AttacherType = Attacher::AttachEngine3D
  Height = 10
  Length = 70
  Placement = pos=(65,-96,26) rot=(0,0,1;0rad)
  Width = 10
FEATURE [Part::Cylinder] Cylinder974  label="Cylinder1044"
  Angle = 360
  AttacherType = Attacher::AttachEngine3D
  Height = 10
  Placement = pos=(81,-92,26) rot=(0,1,0;0rad)
  Radius = 0.9
FEATURE [Part::Box] Box187  label="Cube187"
  AttacherType = Attacher::AttachEngine3D
  Height = 1
  Length = 70
  Placement = pos=(65,-96,35) rot=(0,0,1;0rad)
  Width = 88
FEATURE [Part::Box] Box188  label="Cube188"
  AttacherType = Attacher::AttachEngine3D
  Height = 11
  Length = 70
  Placement = pos=(65,-48,25) rot=(0,0,1;0rad)
  Width = 5
FEATURE [Part::Chamfer] Chamfer007038014
  Base = -> Box188
  Edges = 1 edges r=5: [Edge4]
FEATURE [Part::Cylinder] Cylinder985  label="Cylinder1055"
  Angle = 360
  AttacherType = Attacher::AttachEngine3D
  Height = 3
  Placement = pos=(478,-47,30) rot=(-1,0,0;1.5708rad)
  Radius = 3.5
FEATURE [Part::Cut] Cut012035015003002009024006019011009006027  label="Cut-021"
  Base = -> Chamfer007038
  Refine = true
  Tool = -> Cylinder985
FEATURE [Part::Cylinder] Cylinder986  label="Cylinder1056"
  Angle = 360
  AttacherType = Attacher::AttachEngine3D
  Height = 3
  Placement = pos=(414,-47,30) rot=(-1,0,0;1.5708rad)
  Radius = 3.5
FEATURE [Part::Cylinder] Cylinder987  label="Cylinder1057"
  Angle = 360
  AttacherType = Attacher::AttachEngine3D
  Height = 3
  Placement = pos=(392,-47,30) rot=(-1,0,0;1.5708rad)
  Radius = 3.5
FEATURE [Part::MultiFuse] Fusion001005002004004005002010002003003003017007024041010023003003006006003006008021054006004013005009020003027  label="Fusion-287"
  Refine = true
  Shapes = -> [Cylinder986,Cylinder987]
FEATURE [Part::Cut] Cut012035015003002009024006019011009006027002  label="Cut-023"
  Base = -> Chamfer007037
  Refine = true
  Tool = -> Fusion001005002004004005002010002003003003017007024041010023003003006006003006008021054006004013005009020003027
FEATURE [Part::Feature] Cut012035015003002009024006019011009006027002002  label="Cut-025"
  shape: bbox 19.5 x 88 x 10 mm, 30 faces (baked)
FEATURE [Part::Mirroring] Part__Mirroring005002002002002002002002002012  label="Cut-025 (Mirror #6)"
  Base = (0,0,0)
  Normal = (0,1,0)
  Placement = pos=(0,-16,0) rot=(0,0,1;0rad)
  Source = -> Cut012035015003002009024006019011009006027002002
FEATURE [Part::MultiFuse] Fusion001005002004004005002010002003003003017007024041010023003003006006003006008021054006004013005009020003029  label="plate-attach-rear"
  Refine = true
  Shapes = -> [Part__Mirroring005002002002002002002002002012,Cut012035015003002009024006019011009006027]
FEATURE [Part::Feature] Cut012035015003002009024006019011009006027002003  label="Cut-026"
  shape: bbox 30 x 88 x 10 mm, 36 faces (baked)
FEATURE [Part::Mirroring] Part__Mirroring005002002002002002002002002013  label="Cut-026 (Mirror #6)"
  Base = (0,0,0)
  Normal = (0,1,0)
  Placement = pos=(0,-16,0) rot=(0,0,1;0rad)
  Source = -> Cut012035015003002009024006019011009006027002003
FEATURE [Part::MultiFuse] Fusion001005002004004005002010002003003003017007024041010023003003006006003006008021054006004013005009020003030  label="plate-attach-middle-3"
  Refine = true
  Shapes = -> [Part__Mirroring005002002002002002002002002013,Cut012035015003002009024006019011009006027002]
FEATURE [Part::Chamfer] Chamfer007038015
  Base = -> Box186
  Edges = 2 edges r=3: [Edge4,Edge8]
FEATURE [Part::Box] Box189  label="Cube189"
  AttacherType = Attacher::AttachEngine3D
  Height = 5
  Length = 5
  Placement = pos=(487.5,-96,25) rot=(0,0,1;0rad)
  Width = 53
FEATURE [Part::Cylinder] Cylinder988  label="Cylinder1058"
  Angle = 360
  AttacherType = Attacher::AttachEngine3D
  Height = 56
  Placement = pos=(490,-99,30) rot=(-1,0,0;1.5708rad)
  Radius = 2.7
FEATURE [Part::MultiFuse] Fusion001005002004004005002010002003003003017007024041010023003003006006003006008021054006004013005009020003032  label="Fusion-289"
  Placement = pos=(-370,0,0) rot=(0,0,1;0rad)
  Refine = true
  Shapes = -> [Box189,Cylinder988]
FEATURE [Part::Cylinder] Cylinder989  label="Cylinder1059"
  Angle = 360
  AttacherType = Attacher::AttachEngine3D
  Height = 5
  Placement = pos=(70,-48,30) rot=(-1,0,0;1.5708rad)
  Radius = 3
FEATURE [Part::Cylinder] Cylinder990  label="Cylinder1060"
  Angle = 360
  AttacherType = Attacher::AttachEngine3D
  Height = 5
  Placement = pos=(90,-48,30) rot=(-1,0,0;1.5708rad)
  Radius = 1.6
FEATURE [Part::Cylinder] Cylinder991  label="Cylinder1061"
  Angle = 360
  AttacherType = Attacher::AttachEngine3D
  Height = 5
  Placement = pos=(110,-48,30) rot=(-1,0,0;1.5708rad)
  Radius = 3
FEATURE [Part::MultiFuse] Fusion001005002004004005002010002003003003017007024041010023003003006006003006008021054006004013005009020003033  label="Fusion-290"
  Refine = true
  Shapes = -> [Cylinder989,Cylinder991,Cylinder990]
FEATURE [Part::Box] Box190  label="Cube190"
  AttacherType = Attacher::AttachEngine3D
  Height = 5
  Length = 6
  Placement = pos=(67,-48,25) rot=(0,0,1;0rad)
  Width = 5
FEATURE [Part::Box] Box191  label="Cube191"
  AttacherType = Attacher::AttachEngine3D
  Height = 5
  Length = 6
  Placement = pos=(107,-48,25) rot=(0,0,1;0rad)
  Width = 5
FEATURE [Part::MultiFuse] Fusion001005002004004005002010002003003003017007024041010023003003006006003006008021054006004013005009020003034  label="Fusion-291"
  Refine = true
  Shapes = -> [Fusion001005002004004005002010002003003003017007024041010023003003006006003006008021054006004013005009020003033,Box190,Box191]
FEATURE [Part::Box] Box192  label="Cube192"
  AttacherType = Attacher::AttachEngine3D
  Height = 5
  Length = 8
  Placement = pos=(106,-96,25) rot=(0,0,1;0rad)
  Width = 10
FEATURE [Part::Box] Box193  label="Cube193"
  AttacherType = Attacher::AttachEngine3D
  Height = 5
  Length = 8
  Placement = pos=(66,-96,25) rot=(0,0,1;0rad)
  Width = 10
FEATURE [Part::Cylinder] Cylinder993  label="Cylinder1063"
  Angle = 360
  AttacherType = Attacher::AttachEngine3D
  Height = 10
  Placement = pos=(90,-96,30) rot=(-1,0,0;1.5708rad)
  Radius = 4
FEATURE [Part::Box] Box194  label="Cube194"
  AttacherType = Attacher::AttachEngine3D
  Height = 5
  Length = 8
  Placement = pos=(86,-96,25) rot=(0,0,1;0rad)
  Width = 10
FEATURE [Part::Cylinder] Cylinder992  label="Cylinder1062"
  Angle = 360
  AttacherType = Attacher::AttachEngine3D
  Height = 10
  Placement = pos=(110,-96,30) rot=(-1,0,0;1.5708rad)
  Radius = 4
FEATURE [Part::Cylinder] Cylinder994  label="Cylinder1064"
  Angle = 360
  AttacherType = Attacher::AttachEngine3D
  Height = 10
  Placement = pos=(70,-96,30) rot=(-1,0,0;1.5708rad)
  Radius = 4
FEATURE [Part::MultiFuse] Fusion001005002004004005002010002003003003017007024041010023003003006006003006008021054006004013005009020003035  label="Fusion-292"
  Refine = true
  Shapes = -> [Box193,Box192,Box194,Cylinder993,Cylinder992,Cylinder994]
FEATURE [Part::Box] Box195  label="Cube195"
  AttacherType = Attacher::AttachEngine3D
  Height = 8
  Length = 8
  Placement = pos=(76,-96,28) rot=(0,0,1;0rad)
  Width = 53
FEATURE [Part::Box] Box196  label="Cube196"
  AttacherType = Attacher::AttachEngine3D
  Height = 8
  Length = 8
  Placement = pos=(96,-96,28) rot=(0,0,1;0rad)
  Width = 53
FEATURE [Part::Box] Box197  label="Cube197"
  AttacherType = Attacher::AttachEngine3D
  Height = 5
  Length = 5
  Placement = pos=(130,-96,31) rot=(0,0,1;0rad)
  Width = 53
FEATURE [Part::MultiFuse] Fusion001005002004004005002010002003003003017007024041010023003003006006003006008021054006004013005009020003036  label="Fusion-293"
  Refine = true
  Shapes = -> [Box195,Box197,Box196,Chamfer007038015,Chamfer007038014]
FEATURE [Part::MultiFuse] Fusion001005002004004005002010002003003003017007024041010023003003006006003006008021054006004013005009020003037  label="Fusion-294"
  Refine = true
  Shapes = -> [Fusion001005002004004005002010002003003003017007024041010023003003006006003006008021054006004013005009020003035,Fusion001005002004004005002010002003003003017007024041010023003003006006003006008021054006004013005009020003034,Fusion001005002004004005002010002003003003017007024041010023003003006006003006008021054006004013005009020003032]
FEATURE [Part::Cut] Cut012035015003002009024006019011009006027002004  label="Cut-027"
  Base = -> Fusion001005002004004005002010002003003003017007024041010023003003006006003006008021054006004013005009020003036
  Refine = true
  Tool = -> Fusion001005002004004005002010002003003003017007024041010023003003006006003006008021054006004013005009020003037
FEATURE [Part::MultiFuse] Fusion001005002004004005002010002003003003017007024041010023003003006006003006008021054006004013005009020003038  label="Fusion-295"
  Refine = true
  Shapes = -> [Box187,Cut012035015003002009024006019011009006027002004]
FEATURE [Part::Chamfer] Chamfer007038016
  Base = -> Fusion001005002004004005002010002003003003017007024041010023003003006006003006008021054006004013005009020003038
  Edges = 2 edges: [Edge82 r1=0.5 r2=2.5,Edge144 r1=0.5 r2=2.5]
FEATURE [Part::Chamfer] Chamfer007038017
  Base = -> Chamfer007038016
  Edges = 2 edges: [Edge39 r1=2.5 r2=0.5,Edge154 r1=2.5 r2=0.5]
FEATURE [Part::Fillet] Fillet001025002
  Base = -> Chamfer007038017
  Edges = 10 edges r=0.5: [Edge53,Edge56,Edge66,Edge68,Edge141,Edge156,Edge160,Edge162,Edge163,Edge165]
FEATURE [Part::Cylinder] Cylinder995  label="Cylinder1065"
  Angle = 360
  AttacherType = Attacher::AttachEngine3D
  Height = 10
  Placement = pos=(129,-92,26) rot=(0,1,0;0rad)
  Radius = 0.9
FEATURE [Part::Feature] Fusion001005002004004005002010002003003003017007024041010023003003006006003006008021054006004013005009020003043002001  label="Fusion-304"
  shape: bbox 52 x 17 x 4 mm, 18 faces, 3 solids (baked)
FEATURE [Part::Feature] Fusion001005002004004005002010002003003003017007024041010023003003006006003006008021054006004013005009020003043002002  label="Fusion-305"
  shape: bbox 52 x 17 x 4 mm, 18 faces, 3 solids (baked)
FEATURE [Part::Box] Box199  label="Cube199"
  AttacherType = Attacher::AttachEngine3D
  Height = 8
  Length = 5
  Placement = pos=(130,-32.5,28) rot=(0,0,1;0rad)
  Width = 24.5
FEATURE [Part::MultiFuse] Fusion001005002004004005002010002003003003017007024041010023003003006006003006008021054006004013005009020003043002003  label="Fusion-306"
  Refine = true
  Shapes = -> [Cylinder974,Cylinder995]
FEATURE [Part::MultiFuse] Fusion001005002004004005002010002003003003017007024041010023003003006006003006008021054006004013005009020003043002004  label="Fusion-307"
  Refine = true
  Shapes = -> [Fillet001025002,Box199]
FEATURE [Part::Cut] Cut012035015003002009024006019011009006027002005  label="Cut-028"
  Base = -> Fusion001005002004004005002010002003003003017007024041010023003003006006003006008021054006004013005009020003043002004
  Refine = true
  Tool = -> Fusion001005002004004005002010002003003003017007024041010023003003006006003006008021054006004013005009020003043002003
FEATURE [Part::Cut] Cut012035015003002009024006019011009006027002006  label="Cut-029"
  Base = -> Cut012035015003002009024006019011009006027002005
  Refine = true
  Tool = -> Fusion001005002004004005002010002003003003017007024041010023003003006006003006008021054006004013005009020003043002002
FEATURE [Part::Box] Box200  label="Cube200"
  AttacherType = Attacher::AttachEngine3D
  Height = 10
  Length = 70
  Placement = pos=(65,-43.5,25) rot=(0,0,1;0rad)
  Width = 5
FEATURE [Part::Cut] Cut012035015003002009024006019011009006027002007  label="Cut-030"
  Base = -> Cut012035015003002009024006019011009006027002006
  Refine = true
  Tool = -> Box200
FEATURE [Part::Feature] Cut012035015003002009024006019011009006027002007001  label="Cut-031"
  shape: bbox 70 x 88 x 11 mm, 76 faces (baked)
FEATURE [Part::Mirroring] Part__Mirroring005002002002002002002002002014  label="Cut-031 (Mirror #7)"
  Base = (0,0,0)
  Normal = (0,1,0)
  Placement = pos=(0,-16,0) rot=(0,0,1;0rad)
  Source = -> Cut012035015003002009024006019011009006027002007001
FEATURE [Part::MultiFuse] Fusion001005002004004005002010002003003003017007024041010023003003006006003006008021054006004013005009020003043002005  label="plate-attach-front"
  Refine = true
  Shapes = -> [Cut012035015003002009024006019011009006027002007,Part__Mirroring005002002002002002002002002014]
FEATURE [Part::Cylinder] Cylinder996  label="Cylinder1066"
  Angle = 360
  AttacherType = Attacher::AttachEngine3D
  Height = 5
  Placement = pos=(120,-99,30) rot=(-1,0,0;1.5708rad)
  Radius = 2.8
FEATURE [Part::Cylinder] Cylinder997  label="Cylinder1067"
  Angle = 360
  AttacherType = Attacher::AttachEngine3D
  Height = 5
  Placement = pos=(490,-99,30) rot=(-1,0,0;1.5708rad)
  Radius = 2.8
FEATURE [Part::Cylinder] Cylinder998  label="Cylinder1068"
  Angle = 360
  AttacherType = Attacher::AttachEngine3D
  Height = 5
  Placement = pos=(403,-99,30) rot=(-1,0,0;1.5708rad)
  Radius = 2.8
FEATURE [Part::Cylinder] Cylinder999  label="Cylinder1069"
  Angle = 360
  AttacherType = Attacher::AttachEngine3D
  Height = 5
  Placement = pos=(317,-99,30) rot=(-1,0,0;1.5708rad)
  Radius = 2.8
FEATURE [Part::Cylinder] Cylinder1000  label="Cylinder1070"
  Angle = 360
  AttacherType = Attacher::AttachEngine3D
  Height = 5
  Placement = pos=(231,-99,30) rot=(-1,0,0;1.5708rad)
  Radius = 2.8
FEATURE [Part::MultiFuse] Fusion001005002004004005002010002003003003017007024041010023003003006006003006008021054006004013005009020003043002006  label="Fusion-308"
  Refine = true
  Shapes = -> [Cylinder996,Cylinder999,Cylinder997,Cylinder1000,Cylinder998]
FEATURE [Part::Cut] Cut012035015003002009024006019011009006027002007002  label="Cut-032"
  Base = -> Cut012006
  Refine = true
  Tool = -> Fusion001005002004004005002010002003003003017007024041010023003003006006003006008021054006004013005009020003043002006
FEATURE [Part::MultiFuse] Fusion001005002004004005002010002003003003017007024041010023003003006006003006008021054006004013005009020003043002007  label="Fusion-309"
  Refine = true
  Shapes = -> [Fusion001005002004004005002010002003003003017007024041010023003003006006003006008021054006004010,Fusion001005002004004005002010002003003003017007024041010023003003006006003006008021054006004013001,Fusion001005002004004005002010002003003003017007024041010023003003006006003006008021054006004013002,Fusion001005002004004005002010002003003003017007024041010023003003006006003006008021054006004013003,+1 more]
FEATURE [Part::Cut] Cut012035015003002009024006019011009006027002007003  label="Cut-033"
  Base = -> Cut012035015003002009024006019011009006027002007002
  Refine = true
  Tool = -> Fusion001005002004004005002010002003003003017007024041010023003003006006003006008021054006004013005009020003043002007
FEATURE [Part::Box] Box201  label="Cube201"
  AttacherType = Attacher::AttachEngine3D
  Height = 19
  Length = 11
  Placement = pos=(547,-101,2) rot=(0,0,1;0rad)
  Width = 5
FEATURE [Part::Feature] Face016
  shape: bbox 76.16 x 2e-07 x 40.23 mm, 1 faces, 0 solids (baked)
FEATURE [Part::Extrusion] Extrude018
  Base = -> Face016
  Dir = (0,1,0)
  DirMode = 0
  FaceMakerClass = Part::FaceMakerBullseye
  LengthFwd = 5
  LengthRev = 0
  Solid = true
  Symmetric = false
FEATURE [Part::Box] Box202  label="Cube202"
  AttacherType = Attacher::AttachEngine3D
  Height = 36
  Length = 53
  Placement = pos=(494,-101,2) rot=(0,0,1;0rad)
  Width = 5
FEATURE [Part::Cut] Cut012035015003002009024006019011009006027002007004  label="Cut-034"
  Base = -> Extrude014
  Refine = true
  Tool = -> Box201
FEATURE [Part::Cut] Cut012035015003002009024006019011009006027002007005  label="Cut-035"
  Base = -> Extrude018
  Refine = true
  Tool = -> Box202
FEATURE [Part::Chamfer] Chamfer007038019
  Base = -> Cut012035015003002009024006019011009006027002007004
  Edges = 1 edges r=0.6: [Edge10]
FEATURE [Part::MultiFuse] Fusion001005002004004005002010002003003003017007024041010023003003006006003006008021054006004013005009020003043002008  label="Fusion-310"
  Refine = true
  Shapes = -> [Chamfer007038019,Cut012035015003002009024006019011009006027002007005]
FEATURE [Part::Cut] Cut012035015003002009024006019011009006027002007006  label="Cut-036"
  Base = -> Fusion001005002004004005002010002003003003017007024041010023003003006006003006008021054006004013005009020003043002008
  Refine = true
  Tool = -> Cut012035015003002009024006019004
FEATURE [Part::MultiFuse] Fusion001005002004004005002010002003003003017007024041010023003003006006003006008021054006004013005009020003043002009  label="Fusion-311"
  Refine = true
  Shapes = -> [Cut012035015003002009024006019011001,Cut012035015003002009024006019011009006027002007006]
FEATURE [Part::Cut] Cut012035015003002009024006019011009006027002007007  label="Cut-037"
  Base = -> Fusion001005002004004005002010002003003003017007024041010023003003006006003006008021054006004013005009020003043002009
  Refine = true
  Tool = -> Fusion001005002004004005002010002003003003017007024041010023003003006006003006008021054005
FEATURE [Part::Box] Box203  label="Cube203"
  AttacherType = Attacher::AttachEngine3D
  Height = 15
  Length = 269
  Placement = pos=(226,-101,22) rot=(0,0,1;0rad)
  Width = 5
FEATURE [Part::Box] Box204  label="Cube204"
  AttacherType = Attacher::AttachEngine3D
  Height = 15
  Length = 161
  Placement = pos=(65,-101,22) rot=(0,0,1;0rad)
  Width = 5
FEATURE [Part::Box] Box205  label="Cube205"
  AttacherType = Attacher::AttachEngine3D
  Height = 15
  Length = 97
  Placement = pos=(398,-101,22) rot=(0,0,1;0rad)
  Width = 5
FEATURE [Part::MultiFuse] Fusion001005002004004005002010002003003003017007024041010023003003006006003006008021054006004013005009020003043002010  label="Fusion-312"
  Refine = true
  Shapes = -> [Box205,Box204]
FEATURE [Part::Box] Box206  label="Cube206"
  AttacherType = Attacher::AttachEngine3D
  Height = 15
  Length = 333
  Placement = pos=(65,-101,22) rot=(0,0,1;0rad)
  Width = 5
FEATURE [Part::Cylinder] Cylinder1001  label="Cylinder1071"
  Angle = 360
  AttacherType = Attacher::AttachEngine3D
  Height = 5
  Placement = pos=(546,-99,13) rot=(-1,0,0;1.5708rad)
  Radius = 2.8
FEATURE [Part::Cut] Cut012035015003002009024006019011009006027002007008  label="Cut-038"
  Base = -> Cut012035015003002009024006019011009006027002007007
  Refine = true
  Tool = -> Cylinder1001
FEATURE [Part::Chamfer] Chamfer007038020
  Base = -> Cut012035015003002009024006019011009006027002007003
  Edges = 1 edges r=0.6: [Edge46]
FEATURE [Part::Feature] Chamfer007038020001  label="Chamfer007038021"
  shape: bbox 430 x 5 x 15 mm, 56 faces (baked)
FEATURE [Part::Cut] Cut012035015003002009024006019011009006027002007009  label="border-lateral-1-left"
  Base = -> Chamfer007038020
  Refine = true
  Tool = -> Box203
FEATURE [Part::Cut] Cut012035015003002009024006019011009006027002007011  label="border-lateral-2-left"
  Base = -> Chamfer007038020001
  Refine = true
  Tool = -> Fusion001005002004004005002010002003003003017007024041010023003003006006003006008021054006004013005009020003043002010
FEATURE [Part::Feature] Cut012035015003002009024006019011009006027002007009001  label="border-lateral-1-left001"
  shape: bbox 161 x 5 x 15 mm, 21 faces (baked)
FEATURE [Part::Feature] Cut012035015003002009024006019011009006027002007011001  label="border-lateral-2-left001"
  shape: bbox 172 x 5 x 15 mm, 33 faces (baked)
FEATURE [Part::Mirroring] Part__Mirroring005002002002002002002002002015  label="border-lateral-1-right"
  Base = (0,0,0)
  Normal = (0,1,0)
  Placement = pos=(0,-16,0) rot=(0,0,1;0rad)
  Source = -> Cut012035015003002009024006019011009006027002007009001
FEATURE [Part::Mirroring] Part__Mirroring005002002002002002002002002016  label="border-lateral-2-right"
  Base = (0,0,0)
  Normal = (0,1,0)
  Placement = pos=(0,-16,0) rot=(0,0,1;0rad)
  Source = -> Cut012035015003002009024006019011009006027002007011001
FEATURE [Part::Feature] Chamfer007038020003  label="Chamfer007038023"
  shape: bbox 430 x 5 x 15 mm, 56 faces (baked)
FEATURE [Part::Cut] Cut012035015003002009024006019011009006027002007011002  label="Cut-039"
  Base = -> Chamfer007038020003
  Refine = true
  Tool = -> Box206
FEATURE [Part::MultiFuse] Fusion001005002004004005002010002003003003017007024041010023003003006006003006008021054006004013005009020003043002011002  label="border-lateral-3-left_OLD"
  Refine = true
  Shapes = -> [Cut012035015003002009024006019011009006027002007008,Cut012035015003002009024006019011009006027002007011002]
FEATURE [Part::Feature] Fusion001005002004004005002010002003003003017007024041010023003003006006003006008021054006004013005009020003043002011002001  label="border-lateral-3-left001"
  shape: bbox 168 x 5 x 40.23 mm, 57 faces (baked)
FEATURE [Part::Mirroring] Part__Mirroring005002002002002002002002002017  label="border-lateral-3-right_OLD"
  Base = (0,0,0)
  Normal = (0,1,0)
  Placement = pos=(0,-16,0) rot=(0,0,1;0rad)
  Source = -> Fusion001005002004004005002010002003003003017007024041010023003003006006003006008021054006004013005009020003043002011002001
FEATURE [Part::Box] Box209  label="Cube209"
  AttacherType = Attacher::AttachEngine3D
  Height = 150
  Length = 14
  Placement = pos=(555.2,-100,6) rot=(0,0,1;0rad)
  Width = 56
FEATURE [Part::Fillet] Fillet001025003
  Base = -> Box209
  Edges = 1 edges r=4.8: [Edge4]
  Placement = pos=(722.778,0,546.729) rot=(0,1,0;1.88496rad)
FEATURE [Part::Box] Box210  label="Cube210"
  AttacherType = Attacher::AttachEngine3D
  Height = 14
  Length = 5
  Placement = pos=(550.2,-100,0) rot=(0,0,1;0rad)
  Width = 56
FEATURE [Part::Cut] Cut012035015003002009024006019011009006027002007011003  label="Cut-040"
  Base = -> Fillet001025003
  Refine = true
  Tool = -> Box210
FEATURE [Part::Box] Box211  label="Cube211"
  AttacherType = Attacher::AttachEngine3D
  Height = 19
  Length = 17
  Placement = pos=(550.2,-100,-2) rot=(0,0,1;0rad)
  Width = 4.2
FEATURE [Part::Box] Box212  label="Cube212"
  AttacherType = Attacher::AttachEngine3D
  Height = 19
  Length = 17
  Placement = pos=(550.2,-48.2,-2) rot=(0,0,1;0rad)
  Width = 4.2
FEATURE [Part::MultiFuse] Fusion001005002004004005002010002003003003017007024041010023003003006006003006008021054006004013005009020003043002011002002  label="Fusion-313"
  Refine = true
  Shapes = -> [Box212,Box211]
FEATURE [Part::Cut] Cut012035015003002009024006019011009006027002007011004  label="Cut-041"
  Base = -> Cut012035015003002009024006019011009006027002007011003
  Refine = true
  Tool = -> Fusion001005002004004005002010002003003003017007024041010023003003006006003006008021054006004013005009020003043002011002002
FEATURE [Part::Chamfer] Chamfer007038020004
  Base = -> Cut012035015003002009024006019011009006027002007011004
  Edges = 1 edges: [Edge29 r1=2 r2=8]
FEATURE [Part::Box] Box213  label="Cube213"
  AttacherType = Attacher::AttachEngine3D
  Height = 15
  Length = 51
  Placement = pos=(654,-100,-45) rot=(0,0,1;0rad)
  Width = 56
FEATURE [Part::Cut] Cut012035015003002009024006019011009006027002007011005  label="Cut-042"
  Base = -> Chamfer007038020004
  Refine = true
  Tool = -> Box213
FEATURE [Part::Box] Box214  label="Cube214"
  AttacherType = Attacher::AttachEngine3D
  Height = 108.5
  Length = 14
  Placement = pos=(555,-81,11.5) rot=(0,1,0;1.88496rad)
  Width = 18
FEATURE [Part::Cut] Cut012035015003002009024006019011009006027002007011006  label="Cut-043"
  Base = -> Cut012035015003002009024006019011009006027002007011005
  Refine = true
  Tool = -> Box214
FEATURE [Part::Cylinder] Cylinder1002  label="Cylinder1072"
  Angle = 360
  AttacherType = Attacher::AttachEngine3D
  Height = 16
  Placement = pos=(568,-80,-7) rot=(-1,0,0;1.5708rad)
  Radius = 1.5
FEATURE [Part::Cylinder] Cylinder1003  label="Cylinder1073"
  Angle = 360
  AttacherType = Attacher::AttachEngine3D
  Height = 85
  Placement = pos=(568,-72,-12) rot=(-1,0,0;0rad)
  Radius = 5
FEATURE [Part::Cylinder] Cylinder1004  label="Cylinder1074"
  Angle = 360
  AttacherType = Attacher::AttachEngine3D
  Height = 85
  Placement = pos=(563.109,-72,-5.96044) rot=(0,1,0;1.78024rad)
  Radius = 5
FEATURE [Part::Cylinder] Cylinder1005  label="Cylinder1075"
  Angle = 360
  AttacherType = Attacher::AttachEngine3D
  Height = 125
  Placement = pos=(568,-72,-12) rot=(-1,0,0;0rad)
  Radius = 3
FEATURE [Part::Cylinder] Cylinder1006  label="Cylinder1076"
  Angle = 360
  AttacherType = Attacher::AttachEngine3D
  Height = 94
  Placement = pos=(563.109,-72,-5.96044) rot=(0,1,0;1.78024rad)
  Radius = 3
FEATURE [Part::MultiFuse] Fusion001005002004004005002010002003003003017007024041010023003003006006003006008021054006004013005009020003043002011002004  label="Fusion-315"
  Refine = true
  Shapes = -> [Cylinder1004,Cylinder1006]
FEATURE [Part::Cylinder] Cylinder1008  label="Cylinder1078"
  Angle = 360
  AttacherType = Attacher::AttachEngine3D
  Height = 15
  Placement = pos=(560,-96,10.8) rot=(-1,0,0;1.5708rad)
  Radius = 2.5
FEATURE [Part::Cylinder] Cylinder1009  label="Cylinder1079"
  Angle = 360
  AttacherType = Attacher::AttachEngine3D
  Height = 15
  Placement = pos=(560,-63,10.8) rot=(-1,0,0;1.5708rad)
  Radius = 2.5
FEATURE [Part::Cylinder] Cylinder1010  label="Cylinder1080"
  Angle = 360
  AttacherType = Attacher::AttachEngine3D
  Height = 48
  Placement = pos=(560,-96,10.8) rot=(-1,0,0;1.5708rad)
  Radius = 2
FEATURE [Part::MultiFuse] Fusion001005002004004005002010002003003003017007024041010023003003006006003006008021054006004013005009020003043002011002005  label="Fusion-316"
  Refine = true
  Shapes = -> [Cylinder1010,Cylinder1009,Cylinder1008]
FEATURE [Part::Cut] Cut012035015003002009024006019011009006027002007011007  label="Cut-044"
  Base = -> Cut012035015003002009024006019011009006027002007011006
  Refine = true
  Tool = -> Fusion001005002004004005002010002003003003017007024041010023003003006006003006008021054006004013005009020003043002011002005
FEATURE [Part::Box] Box215  label="Cube215"
  AttacherType = Attacher::AttachEngine3D
  Height = 157
  Length = 16
  Placement = pos=(555,-48.2,18.5) rot=(0,1,0;1.88496rad)
  Width = 4.2
FEATURE [Part::Box] Box216  label="Cube216"
  AttacherType = Attacher::AttachEngine3D
  Height = 157
  Length = 16
  Placement = pos=(555,-100,18.5) rot=(0,1,0;1.88496rad)
  Width = 4.2
FEATURE [Part::MultiFuse] Fusion001005002004004005002010002003003003017007024041010023003003006006003006008021054006004013005009020003043002011002006  label="Fusion-317"
  Refine = true
  Shapes = -> [Box216,Box215]
FEATURE [Part::Cut] Cut012035015003002009024006019011009006027002007011007002  label="Cut-046"
  Base = -> Cut012035015003002009024006019011009006027002007011007
  Refine = true
  Tool = -> Fusion001005002004004005002010002003003003017007024041010023003003006006003006008021054006004013005009020003043002011002006
FEATURE [Part::Cylinder] Cylinder1011  label="Cylinder1081"
  Angle = 360
  AttacherType = Attacher::AttachEngine3D
  Height = 59
  Placement = pos=(652,-101,-25) rot=(-1,0,0;1.5708rad)
  Radius = 1.5
FEATURE [Part::Cut] Cut012035015003002009024006019011009006027002007011007003  label="Cut-047"
  Base = -> Cut012035015003002009024006019011009006027002007011007002
  Refine = true
  Tool = -> Cylinder1011
FEATURE [Part::Feature] Face017
  shape: bbox 152.6 x 2e-07 x 60.33 mm, 1 faces, 0 solids (baked)
FEATURE [Part::Extrusion] Extrude019
  Base = -> Face017
  Dir = (0,1,0)
  DirMode = 0
  FaceMakerClass = Part::FaceMakerBullseye
  LengthFwd = 4.2
  LengthRev = 0
  Solid = false
  Symmetric = false
FEATURE [Part::Feature] Face018
  shape: bbox 136.8 x 2e-07 x 52.81 mm, 1 faces, 0 solids (baked)
FEATURE [Part::Extrusion] Extrude020
  Base = -> Face018
  Dir = (0,1,0)
  DirMode = 0
  FaceMakerClass = Part::FaceMakerBullseye
  LengthFwd = 1
  LengthRev = 0
  Solid = true
  Symmetric = false
FEATURE [Part::Cut] Cut012035015003002009024006019011009006027002007011007004  label="Cut-048"
  Base = -> Extrude019
  Placement = pos=(0.2,0,0) rot=(0,0,1;0rad)
  Refine = true
  Tool = -> Extrude020
FEATURE [Part::Feature] Fusion001005002004004005002010002003003003017007024041010023003003006006003006008021054006004013005009020003043002011002007  label="Fusion-318"
  Placement = pos=(570.5,-99,4) rot=(0,0,1;0rad)
  shape: bbox 4 x 17 x 4 mm, 6 faces (baked)
FEATURE [Part::Feature] Fusion001005002004004005002010002003003003017007024041010023003003006006003006008021054006004013005009020003043002011002008  label="Fusion-319"
  Placement = pos=(621,-99,-11) rot=(0,0,1;0rad)
  shape: bbox 4 x 17 x 4 mm, 6 faces (baked)
FEATURE [Part::Feature] Fusion001005002004004005002010002003003003017007024041010023003003006006003006008021054006004013005009020003043002011002009  label="Fusion-320"
  Placement = pos=(675,-99,-26) rot=(0,0,1;0rad)
  shape: bbox 4 x 17 x 4 mm, 6 faces (baked)
FEATURE [Part::Feature] Fusion001005002004004005002010002003003003017007024041010023003003006006003006008021054006004013005009020003043002011002010001  label="Fusion-322"
  Placement = pos=(0,-1,0) rot=(0,0,1;0rad)
  shape: bbox 104 x 17 x 34 mm, 18 faces, 3 solids (baked)
FEATURE [Part::Feature] Fusion001005002004004005002010002003003003017007024041010023003003006006003006008021054006004013005009020003043002011002010002  label="Fusion-323"
  shape: bbox 104 x 17 x 34 mm, 18 faces, 3 solids (baked)
FEATURE [Part::Mirroring] Part__Mirroring005002002002002002002002002018  label="Fusion-323 (Mirror #11)"
  Base = (0,0,0)
  Normal = (0,1,0)
  Placement = pos=(0,-143,0) rot=(0,0,1;0rad)
  Source = -> Fusion001005002004004005002010002003003003017007024041010023003003006006003006008021054006004013005009020003043002011002010002
FEATURE [Part::MultiFuse] Fusion001005002004004005002010002003003003017007024041010023003003006006003006008021054006004013005009020003043002011002010003  label="Fusion-324"
  Refine = true
  Shapes = -> [Part__Mirroring005002002002002002002002002018,Fusion001005002004004005002010002003003003017007024041010023003003006006003006008021054006004013005009020003043002011002010001]
FEATURE [Part::Cut] Cut012035015003002009024006019011009006027002007011007006  label="ramp-left-body_"
  Base = -> Cut012035015003002009024006019011009006027002007011007003
  Refine = true
  Tool = -> Fusion001005002004004005002010002003003003017007024041010023003003006006003006008021054006004013005009020003043002011002010003
FEATURE [Part::Box] Box218  label="Cube218"
  AttacherType = Attacher::AttachEngine3D
  Height = 11
  Length = 22
  Placement = pos=(555,-81,23.5) rot=(0,1,0;1.88496rad)
  Width = 18
FEATURE [Part::Cut] Cut012035015003002009024006019011009006027002007011007005002  label="Cut-052"
  Base = -> Cut012035015003002009024006019011009006027002007011007006
  Refine = true
  Tool = -> Box218
FEATURE [Part::Chamfer] Chamfer007038020005  label="ramp-left-body_001"
  Base = -> Cut012035015003002009024006019011009006027002007011007005002
  Edges = 1 edges r=2: [Edge35]
FEATURE [Part::Cone] Cone016
  Angle = 360
  AttacherType = Attacher::AttachEngine3D
  Height = 2
  Radius1 = 2.4
  Radius2 = 5.6
FEATURE [Part::Cone] Cone017
  Angle = 360
  AttacherType = Attacher::AttachEngine3D
  Height = 2
  Placement = pos=(0,0,2.5) rot=(0,0,1;0rad)
  Radius1 = 5.6
  Radius2 = 2.9
FEATURE [Part::Cylinder] Cylinder1012  label="Cylinder1082"
  Angle = 360
  AttacherType = Attacher::AttachEngine3D
  Height = 0.5
  Placement = pos=(0,0,2) rot=(0,0,1;0rad)
  Radius = 5.6
FEATURE [Part::Cylinder] Cylinder1013  label="Cylinder1083"
  Angle = 360
  AttacherType = Attacher::AttachEngine3D
  Height = 0.75
  Placement = pos=(0,0,4.5) rot=(0,0,1;0rad)
  Radius = 2.9
FEATURE [Part::Cylinder] Cylinder1014  label="Cylinder1084"
  Angle = 360
  AttacherType = Attacher::AttachEngine3D
  Height = 5.25
  Radius = 1.5
FEATURE [Part::MultiFuse] Fusion001005002004004005002010002003003003017007024041010023003003006006003006008021054006004013005009020003043002011002010005  label="Fusion0000"
  Refine = true
  Shapes = -> [Cone016,Cone017,Cylinder1012,Cylinder1013]
FEATURE [Part::Cut] Cut012035015003002009024006019011009006027002007011007005004  label="spur_gear_16T"
  Base = -> Fusion001005002004004005002010002003003003017007024041010023003003006006003006008021054006004013005009020003043002011002010005
  Refine = true
  Tool = -> Cylinder1014
FEATURE [Part::Feature] Cut012035015003002009024006019011009006027002007011007005004001  label="spur_gear_16T_A"
  Placement = pos=(8.25,5.25,0) rot=(1,0,0;1.5708rad)
  shape: bbox 11.2 x 5.25 x 11.2 mm, 7 faces (baked)
FEATURE [Part::Feature] Cut012035015003002009024006019011009006027002007011007005004002  label="spur_gear_16T_B"
  Placement = pos=(5.25,8.25,0) rot=(0,-1,0;1.5708rad)
  shape: bbox 5.25 x 11.2 x 11.2 mm, 7 faces (baked)
FEATURE [Part::MultiFuse] Fusion001005002004004005002010002003003003017007024041010023003003006006003006008021054006004013005009020003043002011002010006  label="spur_gears_16T_90"
  Refine = true
  Shapes = -> [Cut012035015003002009024006019011009006027002007011007005004001,Cut012035015003002009024006019011009006027002007011007005004002]
FEATURE [Part::Feature] Fusion001005002004004005002010002003003003017007024041010023003003006006003006008021054006004013005009020003043002011002010006001  label="spur_gears_16T_90_left"
  Placement = pos=(552.75,-44,9.2) rot=(0,0,1;0rad)
  shape: bbox 13.85 x 13.85 x 11.2 mm, 18 faces (baked)
FEATURE [Part::Cylinder] Cylinder029
  Angle = 360
  AttacherType = Attacher::AttachEngine3D
  Height = 16
  Radius = 8
FEATURE [Part::Cylinder] Cylinder024
  Angle = 360
  AttacherType = Attacher::AttachEngine3D
  Height = 30
  Radius = 8
FEATURE [Part::Cylinder] Cylinder028
  Angle = 360
  AttacherType = Attacher::AttachEngine3D
  Height = 30
  Radius = 8
FEATURE [Part::Box] Box017  label="Cube221"
  AttacherType = Attacher::AttachEngine3D
  Height = 30
  Length = 10.4
  Placement = pos=(-5.2,-6.2,0) rot=(0,0,1;0rad)
  Width = 12.4
FEATURE [Part::Cylinder] Cylinder030
  Angle = 360
  AttacherType = Attacher::AttachEngine3D
  Height = 16
  Radius = 6.5
FEATURE [Part::Cut] Cut025
  Base = -> Cylinder029
  Refine = true
  Tool = -> Cylinder030
FEATURE [Part::Fillet] Fillet004
  Base = -> Box017
  Edges = 4 edges r=1: [Edge1,Edge3,Edge5,Edge7]
FEATURE [Part::Cut] Cut026
  Base = -> Cylinder028
  Refine = true
  Tool = -> Fillet004
FEATURE [Part::MultiFuse] Fusion010
  Refine = true
  Shapes = -> [Cut025,Cut026]
FEATURE [Part::Cut] Cut027  label="MOTOR"
  Base = -> Cylinder024
  Refine = true
  Tool = -> Fusion010
FEATURE [Part::Cylinder] Cylinder123
  Angle = 360
  AttacherType = Attacher::AttachEngine3D
  Height = 39
  Radius = 1.5
FEATURE [Part::MultiFuse] Fusion051  label="motor_12V_20RPM"
  Refine = true
  Shapes = -> [Cut027,Cylinder123]
FEATURE [Part::Feature] Fusion051001  label="motor_12V_20RPM_left"
  Placement = pos=(519,-35.75,9.2) rot=(0,1,0;1.5708rad)
  shape: bbox 38 x 12.4 x 10.4 mm, 20 faces (baked)
FEATURE [Part::Box] Box220  label="Cube222"
  AttacherType = Attacher::AttachEngine3D
  Height = 14
  Length = 150
  Placement = pos=(555.5,-95.8,1.2) rot=(0,0,1;0rad)
  Width = 47.6
FEATURE [Part::Box] Box224  label="Cube226"
  AttacherType = Attacher::AttachEngine3D
  Height = 17
  Length = 63
  Placement = pos=(643,-100,-47) rot=(0,0,1;0rad)
  Width = 56
FEATURE [Part::Box] Box225  label="Cube227"
  AttacherType = Attacher::AttachEngine3D
  Height = 14
  Length = 108.3
  Placement = pos=(555,-81,-4.5) rot=(0,1,0;0rad)
  Width = 18
FEATURE [Part::Cylinder] Cylinder1015  label="Cylinder1085"
  Angle = 360
  AttacherType = Attacher::AttachEngine3D
  Height = 48.5
  Placement = pos=(561,-96,9.2) rot=(-1,0,0;1.5708rad)
  Radius = 2
FEATURE [Part::Box] Box228  label="Cube230"
  AttacherType = Attacher::AttachEngine3D
  Height = 11
  Length = 22
  Placement = pos=(550.885,-81,20.8842) rot=(0,1,0;1.5708rad)
  Width = 18
FEATURE [Part::Cylinder] Cylinder1019  label="Cylinder1089"
  Angle = 360
  AttacherType = Attacher::AttachEngine3D
  Height = 48
  Placement = pos=(561.2,-96,9.2) rot=(-1,0,0;1.5708rad)
  Radius = 1.5
FEATURE [Part::Feature] Fusion001005002004004005002010002003003003017007024041010023003003006006003006008021054006004013005009020003043002011002010006008  label="motor_12V_20RPM_left001"
  Placement = pos=(597.14,-56.5,-2.54265) rot=(0,-1,0;1.25664rad)
  shape: bbox 38.21 x 12.4 x 18.85 mm, 20 faces (baked)
FEATURE [Part::Feature] Fusion001005002004004005002010002003003003017007024041010023003003006006003006008021054006004013005009020003043002011002010006009  label="spur_gears_16T_90_left001"
  Placement = pos=(568.846,-63,6.65061) rot=(0,1,0;3.45575rad)
  shape: bbox 14.34 x 13.85 x 12.63 mm, 18 faces (baked)
FEATURE [Part::Mirroring] Part__Mirroring005002002002002002002002002021  label="spur_gears_16T_90_left001 (Mirror #14)"
  Base = (0,0,0)
  Normal = (0,1,0)
  Placement = pos=(0,-111.25,0) rot=(0,0,1;0rad)
  Source = -> Fusion001005002004004005002010002003003003017007024041010023003003006006003006008021054006004013005009020003043002011002010006009
FEATURE [Part::Feature] Fusion001005002004004005002010002003003003017007024041010023003003006006003006008021054006004013005009020003043002011002010006010  label="motor_12V_20RPM_left002"
  Placement = pos=(599.993,-56.5,-3.4697) rot=(0,-1,0;1.25664rad)
  shape: bbox 38.21 x 12.4 x 18.85 mm, 20 faces (baked)
FEATURE [Part::Cone] Cone018
  Angle = 360
  AttacherType = Attacher::AttachEngine3D
  Height = 1.5
  Radius1 = 1.9
  Radius2 = 4.5
FEATURE [Part::Cone] Cone019
  Angle = 360
  AttacherType = Attacher::AttachEngine3D
  Height = 1.5
  Placement = pos=(0,0,1.75) rot=(0,0,1;0rad)
  Radius1 = 4.5
  Radius2 = 2.9
FEATURE [Part::Cylinder] Cylinder1020  label="Cylinder1090"
  Angle = 360
  AttacherType = Attacher::AttachEngine3D
  Height = 0.25
  Placement = pos=(0,0,1.5) rot=(0,0,1;0rad)
  Radius = 4.5
FEATURE [Part::Cylinder] Cylinder1021  label="Cylinder1091"
  Angle = 360
  AttacherType = Attacher::AttachEngine3D
  Height = 1
  Placement = pos=(0,0,3.25) rot=(0,0,1;0rad)
  Radius = 2.5
FEATURE [Part::Cylinder] Cylinder1022  label="Cylinder1092"
  Angle = 360
  AttacherType = Attacher::AttachEngine3D
  Height = 5.25
  Radius = 1.5
FEATURE [Part::MultiFuse] Fusion001005002004004005002010002003003003017007024041010023003003006006003006008021054006004013005009020003043002011002010006011  label="Fusion0001"
  Refine = true
  Shapes = -> [Cone018,Cone019,Cylinder1020,Cylinder1021]
FEATURE [Part::Cut] Cut012035015003002009024006019011009006027002007011007005004011002  label="spur_gear_12T"
  Base = -> Fusion001005002004004005002010002003003003017007024041010023003003006006003006008021054006004013005009020003043002011002010006011
  Refine = true
  Tool = -> Cylinder1022
FEATURE [Part::Feature] Cut012035015003002009024006019011009006027002007011007005004011002001  label="spur_gear_12T001"
  Placement = pos=(4.25,7.25,0) rot=(0,-1,0;1.5708rad)
  shape: bbox 4.25 x 9 x 9 mm, 8 faces (baked)
FEATURE [Part::Feature] Cut012035015003002009024006019011009006027002007011007005004011002002  label="spur_gear_16T001"
  Placement = pos=(8,5.25,0) rot=(1,0,0;1.5708rad)
  shape: bbox 11.2 x 5.25 x 11.2 mm, 7 faces (baked)
FEATURE [Part::MultiFuse] Fusion001005002004004005002010002003003003017007024041010023003003006006003006008021054006004013005009020003043002011002010006012  label="spur_gears_16T-12T"
  Refine = true
  Shapes = -> [Cut012035015003002009024006019011009006027002007011007005004011002001,Cut012035015003002009024006019011009006027002007011007005004011002002]
FEATURE [Part::Cylinder] Cylinder1023  label="Cylinder1093"
  Angle = 360
  AttacherType = Attacher::AttachEngine3D
  Height = 5.75
  Placement = pos=(-5.75,7.25,0) rot=(0,1,0;1.5708rad)
  Radius = 3
FEATURE [Part::Feature] Fusion051004  label="motor_12V_20RPM003"
  Placement = pos=(-34.75,7.25,0) rot=(0,1,0;1.5708rad)
  shape: bbox 39 x 12.4 x 10.4 mm, 20 faces (baked)
FEATURE [Part::Compound] Compound  label="motor_12V_ramp_shape"
  Links = -> [Fusion051004,Cylinder1023]
FEATURE [Part::Box] Box230  label="Cube232"
  AttacherType = Attacher::AttachEngine3D
  Height = 10
  Length = 10
  Placement = pos=(55,-86,25) rot=(0,0,1;0rad)
  Width = 40
FEATURE [Part::Box] Box231  label="Cube233"
  AttacherType = Attacher::AttachEngine3D
  Height = 10
  Length = 10
  Placement = pos=(55,30,25) rot=(0,0,1;0rad)
  Width = 40
FEATURE [Part::MultiFuse] Fusion001005002004004005002010002003003003017007024041010023003003006006003006008021054006004013005009020003043002011002010006014  label="Fusion-0000"
  Refine = true
  Shapes = -> [Box231,Box230]
FEATURE [Part::Cut] Cut012035015003002009024006019011009006027002007011007005004011002003  label="upper-plate-front-slope"
  Base = -> Cut012035015003002009024006004
  Refine = true
  Tool = -> Fusion001005002004004005002010002003003003017007024041010023003003006006003006008021054006004013005009020003043002011002010006014
FEATURE [Part::Box] Box232  label="Cube234"
  AttacherType = Attacher::AttachEngine3D
  Height = 1
  Length = 10.6
  Placement = pos=(541.7,-77.3,-23) rot=(0,0,1;0rad)
  Width = 10.6
FEATURE [Part::Box] Box233  label="Cube235"
  AttacherType = Attacher::AttachEngine3D
  Height = 3
  Length = 16
  Placement = pos=(539,-80,-25) rot=(0,0,1;0rad)
  Width = 16
FEATURE [Part::Cut] Cut012035015003002009024006019011009006027002007011007005004011002004  label="Cut-0000"
  Base = -> Box233
  Refine = true
  Tool = -> Box232
FEATURE [Part::Chamfer] Chamfer007038020008
  Base = -> Cut012035015003002009024006019011009006027002007011007005004011002004
  Edges = 1 edges r=2: [Edge16]
FEATURE [Part::Fillet] Fillet001025005
  Base = -> Chamfer007038020008
  Edges = 4 edges r=3: [Edge3,Edge4,Edge12,Edge14]
FEATURE [Part::Cylinder] Cylinder1025  label="Cylinder1095"
  Angle = 360
  AttacherType = Attacher::AttachEngine3D
  Height = 16
  Placement = pos=(547,-80,-25) rot=(-1,0,0;0rad)
  Radius = 1.25
FEATURE [Part::Cone] Cone020
  Angle = 360
  AttacherType = Attacher::AttachEngine3D
  Height = 2
  Placement = pos=(547,-80,-25) rot=(0,0,1;0rad)
  Radius1 = 3.2
  Radius2 = 1.6
FEATURE [Part::Cylinder] Cylinder1026  label="Cylinder1096"
  Angle = 360
  AttacherType = Attacher::AttachEngine3D
  Height = 3
  Placement = pos=(547,-80,-25) rot=(-1,0,0;0rad)
  Radius = 1.6
FEATURE [Part::MultiFuse] Fusion001005002004004005002010002003003003017007024041010023003003006006003006008021054006004013005009020003043002011002010006015  label="Fusion-0001"
  Placement = pos=(0,8,0) rot=(0,0,1;0rad)
  Refine = true
  Shapes = -> [Cylinder1025,Cone020,Cylinder1026]
FEATURE [Part::Cut] Cut012035015003002009024006019011009006027002007011007005004011002005  label="rear-stabilizer-foot-left"
  Base = -> Fillet001025005
  Placement = pos=(0,0,-3) rot=(0,0,1;0rad)
  Refine = true
  Tool = -> Fusion001005002004004005002010002003003003017007024041010023003003006006003006008021054006004013005009020003043002011002010006015
FEATURE [Part::Box] Box235  label="Cube237"
  AttacherType = Attacher::AttachEngine3D
  Height = 36.75
  Length = 15.25
  Placement = pos=(537,-77.5,-23) rot=(0,0,1;0rad)
  Width = 11
FEATURE [Part::Chamfer] Chamfer007038020009
  Base = -> Box235
  Edges = 1 edges: [Edge6 r1=8.5 r2=1]
  Placement = pos=(0,0,-3) rot=(0,0,1;0rad)
FEATURE [Part::Cylinder] Cylinder1027  label="Cylinder1097"
  Angle = 360
  AttacherType = Attacher::AttachEngine3D
  Height = 16
  Placement = pos=(547,-80,6) rot=(-1,0,0;1.5708rad)
  Radius = 1.5
FEATURE [Part::Feature] Fusion001005002004004005002010002003003003017007024041010023003003006006003006008021054006004013005009020003043002011002010006015002001  label="Fusion-0003"
  Placement = pos=(542,0,553) rot=(0,1,0;1.5708rad)
  shape: bbox 32 x 138 x 10 mm, 19 faces (baked)
FEATURE [Part::Cylinder] Cylinder1029  label="Cylinder1099"
  Angle = 360
  AttacherType = Attacher::AttachEngine3D
  Height = 138
  Placement = pos=(549.5,-77,-6) rot=(-1,0,0;1.5708rad)
  Radius = 1.5
FEATURE [Part::Cylinder] Cylinder1030  label="Cylinder1100"
  Angle = 46
  AttacherType = Attacher::AttachEngine3D
  Height = 7
  Placement = pos=(0,0,0) rot=(0,0,-1;1.97222rad)
  Radius = 79
FEATURE [Part::Cylinder] Cylinder1031  label="Cylinder1101"
  Angle = 44
  AttacherType = Attacher::AttachEngine3D
  Height = 7
  Placement = pos=(0,0,0) rot=(0,0,-1;1.95477rad)
  Radius = 79
FEATURE [Part::Cylinder] Cylinder1032  label="Cylinder1102"
  Angle = 57.75
  AttacherType = Attacher::AttachEngine3D
  Height = 7
  Placement = pos=(0,0,0) rot=(0,0,-1;2.0464rad)
  Radius = 78
FEATURE [Part::Cylinder] Cylinder1033  label="Cylinder1103"
  Angle = 36
  AttacherType = Attacher::AttachEngine3D
  Height = 7
  Placement = pos=(0,0,0) rot=(0,0,-1;1.88496rad)
  Radius = 80
FEATURE [Part::Cut] Cut012035015003002009024006019011009006027002007011007005004011002010  label="Cut-0005"
  Base = -> Cylinder1033
  Placement = pos=(0,-31,0) rot=(0,0,1;0rad)
  Refine = true
  Tool = -> Cylinder1030
FEATURE [Part::Cylinder] Cylinder1034  label="Cylinder1104"
  Angle = 46
  AttacherType = Attacher::AttachEngine3D
  Height = 7
  Placement = pos=(0,0,0) rot=(0,0,-1;1.97222rad)
  Radius = 78
FEATURE [Part::Cut] Cut012035015003002009024006019011009006027002007011007005004011002011  label="Cut-0006"
  Base = -> Cylinder1031
  Placement = pos=(0,-30.5,0) rot=(0,0,1;0rad)
  Refine = true
  Tool = -> Cylinder1034
FEATURE [Part::Cylinder] Cylinder1035  label="Cylinder1105"
  Angle = 59
  AttacherType = Attacher::AttachEngine3D
  Height = 7
  Placement = pos=(0,0,0) rot=(0,0,-1;2.05949rad)
  Radius = 77
FEATURE [Part::Cut] Cut012035015003002009024006019011009006027002007011007005004011002009  label="Cut-0007"
  Base = -> Cylinder1032
  Placement = pos=(0,-30,0) rot=(0,0,1;0rad)
  Refine = true
  Tool = -> Cylinder1035
FEATURE [Part::MultiFuse] Fusion001005002004004005002010002003003003017007024041010023003003006006003006008021054006004013005009020003043002011002010006015002002  label="Fusion-0004"
  Placement = pos=(0,-36,111.5) rot=(1,0,0;1.5708rad)
  Refine = true
  Shapes = -> [Cut012035015003002009024006019011009006027002007011007005004011002010,Cut012035015003002009024006019011009006027002007011007005004011002011,Cut012035015003002009024006019011009006027002007011007005004011002009]
FEATURE [Part::Cylinder] Cylinder1036  label="Cylinder1106"
  Angle = 360
  AttacherType = Attacher::AttachEngine3D
  Height = 7
  Placement = pos=(-34.1,-43,15.25) rot=(-1,0,0;1.5708rad)
  Radius = 3.5
FEATURE [Part::Box] Box236  label="Cube238"
  AttacherType = Attacher::AttachEngine3D
  Height = 4.3
  Length = 14
  Placement = pos=(-7,-43,-9) rot=(0,0,1;0rad)
  Width = 7
FEATURE [Part::Cylinder] Cylinder1037  label="Cylinder1107"
  Angle = 360
  AttacherType = Attacher::AttachEngine3D
  Height = 7
  Placement = pos=(-34.1,-43,15.25) rot=(-1,0,0;1.5708rad)
  Radius = 1.5
FEATURE [Part::Box] Box237  label="Cube239"
  AttacherType = Attacher::AttachEngine3D
  Height = 1
  Length = 8.5
  Placement = pos=(-4.25,-43,-9) rot=(0,0,1;0rad)
  Width = 7
FEATURE [Part::MultiFuse] Fusion001005002004004005002010002003003003017007024041010023003003006006003006008021054006004013005009020003043002011002010006015002003  label="Fusion-0005"
  Refine = true
  Shapes = -> [Fusion001005002004004005002010002003003003017007024041010023003003006006003006008021054006004013005009020003043002011002010006015002002,Cylinder1036]
FEATURE [Part::Cut] Cut012035015003002009024006019011009006027002007011007005004011002012  label="Cut-0008"
  Base = -> Fusion001005002004004005002010002003003003017007024041010023003003006006003006008021054006004013005009020003043002011002010006015002003
  Placement = pos=(0,0,-9.5) rot=(0,0,1;0rad)
  Refine = true
  Tool = -> Cylinder1037
FEATURE [Part::MultiFuse] Fusion001005002004004005002010002003003003017007024041010023003003006006003006008021054006004013005009020003043002011002010006015002004  label="Fusion-0006"
  Refine = true
  Shapes = -> [Box236,Cut012035015003002009024006019011009006027002007011007005004011002012]
FEATURE [Part::Cut] Cut012035015003002009024006019011009006027002007011007005004011002013  label="Cut-0009"
  Base = -> Fusion001005002004004005002010002003003003017007024041010023003003006006003006008021054006004013005009020003043002011002010006015002004
  Refine = true
  Tool = -> Box237
FEATURE [Part::Box] Box238  label="Cube240"
  AttacherType = Attacher::AttachEngine3D
  Height = 2
  Length = 2
  Placement = pos=(-6.25,-43,-10) rot=(0,0,1;0rad)
  Width = 7
FEATURE [Part::Box] Box239  label="Cube241"
  AttacherType = Attacher::AttachEngine3D
  Height = 2
  Length = 2
  Placement = pos=(4.25,-43,-10) rot=(0,0,1;0rad)
  Width = 7
FEATURE [Part::MultiFuse] Fusion001005002004004005002010002003003003017007024041010023003003006006003006008021054006004013005009020003043002011002010006015002005  label="Fusion-0007"
  Refine = true
  Shapes = -> [Box238,Box239]
FEATURE [Part::Chamfer] Chamfer007038020010
  Base = -> Fusion001005002004004005002010002003003003017007024041010023003003006006003006008021054006004013005009020003043002011002010006015002005
  Edges = 2 edges r=1: [Edge4,Edge20]
FEATURE [Part::MultiFuse] Fusion001005002004004005002010002003003003017007024041010023003003006006003006008021054006004013005009020003043002011002010006015002006  label="Fusion-0008"
  Refine = true
  Shapes = -> [Cut012035015003002009024006019011009006027002007011007005004011002013,Chamfer007038020010]
FEATURE [Part::Fillet] Fillet001025008  label="axle-leafspring-left"
  Base = -> Fusion001005002004004005002010002003003003017007024041010023003003006006003006008021054006004013005009020003043002011002010006015002006
  Edges = 1 edges r=3: [Edge33]
FEATURE [Part::Feature] Fillet001025008001  label="axle-leafspring-right"
  Placement = pos=(0,63,0) rot=(0,0,1;0rad)
  shape: bbox 77.19 x 7.643 x 19.25 mm, 38 faces (baked)
FEATURE [Part::MultiFuse] Fusion001005002004004005002010002003003003017007024041010023003003006006003006008021  label="Fusion-155"
  Refine = true
  Shapes = -> [Fusion001005002004004005002010002003003003017007024041010023003003006006003006008017,Fusion001005002004004005002010002003003003017007024041010023003003006006003006008020,Fusion001005002004004005002010002003003003017007024041010023003003006006003006008019,Fusion001005002004004005002010002003003003017007024041010023003003006006003006008018]
FEATURE [Part::MultiFuse] Fusion001005002004004005002010002003003003017007024030  label="Fusion-054"
  Refine = true
  Shapes = -> [Box055,Box053,Box054]
FEATURE [Part::Cut] Cut012035006
  Base = -> Fusion001005002004004005002010002003003003017007024030
  Refine = true
  Tool = -> Box056
FEATURE [Part::Fillet] Fillet001014
  Base = -> Cut012035006
  Edges = 3 edges r=3: [Edge4,Edge13,Edge16]
FEATURE [Part::Chamfer] Chamfer007005
  Base = -> Fillet001014
  Edges = 1 edges: [Edge30 r1=11 r2=6]
FEATURE [Part::Fillet] Fillet001015
  Base = -> Chamfer007005
  Edges = 1 edges r=3: [Edge12]
  Placement = pos=(-1,0,0) rot=(0,0,1;0rad)
FEATURE [Part::MultiFuse] Fusion001005002004004005002010002003003003017007024041010023003003006006003006008021054006004013005009020003043002011002010006015002007  label="Fusion-0009"
  Refine = true
  Shapes = -> [Cylinder745,Fillet001015,Box062]
FEATURE [Part::Cut] Cut012035015003002009024006019011009006027002007011007005004011002014  label="Cut-0010"
  Base = -> Fusion001005002004004005002010002003003003017007024041010023003003006006003006008021054006004013005009020003043002011002010006015002007
  Refine = true
  Tool = -> Cylinder723
FEATURE [Part::MultiFuse] Fusion001005002004004005002010002003003003017007024041010023003003006006003006008021054006004013005009020003043002011002010006015002008  label="Fusion-0010"
  Refine = true
  Shapes = -> [Fillet001012,Cut012035015003002009024012,Cut012035015003002009024006019011009006027002007011007005004011002014]
FEATURE [Part::Cut] Cut012035015003002009024006019011009006027002007011007005004011002015  label="Cut-0011"
  Base = -> Fusion001005002004004005002010002003003003017007024041010023003003006006003006008021054006004013005009020003043002011002010006015002008
  Refine = true
  Tool = -> Box086
FEATURE [Part::Chamfer] Chamfer007038020011
  Base = -> Cut012035015003002009024006019011009006027002007011007005004011002015
  Edges = 1 edges: [Edge54 r1=3 r2=25]
FEATURE [Part::Chamfer] Chamfer007038020012
  Base = -> Chamfer007038020011
  Edges = 1 edges: [Edge80 r1=3 r2=17]
FEATURE [Part::Chamfer] Chamfer007038020013
  Base = -> Chamfer007038020012
  Edges = 2 edges r=2: [Edge11,Edge58]
FEATURE [Part::Cut] Cut012035015003002009024006019011009006027002007011007005004011002016  label="Cut-0012"
  Base = -> Chamfer007038020013
  Refine = true
  Tool = -> Fusion001005002004004005002010002003003003017007024041010023003003006006003006008021
FEATURE [Part::MultiFuse] Fusion001005002004004005002010002003003003017007024041010023003003006006003006008021054006004013005009020003043002011002010006015002009  label="rotation-leafspring-attach-left"
  Refine = true
  Shapes = -> [Cut012035015003002009024006019011009006027002007011007005004011002016,Cut012035010]
FEATURE [Part::Feature] Part__Mirroring005002002002002002002002002022001  label="rotation-leafspring-attach-right"
  Placement = pos=(0,-16,0) rot=(0,0,1;0rad)
  shape: bbox 88 x 13 x 40 mm, 68 faces (baked)
FEATURE [Part::Feature] Fusion001005002004004005002010002003003003017007024041010023003003006006003006008021054006004013005009020003043002011002010006015002010001  label="axle-second"
  Placement = pos=(274,0,0) rot=(0,0,1;0rad)
  shape: bbox 77.19 x 164 x 19.25 mm, 267 faces, 7 solids (baked)
FEATURE [Part::Feature] Fusion001005002004004005002010002003003003017007024041010023003003006006003006008021054006004013005009020003043002011002010006015002010002  label="axle-third"
  Placement = pos=(360,0,0) rot=(0,0,1;0rad)
  shape: bbox 77.19 x 164 x 19.25 mm, 267 faces, 7 solids (baked)
FEATURE [Part::Feature] Fusion001005002004004005002010002003003003017007024041010023003003006006003006008021054006004013005009020003043002011002010006015002010003  label="axle-fourth"
  Placement = pos=(446,0,0) rot=(0,0,1;0rad)
  shape: bbox 77.19 x 164 x 19.25 mm, 267 faces, 7 solids (baked)
FEATURE [Part::Chamfer] Chamfer007038020014
  Base = -> Fusion001005002004004005002010002003003003017007024041010023003003006006003006008021025
  Edges = 2 edges: [Edge42 r1=25 r2=1.5,Edge94 r1=25 r2=1.5]
FEATURE [Part::Cut] Cut012035015003002009024006019011009006027002007011007005004011002017  label="leafspring-attach-rear-fourth-left"
  Base = -> Chamfer007038020014
  Placement = pos=(-4,0,0) rot=(0,0,1;0rad)
  Refine = true
  Tool = -> Fusion001005002004004005002010002003003003017007024041010023003003006006003006008021029
FEATURE [Part::Feature] Cut012035015003002009024006019011009006027002007011007005004011002017001  label="leafspring-attach-rear-third-left"
  Placement = pos=(-90,0,0) rot=(0,0,1;0rad)
  shape: bbox 78 x 13 x 39 mm, 53 faces (baked)
FEATURE [Part::Feature] Cut012035015003002009024006019011009006027002007011007005004011002017002  label="leafspring-attach-rear-second-left"
  Placement = pos=(-176,0,0) rot=(0,0,1;0rad)
  shape: bbox 78 x 13 x 39 mm, 53 faces (baked)
FEATURE [Part::Feature] Part__Mirroring005002002002002002002002002022002001  label="leafspring-attach-rear-fourth-right"
  Placement = pos=(-4,-16,0) rot=(0,0,1;0rad)
  shape: bbox 78 x 13 x 39 mm, 53 faces (baked)
FEATURE [Part::Feature] Part__Mirroring005002002002002002002002002022004001  label="leafspring-attach-rear-third-right"
  Placement = pos=(-90,-16,0) rot=(0,0,1;0rad)
  shape: bbox 78 x 13 x 39 mm, 53 faces (baked)
FEATURE [Part::Feature] Part__Mirroring005002002002002002002002002022003001  label="leafspring-attach-rear-second-right"
  Placement = pos=(-176,-16,0) rot=(0,0,1;0rad)
  shape: bbox 78 x 13 x 39 mm, 53 faces (baked)
FEATURE [App::DocumentObjectGroup] Group002  label="Rear Wheels"
  Group = -> [Fusion001005002004004005002010002003003003002,Fusion001005002004004005002010002003003003003,Fusion001005002004004005002010002003003003004,Fusion001005002004004005002010002003003003017007024041010023003003006006003006008021054006004013005009020003043002011002010006015002010001,+8 more]
FEATURE [Part::Cylinder] Cylinder1038  label="Cylinder1108"
  Angle = 360
  AttacherType = Attacher::AttachEngine3D
  Height = 3
  Placement = pos=(-138,-8,0) rot=(0,-1,0;1.5708rad)
  Radius = 3
FEATURE [Part::Cylinder] Cylinder1039  label="Cylinder1109"
  Angle = 360
  AttacherType = Attacher::AttachEngine3D
  Height = 28
  Placement = pos=(-138,-8,0) rot=(0,-1,0;1.5708rad)
  Radius = 1.5
FEATURE [Part::MultiFuse] Fusion001005002004004005002010002003003003017007024041010023003003006006003006008021054006004013005009020003043002011002010006015002010004  label="screw-hex-3x28"
  Placement = pos=(-2,0,0) rot=(0,0,1;0rad)
  Refine = true
  Shapes = -> [Cylinder1039,Cylinder1038]
FEATURE [Part::Cylinder] Cylinder1040  label="Cylinder1110"
  Angle = 360
  AttacherType = Attacher::AttachEngine3D
  Height = 3
  Placement = pos=(-138,-8,0) rot=(0,-1,0;1.5708rad)
  Radius = 3
FEATURE [Part::Cylinder] Cylinder1041  label="Cylinder1111"
  Angle = 360
  AttacherType = Attacher::AttachEngine3D
  Height = 33
  Placement = pos=(-138,-8,0) rot=(0,-1,0;1.5708rad)
  Radius = 1.5
FEATURE [Part::MultiFuse] Fusion001005002004004005002010002003003003017007024041010023003003006006003006008021054006004013005009020003043002011002010006015002010005  label="screw-hex-3x33"
  Placement = pos=(5,0,23) rot=(0,0,1;0rad)
  Refine = true
  Shapes = -> [Cylinder1041,Cylinder1040]
FEATURE [Part::Box] Box240  label="Cube242"
  AttacherType = Attacher::AttachEngine3D
  Height = 5
  Length = 10
  Placement = pos=(-146,-13,20.5) rot=(0,0,1;0rad)
  Width = 10
FEATURE [Part::MultiFuse] Fusion001005002004004005002010002003003003017007024041010023003003006006003006008021054006004013005009020003043002011002010006015002010005002  label="Fusion-0011"
  Refine = true
  Shapes = -> [Fusion001005002004004005002010002003003003017007024041010023003003006006003006008021044,Box240]
FEATURE [Part::Cut] Cut012035015003002009024006019011009006027002007011007005004011002017003  label="drawbar"
  Base = -> Fusion001005002004004005002010002003003003017007024041010023003003006006003006008021054006004013005009020003043002011002010006015002010005002
  Refine = true
  Tool = -> Fusion001005002004004005002010002003003003017007024041010023003003006006003006008021043
FEATURE [App::DocumentObjectGroup] Group001  label="Front Part"
  Group = -> [Cut012035015003002009008,Cut012035015003002009024002,Cut012035015003002009024003,Fusion001005002004004005002010002003003003017007024041010023003003006006003006008021006,Cut012035015003002009024006005,Part__Mirroring005002002002002002001,Cut012035013,Fusion001005002004004005002010002003003003001,Cut012035015003002009024006019011009006018,Cut012035015003002009024006019011009006019,+10 more]
FEATURE [Part::Box] Box241  label="Cube243"
  AttacherType = Attacher::AttachEngine3D
  Height = 6
  Length = 10.2
  Placement = pos=(-50.5,19.2,20.5) rot=(0,0,1;0rad)
  Width = 5.6
FEATURE [Part::Cylinder] Cylinder1042  label="Cylinder1112"
  Angle = 360
  AttacherType = Attacher::AttachEngine3D
  Height = 65
  Placement = pos=(-44.1,-26.5,23) rot=(-1,0,0;1.5708rad)
  Radius = 1.5
FEATURE [Part::Box] Box242  label="Cube244"
  AttacherType = Attacher::AttachEngine3D
  Height = 7
  Length = 12
  Placement = pos=(-50.5,17,18.5) rot=(0,0,1;0rad)
  Width = 10
FEATURE [Part::Cut] Cut012035015003002009024006019011009006027002007011007005004011002017004  label="Cut-0013"
  Base = -> Box242
  Refine = true
  Tool = -> Box241
FEATURE [Part::Cut] Cut012035015003002009024006019011009006027002007011007005004011002017005  label="drawbar-HOLES-TOOL-01"
  Base = -> Cut012035015003002009024006019011009006027002007011007005004011002017004
  Refine = true
  Tool = -> Cylinder1042
FEATURE [Part::Box] Box243  label="Cube245"
  AttacherType = Attacher::AttachEngine3D
  Height = 9
  Length = 12
  Placement = pos=(-163.5,-14,18.5) rot=(0,0,1;0rad)
  Width = 12
FEATURE [Part::Box] Box244  label="Cube246"
  AttacherType = Attacher::AttachEngine3D
  Height = 5.4
  Length = 9
  Placement = pos=(-160,-12.3,20.3) rot=(0,0,1;0rad)
  Width = 8.6
FEATURE [Part::Cut] Cut012035015003002009024006019011009006027002007011007005004011002017006  label="Cut-0015"
  Base = -> Box243
  Refine = true
  Tool = -> Box244
FEATURE [Part::Cylinder] Cylinder1043  label="Cylinder1113"
  Angle = 360
  AttacherType = Attacher::AttachEngine3D
  Height = 25
  Placement = pos=(-166,-8,23) rot=(0,1,0;1.5708rad)
  Radius = 1.5
FEATURE [Part::Cut] Cut012035015003002009024006019011009006027002007011007005004011002017007  label="drawbar-HOLES-TOOL-02"
  Base = -> Cut012035015003002009024006019011009006027002007011007005004011002017006
  Refine = true
  Tool = -> Cylinder1043
FEATURE [App::DocumentObjectGroup] Group004  label="Tools"
  Group = -> [Cut012035015003002009024006019003,Cut012035015003002009024006018,Cut012035015003002009024006021,Cut012035015003002009024006019011009006020,Cut012035015003002009024006019011009006027002007011007005004011002017005,Cut012035015003002009024006019011009006027002007011007005004011002017007]
FEATURE [Part::Cylinder] Cylinder1059  label="Cylinder1129"
  Angle = 360
  AttacherType = Attacher::AttachEngine3D
  Height = 2
  Placement = pos=(570.5,-101,4) rot=(-1,0,0;1.5708rad)
  Radius = 2
FEATURE [Part::MultiFuse] Fusion001005002004004005002010002003003003017007024041010023003003006006003006008021054006004013005009020003043002011002010  label="Fusion-321"
  Placement = pos=(0.2,0,0) rot=(0,0,1;0rad)
  Refine = true
  Shapes = -> [Fusion001005002004004005002010002003003003017007024041010023003003006006003006008021054006004013005009020003043002011002007,Fusion001005002004004005002010002003003003017007024041010023003003006006003006008021054006004013005009020003043002011002009,Fusion001005002004004005002010002003003003017007024041010023003003006006003006008021054006004013005009020003043002011002008,Cylinder1059]
FEATURE [Part::Cut] Cut012035015003002009024006019011009006027002007011007005004011002017013  label="Cut-0021"
  Base = -> Cut012035015003002009024006019011009006027002007011007004
  Refine = true
  Tool = -> Fusion001005002004004005002010002003003003017007024041010023003003006006003006008021054006004013005009020003043002011002010
FEATURE [Part::Fillet] Fillet001025008003
  Base = -> Cut012035015003002009024006019011009006027002007011007005004011002017013
  Edges = 1 edges r=4: [Edge30]
FEATURE [Part::Fillet] Fillet001025008004  label="ramp-left-ext-side"
  Base = -> Fillet001025008003
  Edges = 1 edges r=6: [Edge37]
  Placement = pos=(-0.04,0,0) rot=(0,0,1;0rad)
FEATURE [Part::Feature] Part__Mirroring005002002002002002002002002022004003003002002004003002001  label="ramp-left-int-side"
  Placement = pos=(0,-144,0) rot=(0,0,1;0rad)
  shape: bbox 152.6 x 4.2 x 60.33 mm, 23 faces (baked)
FEATURE [Part::Cone] Cone026
  Angle = 360
  AttacherType = Attacher::AttachEngine3D
  Height = 1
  Placement = pos=(569.5,-48.2,0.5) rot=(1,0,0;1.5708rad)
  Radius1 = 2
  Radius2 = 1
FEATURE [Part::Cylinder] Cylinder1061  label="Cylinder1131"
  Angle = 360
  AttacherType = Attacher::AttachEngine3D
  Height = 1.4
  Placement = pos=(569.5,-48.2,0.5) rot=(1,0,0;1.5708rad)
  Radius = 1
FEATURE [Part::Cylinder] Cylinder1062  label="Cylinder1132"
  Angle = 360
  AttacherType = Attacher::AttachEngine3D
  Height = 6
  Placement = pos=(569.5,-48.2,0.5) rot=(1,0,0;1.5708rad)
  Radius = 0.8
FEATURE [Part::MultiFuse] Fusion001005002004004005002010002003003003017007024041010023003003006006003006008021054006004013005009020003043002011002010006015002010005005003002  label="Fusion-0020"
  Placement = pos=(1.1,3,3.5) rot=(0,0,1;0rad)
  Refine = true
  Shapes = -> [Cylinder1062,Cylinder1061,Cone026]
FEATURE [Part::Feature] Part__Mirroring005002002002002002002002002022004003003002002004003002002  label="motor_12V_20RPM007"
  Placement = pos=(567.857,-95.2,7.03675) rot=(0,1,0;0.314159rad)
  shape: bbox 39.16 x 12.4 x 19.16 mm, 20 faces (baked)
FEATURE [Part::Cone] Cone027
  Angle = 360
  AttacherType = Attacher::AttachEngine3D
  Height = 1.5
  Placement = pos=(561.2,-57.7,9.2) rot=(1,0,0;1.5708rad)
  Radius1 = 3.3
  Radius2 = 6.25
FEATURE [Part::Cylinder] Cylinder1065  label="Cylinder1135"
  Angle = 360
  AttacherType = Attacher::AttachEngine3D
  Height = 5.3
  Placement = pos=(561.2,-63,9.2) rot=(-1,0,0;1.5708rad)
  Radius = 3
FEATURE [Part::Cylinder] Cylinder1066  label="Cylinder1136"
  Angle = 360
  AttacherType = Attacher::AttachEngine3D
  Height = 1.5
  Placement = pos=(561.2,-60.7,9.2) rot=(-1,0,0;1.5708rad)
  Radius = 6.25
FEATURE [Part::Cone] Cone028
  Angle = 360
  AttacherType = Attacher::AttachEngine3D
  Height = 2.3
  Placement = pos=(561.2,-60.7,9.2) rot=(1,0,0;1.5708rad)
  Radius1 = 6.25
  Radius2 = 2.5
FEATURE [Part::Cylinder] Cylinder1064  label="Cylinder1134"
  Angle = 360
  AttacherType = Attacher::AttachEngine3D
  Height = 5
  Placement = pos=(564.2,-55.75,9.2) rot=(0,1,0;1.5708rad)
  Radius = 5.5
FEATURE [Part::Cylinder] Cylinder1067  label="Cylinder1137"
  Angle = 360
  AttacherType = Attacher::AttachEngine3D
  Height = 10
  Placement = pos=(564.2,-55.75,9.2) rot=(0,1,0;1.5708rad)
  Radius = 3.1
FEATURE [Part::MultiFuse] Fusion001005002004004005002010002003003003017007024041010023003003006006003006008021054006004013005009020003043002011002010006015002010005005003002003  label="Fusion-0022"
  Refine = true
  Shapes = -> [Cone027,Cylinder1066,Cylinder1065,Cone028]
FEATURE [Part::MultiFuse] Fusion001005002004004005002010002003003003017007024041010023003003006006003006008021054006004013005009020003043002011002010006015002010005005003002003003  label="Fusion-0025"
  Refine = true
  Shapes = -> [Cylinder1067,Cylinder1064]
FEATURE [Part::Feature] Part__Mirroring005002002002002002002002002022004003003002002004003002003002  label="motor_12V_20RPM008"
  Placement = pos=(569.2,-63,9.19986) rot=(0,0,1;0rad)
  shape: bbox 39 x 12.4 x 10.4 mm, 20 faces (baked)
FEATURE [Part::Cylinder] Cylinder1068  label="Cylinder1138"
  Angle = 360
  AttacherType = Attacher::AttachEngine3D
  Height = 59
  Placement = pos=(658.5,-101,4.5) rot=(-1,0,0;1.5708rad)
  Radius = 1.5
FEATURE [Part::Box] Box252  label="Cube254"
  AttacherType = Attacher::AttachEngine3D
  Height = 8.3
  Length = 7
  Placement = pos=(655,-81,1.2) rot=(0,1,0;0rad)
  Width = 5.8
FEATURE [Part::Box] Box253  label="Cube255"
  AttacherType = Attacher::AttachEngine3D
  Height = 8.3
  Length = 7
  Placement = pos=(655,-68.8,1.2) rot=(0,1,0;0rad)
  Width = 5.8
FEATURE [Part::MultiFuse] Fusion001005002004004005002010002003003003017007024041010023003003006006003006008021054006004013005009020003043002011002010006015002010005005003002003005  label="Fusion-0026"
  Refine = true
  Shapes = -> [Box252,Box253]
FEATURE [Part::MultiFuse] Fusion001005002004004005002010002003003003017007024041010023003003006006003006008021054006004013005009020003043002011002010006015002010005005003002003007  label="ramp-motor-carving"
  Placement = pos=(-1,-0.25,0) rot=(0,0,1;0rad)
  Refine = true
  Shapes = -> [Fusion001005002004004005002010002003003003017007024041010023003003006006003006008021054006004013005009020003043002011002010006015002010005005003002003003,Part__Mirroring005002002002002002002002002022004003003002002004003002003002]
FEATURE [Part::Feature] ramp_left_ext_side001001  label="ramp_left_ext_side002"
  Placement = pos=(30.31,0,-172.97) rot=(0,-1,0;0.314159rad)
  shape: bbox 139.2 x 4.2 x 14 mm, 1642 faces, 0 solids (baked)
FEATURE [App::DocumentObjectGroup] Group006  label="Old Parts"
  Group = -> [ramp_left_ext_side001001,Fusion001005002004004005002010002003003003017007024041010023003003006006003006008021054006004013005009020003043002011002,Part__Mirroring005002002002002002002002002017,Cut012035015003002009024006019011009002,Cut012035015003002009024006019011009003,Chamfer007038020005]
FEATURE [Part::Box] Box256  label="Cube258"
  AttacherType = Attacher::AttachEngine3D
  Height = 15
  Length = 1
  Placement = pos=(554,-101,2.5) rot=(0,0,1;0rad)
  Width = 5
FEATURE [Part::Feature] Face019
  shape: bbox 74.7 x 2e-07 x 37.45 mm, 1 faces, 0 solids (baked)
FEATURE [Part::Feature] Face020
  shape: bbox 76.16 x 2e-07 x 40.23 mm, 1 faces, 0 solids (baked)
FEATURE [Part::Extrusion] Extrude021
  Base = -> Face019
  Dir = (0,1,0)
  DirMode = 0
  FaceMakerClass = Part::FaceMakerBullseye
  LengthFwd = 1
  LengthRev = 0
  Solid = true
  Symmetric = false
FEATURE [Part::Extrusion] Extrude022
  Base = -> Face020
  Dir = (0,1,0)
  DirMode = 0
  FaceMakerClass = Part::FaceMakerBullseye
  LengthFwd = 5
  LengthRev = 0
  Solid = true
  Symmetric = false
FEATURE [Part::Cut] Cut012035015003002009024006019011009006027002007011007005004011002017019010006
  Base = -> Extrude021
  Refine = true
  Tool = -> Box256
FEATURE [Part::Cone] Cone029
  Angle = 360
  AttacherType = Attacher::AttachEngine3D
  Height = 1
  Placement = pos=(0,0,0) rot=(-1,0,0;1.5708rad)
  Radius1 = 2
  Radius2 = 1.2
FEATURE [Part::Cylinder] Cylinder1072  label="Cylinder1142"
  Angle = 360
  AttacherType = Attacher::AttachEngine3D
  Height = 4
  Placement = pos=(0,0,0) rot=(-1,0,0;1.5708rad)
  Radius = 1.2
FEATURE [Part::Cylinder] Cylinder1073  label="Cylinder1143"
  Angle = 360
  AttacherType = Attacher::AttachEngine3D
  Height = 17
  Placement = pos=(0,0,0) rot=(-1,0,0;1.5708rad)
  Radius = 0.8
FEATURE [Part::MultiFuse] Fusion001005002004004005002010002003003003017007024041010023003003006006003006008021054006004013005009020003043002011002010006015002010005005003002003010  label="Fusion-0030"
  Placement = pos=(551,-100,15) rot=(0,0,1;0rad)
  Refine = true
  Shapes = -> [Cone029,Cylinder1072,Cylinder1073]
FEATURE [Part::Feature] Fusion001005002004004005002010002003003003017007024041010023003003006006003006008021054006004013005009020003043002011002010006015002010005005003002003011  label="Fusion-0031"
  Placement = pos=(551,-100,7.5) rot=(0,0,1;0rad)
  shape: bbox 4 x 17 x 4 mm, 6 faces (baked)
FEATURE [Part::Feature] Fusion001005002004004005002010002003003003017007024041010023003003006006003006008021054006004013005009020003043002011002010006015002010005005003002003012  label="Fusion-0032"
  Placement = pos=(531,-100,19) rot=(0,0,1;0rad)
  shape: bbox 4 x 17 x 4 mm, 6 faces (baked)
FEATURE [Part::Feature] Fusion001005002004004005002010002003003003017007024041010023003003006006003006008021054006004013005009020003043002011002010006015002010005005003002003013  label="Fusion-0033"
  Placement = pos=(499,-100,29.5) rot=(0,0,1;0rad)
  shape: bbox 4 x 17 x 4 mm, 6 faces (baked)
FEATURE [Part::Feature] Fusion001005002004004005002010002003003003017007024041010023003003006006003006008021054006004013005009020003043002011002010006015002010005005003002003014  label="Fusion-0034"
  Placement = pos=(505,-100,27.4) rot=(0,0,1;0rad)
  shape: bbox 4 x 17 x 4 mm, 6 faces (baked)
FEATURE [Part::MultiFuse] Fusion001005002004004005002010002003003003017007024041010023003003006006003006008021054006004013005009020003043002011002010006015002010005005003002003015  label="Fusion-0035"
  Refine = true
  Shapes = -> [Fusion001005002004004005002010002003003003017007024041010023003003006006003006008021054006004013005009020003043002011002010006015002010005005003002003011,Fusion001005002004004005002010002003003003017007024041010023003003006006003006008021054006004013005009020003043002011002010006015002010005005003002003013,+3 more]
FEATURE [Part::Box] Box257  label="Cube259"
  AttacherType = Attacher::AttachEngine3D
  Height = 19
  Length = 11
  Placement = pos=(547,-101,2) rot=(0,0,1;0rad)
  Width = 5
FEATURE [Part::Feature] Face021
  shape: bbox 76.16 x 2e-07 x 40.23 mm, 1 faces, 0 solids (baked)
FEATURE [Part::Extrusion] Extrude023
  Base = -> Face021
  Dir = (0,1,0)
  DirMode = 0
  FaceMakerClass = Part::FaceMakerBullseye
  LengthFwd = 5
  LengthRev = 0
  Solid = true
  Symmetric = false
FEATURE [Part::Box] Box258  label="Cube260"
  AttacherType = Attacher::AttachEngine3D
  Height = 36
  Length = 53
  Placement = pos=(494,-101,2) rot=(0,0,1;0rad)
  Width = 5
FEATURE [Part::Cut] Cut012035015003002009024006019011009006027002007011007005004011002017019010008  label="Cut-0040"
  Base = -> Extrude022
  Refine = true
  Tool = -> Box257
FEATURE [Part::Chamfer] Chamfer007038020005004
  Base = -> Cut012035015003002009024006019011009006027002007011007005004011002017019010008
  Edges = 1 edges r=0.6: [Edge10]
FEATURE [Part::Cut] Cut012035015003002009024006019011009006027002007011007005004011002017019010009  label="Cut-0041"
  Base = -> Extrude023
  Refine = true
  Tool = -> Box258
FEATURE [Part::MultiFuse] Fusion001005002004004005002010002003003003017007024041010023003003006006003006008021054006004013005009020003043002011002010006015002010005005003002003016  label="Fusion-0036"
  Refine = true
  Shapes = -> [Chamfer007038020005004,Cut012035015003002009024006019011009006027002007011007005004011002017019010009]
FEATURE [Part::Cut] Cut012035015003002009024006019011009006027002007011007005004011002017019010010  label="Cut-0042"
  Base = -> Fusion001005002004004005002010002003003003017007024041010023003003006006003006008021054006004013005009020003043002011002010006015002010005005003002003016
  Refine = true
  Tool = -> Cut012035015003002009024006019011009006027002007011007005004011002017019010006
FEATURE [Part::Box] Box259  label="Cube261"
  AttacherType = Attacher::AttachEngine3D
  Height = 15
  Length = 333
  Placement = pos=(65,-101,22) rot=(0,0,1;0rad)
  Width = 5
FEATURE [Part::Cylinder] Cylinder1074  label="Cylinder1144"
  Angle = 360
  AttacherType = Attacher::AttachEngine3D
  Height = 5
  Placement = pos=(547,-99,14) rot=(-1,0,0;1.5708rad)
  Radius = 2.8
FEATURE [Part::Feature] Chamfer007038020005005
  shape: bbox 430 x 5 x 15 mm, 56 faces (baked)
FEATURE [Part::Cut] Cut012035015003002009024006019011009006027002007011007005004011002017019010012  label="Cut-0044"
  Base = -> Chamfer007038020005005
  Refine = true
  Tool = -> Box259
FEATURE [Part::Box] Box260  label="Cube262"
  AttacherType = Attacher::AttachEngine3D
  Height = 10
  Length = 50
  Placement = pos=(445,-33,25) rot=(0,0,1;0rad)
  Width = 25
FEATURE [Part::Box] Box261  label="Cube263"
  AttacherType = Attacher::AttachEngine3D
  Height = 17.6
  Length = 8
  Placement = pos=(547,-96,2.5) rot=(0,0,1;0rad)
  Width = 88
FEATURE [Part::Cylinder] Cylinder1077  label="Cylinder1147"
  Angle = 360
  AttacherType = Attacher::AttachEngine3D
  Height = 59
  Placement = pos=(561.2,-101,9.2) rot=(-1,0,0;1.5708rad)
  Radius = 1.5
FEATURE [Part::Chamfer] Chamfer007038020005008
  Base = -> Box261
  Edges = 1 edges: [Edge6 r1=2.6 r2=7.999]
FEATURE [Part::Chamfer] Chamfer007038020005009
  Base = -> Chamfer007038020005008
  Edges = 1 edges: [Edge11 r1=7.999 r2=2.6]
FEATURE [Part::Box] Box262  label="Cube264"
  AttacherType = Attacher::AttachEngine3D
  Height = 10
  Length = 11
  Placement = pos=(484,-76,25) rot=(0,0,1;0rad)
  Width = 10
FEATURE [Part::Box] Box263  label="Cube265"
  AttacherType = Attacher::AttachEngine3D
  Height = 15
  Length = 11
  Placement = pos=(555,-48,2.5) rot=(0,0,1;0rad)
  Width = 4
FEATURE [Part::Chamfer] Chamfer007038020005006
  Base = -> Box263
  Edges = 1 edges: [Edge6 r1=3.6 r2=10.999]
FEATURE [Part::Chamfer] Chamfer007038020005007
  Base = -> Chamfer007038020005006
  Edges = 1 edges: [Edge3 r1=1.1 r2=10.999]
FEATURE [Part::Fillet] Fillet001025008004002
  Base = -> Chamfer007038020005007
  Edges = 2 edges r=4: [Edge2,Edge3]
FEATURE [Part::Cylinder] Cylinder1081  label="Cylinder1151"
  Angle = 360
  AttacherType = Attacher::AttachEngine3D
  Height = 30
  Placement = pos=(478,-45,30) rot=(-1,0,0;1.5708rad)
  Radius = 1.25
FEATURE [Part::Cylinder] Cylinder1082  label="Cylinder1152"
  Angle = 360
  AttacherType = Attacher::AttachEngine3D
  Height = 30
  Placement = pos=(464,-45,30) rot=(-1,0,0;1.5708rad)
  Radius = 1.25
FEATURE [Part::Cylinder] Cylinder1083  label="Cylinder1153"
  Angle = 360
  AttacherType = Attacher::AttachEngine3D
  Height = 30
  Placement = pos=(450,-45,30) rot=(-1,0,0;1.5708rad)
  Radius = 1.25
FEATURE [Part::Feature] Fusion001005002004004005002010002003003003017007024041010023003003006006003006008021054006004013005009020003043002011002010006015002010005005003002003025  label="Fusion-0043"
  shape: bbox 56 x 17 x 26 mm, 30 faces, 5 solids (baked)
FEATURE [Part::Cylinder] Cylinder1084  label="Cylinder1154"
  Angle = 360
  AttacherType = Attacher::AttachEngine3D
  Height = 184
  Placement = pos=(490,-100,30) rot=(-1,0,0;1.5708rad)
  Radius = 2.7
FEATURE [Part::Cylinder] Cylinder1085  label="Cylinder1155"
  Angle = 360
  AttacherType = Attacher::AttachEngine3D
  Height = 182
  Placement = pos=(547,-99,14) rot=(-1,0,0;1.5708rad)
  Radius = 2.7
FEATURE [Part::MultiFuse] Fusion001005002004004005002010002003003003017007024041010023003003006006003006008021054006004013005009020003043002011002010006015002010005005003002003026  label="Fusion0003"
  Refine = true
  Shapes = -> [Cylinder1084,Cylinder1083,Cylinder1085,Cylinder1082,Cylinder1081,Fusion001005002004004005002010002003003003017007024041010023003003006006003006008021054006004013005009020003043002011002010006015002010005005003002003025]
FEATURE [Part::Cut] Cut012035015003002009024006019011009006027002007011007005004011002017019010014  label="Cut-0046"
  Base = -> Fillet001025008004002
  Refine = true
  Tool = -> Cylinder1077
FEATURE [Part::Box] Box264  label="Cube266"
  AttacherType = Attacher::AttachEngine3D
  Height = 42.5
  Length = 11
  Placement = pos=(502,-89,31) rot=(0,1,0;1.88496rad)
  Width = 72
FEATURE [Part::Feature] Face022
  shape: bbox 74.39 x 2e-07 x 37.47 mm, 1 faces, 0 solids (baked)
FEATURE [Part::Extrusion] Extrude024
  Base = -> Face022
  Dir = (0,1,0)
  DirMode = 0
  FaceMakerClass = Part::FaceMakerBullseye
  LengthFwd = 88
  LengthRev = 0
  Solid = true
  Symmetric = false
FEATURE [Part::Feature] Face023
  shape: bbox 31.48 x 2e-07 x 30.83 mm, 1 faces, 0 solids (baked)
FEATURE [Part::Extrusion] Extrude025
  Base = -> Face023
  Dir = (0,1,0)
  DirMode = 0
  FaceMakerClass = Part::FaceMakerBullseye
  LengthFwd = 16
  LengthRev = 0
  Solid = true
  Symmetric = false
FEATURE [Part::Fillet] Fillet001025008004003
  Base = -> Extrude025
  Edges = 2 edges r=12: [Edge8,Edge17]
FEATURE [Part::Box] Box265  label="Cube267"
  AttacherType = Attacher::AttachEngine3D
  Height = 19
  Length = 14
  Placement = pos=(562.173,-77.3,-13) rot=(0,0,1;0rad)
  Width = 10.6
FEATURE [Part::Cut] Cut012035015003002009024006019011009006027002007011007005004011002017019010017
  Base = -> Fillet001025008004003
  Refine = true
  Tool = -> Box265
FEATURE [Part::Cylinder] Cylinder1086  label="Cylinder1156"
  Angle = 360
  AttacherType = Attacher::AttachEngine3D
  Height = 59
  Placement = pos=(568,-101,-7) rot=(-1,0,0;1.5708rad)
  Radius = 1.5
FEATURE [Part::Cut] Cut012035015003002009024006019011009006027002007011007005004011002017019010018  label="Cut-0045"
  Base = -> Cut012035015003002009024006019011009006027002007011007005004011002017019010017
  Refine = true
  Tool = -> Cylinder1086
FEATURE [Part::Cylinder] Cylinder1087  label="Cylinder1157"
  Angle = 360
  AttacherType = Attacher::AttachEngine3D
  Height = 10
  Placement = pos=(551,-38,2.5) rot=(0,0,1;0rad)
  Radius = 1.25
FEATURE [Part::Box] Box266  label="Cube268"
  AttacherType = Attacher::AttachEngine3D
  Height = 5
  Length = 8
  Placement = pos=(547,-44,2.5) rot=(0,0,1;0rad)
  Width = 36
FEATURE [Part::Cylinder] Cylinder1088  label="Cylinder1158"
  Angle = 360
  AttacherType = Attacher::AttachEngine3D
  Height = 10
  Placement = pos=(542,-59,2.5) rot=(0,1,0;0.296706rad)
  Radius = 0.9
FEATURE [Part::Cylinder] Cylinder1089  label="Cylinder1159"
  Angle = 360
  AttacherType = Attacher::AttachEngine3D
  Height = 10
  Placement = pos=(542,-48,2.5) rot=(0,1,0;0.296706rad)
  Radius = 0.9
FEATURE [Part::Cylinder] Cylinder1090  label="Cylinder1160"
  Angle = 360
  AttacherType = Attacher::AttachEngine3D
  Height = 10
  Placement = pos=(483,-20,24.5) rot=(0,1,0;0rad)
  Radius = 0.9
FEATURE [Part::Cylinder] Cylinder1091  label="Cylinder1161"
  Angle = 360
  AttacherType = Attacher::AttachEngine3D
  Height = 10
  Placement = pos=(451,-20,24.5) rot=(0,1,0;0rad)
  Radius = 0.9
FEATURE [Part::MultiFuse] Fusion001005002004004005002010002003003003017007024041010023003003006006003006008021054006004013005009020003043002011002010006015002010005005003002003028  label="Fusion-0045"
  Refine = true
  Shapes = -> [Cylinder1087,Cylinder1088,Cylinder1089,Cylinder1090,Cylinder1091]
FEATURE [Part::Cylinder] Cylinder1092  label="Cylinder1162"
  Angle = 360
  AttacherType = Attacher::AttachEngine3D
  Height = 10
  Placement = pos=(541,-92,11) rot=(0,1,0;0.296706rad)
  Radius = 0.9
FEATURE [Part::Cylinder] Cylinder1093  label="Cylinder1163"
  Angle = 360
  AttacherType = Attacher::AttachEngine3D
  Height = 10
  Placement = pos=(541,-22,11) rot=(0,1,0;0.296706rad)
  Radius = 0.9
FEATURE [Part::Cylinder] Cylinder1094  label="Cylinder1164"
  Angle = 360
  AttacherType = Attacher::AttachEngine3D
  Height = 10
  Placement = pos=(496,-22,25.5) rot=(0,1,0;0.296706rad)
  Radius = 0.9
FEATURE [Part::Cylinder] Cylinder1095  label="Cylinder1165"
  Angle = 360
  AttacherType = Attacher::AttachEngine3D
  Height = 10
  Placement = pos=(496,-92,25.5) rot=(0,1,0;0.296706rad)
  Radius = 0.9
FEATURE [Part::MultiFuse] Fusion001005002004004005002010002003003003017007024041010023003003006006003006008021054006004013005009020003043002011002010006015002010005005003002003029  label="Fusion-0046"
  Refine = true
  Shapes = -> [Cylinder1092,Cylinder1095,Cylinder1094,Cylinder1093]
FEATURE [Part::MultiFuse] Fusion001005002004004005002010002003003003017007024041010023003003006006003006008021054006004013005009020003043002011002010006015002010005005003002003030  label="Fusion-0047"
  Refine = true
  Shapes = -> [Fusion001005002004004005002010002003003003017007024041010023003003006006003006008021054006004013005009020003043002011002010006015002010005005003002003028,Fusion001005002004004005002010002003003003017007024041010023003003006006003006008021054006004013005009020003043002011002010006015002010005005003002003029]
FEATURE [Part::Box] Box267  label="Cube269"
  AttacherType = Attacher::AttachEngine3D
  Height = 1
  Length = 55
  Placement = pos=(495,-96,36) rot=(0,1,0;0.314159rad)
  Width = 176
FEATURE [Part::Cylinder] Cylinder1096  label="Cylinder1166"
  Angle = 360
  AttacherType = Attacher::AttachEngine3D
  Height = 59
  Placement = pos=(561.2,-101,9.2) rot=(-1,0,0;1.5708rad)
  Radius = 1.5
FEATURE [Part::Box] Box268  label="Cube270"
  AttacherType = Attacher::AttachEngine3D
  Height = 15
  Length = 11
  Placement = pos=(555,-48,2.5) rot=(0,0,1;0rad)
  Width = 4
FEATURE [Part::Chamfer] Chamfer007038020005011
  Base = -> Box268
  Edges = 1 edges: [Edge6 r1=3.6 r2=10.999]
FEATURE [Part::Chamfer] Chamfer007038020005010
  Base = -> Chamfer007038020005011
  Edges = 1 edges: [Edge3 r1=1.1 r2=10.999]
FEATURE [Part::Fillet] Fillet001025008004004
  Base = -> Chamfer007038020005010
  Edges = 2 edges r=4: [Edge2,Edge3]
FEATURE [Part::Cut] Cut012035015003002009024006019011009006027002007011007005004011002017019010019  label="Cut-0047"
  Base = -> Fillet001025008004004
  Placement = pos=(0,-52,0) rot=(0,0,1;0rad)
  Refine = true
  Tool = -> Cylinder1096
FEATURE [Part::MultiFuse] Fusion001005002004004005002010002003003003017007024041010023003003006006003006008021054006004013005009020003043002011002010006015002010005005003002003031  label="Fusion-0048"
  Refine = true
  Shapes = -> [Box260,Extrude024,Cut012035015003002009024006019011009006027002007011007005004011002017019010014,Chamfer007038020005009,Box262]
FEATURE [Part::MultiFuse] Fusion001005002004004005002010002003003003017007024041010023003003006006003006008021054006004013005009020003043002011002010006015002010005005003002003032  label="Fusion-0049"
  Refine = true
  Shapes = -> [Cut012035015003002009024006019011009006027002007011007005004011002017019010010,Cut012035015003002009024006019011009006027002007011007005004011002017019010019]
FEATURE [Part::Cut] Cut012035015003002009024006019011009006027002007011007005004011002017019010020  label="Cut-0048"
  Base = -> Fusion001005002004004005002010002003003003017007024041010023003003006006003006008021054006004013005009020003043002011002010006015002010005005003002003032
  Refine = true
  Tool = -> Fusion001005002004004005002010002003003003017007024041010023003003006006003006008021054006004013005009020003043002011002010006015002010005005003002003015
FEATURE [Part::Cut] Cut012035015003002009024006019011009006027002007011007005004011002017019010021  label="Cut-0049"
  Base = -> Cut012035015003002009024006019011009006027002007011007005004011002017019010020
  Refine = true
  Tool = -> Cylinder1074
FEATURE [Part::MultiFuse] Fusion001005002004004005002010002003003003017007024041010023003003006006003006008021054006004013005009020003043002011002010006015002010005005003002003033  label="border-lateral-3-left"
  Refine = true
  Shapes = -> [Cut012035015003002009024006019011009006027002007011007005004011002017019010012,Cut012035015003002009024006019011009006027002007011007005004011002017019010021]
FEATURE [Part::Feature] Part__Mirroring005002002002002002002002002022004003003002002004003002003003002001  label="border-lateral-3-right"
  Placement = pos=(0,-16,0) rot=(0,0,1;0rad)
  shape: bbox 168 x 5 x 40.23 mm, 57 faces (baked)
FEATURE [Part::Box] Box269  label="Cube271"
  AttacherType = Attacher::AttachEngine3D
  Height = 6.5
  Length = 1.7
  Placement = pos=(560.35,-45.7,6) rot=(0,0,1;0rad)
  Width = 1.7
FEATURE [Part::Fillet] Fillet001025008004005
  Base = -> Box269
  Edges = 2 edges r=0.5: [Edge1,Edge5]
FEATURE [Part::Cut] Cut012035015003002009024006019011009006027002007011007005004011002017019010022  label="Cut-0050"
  Base = -> Fusion001005002004004005002010002003003003017007024041010023003003006006003006008021054006004013005009020003043002011002010006015002010005005003002003031
  Refine = true
  Tool = -> Fillet001025008004005
FEATURE [Part::Cut] Cut012035015003002009024006019011009006027002007011007005004011002017019010023  label="Cut-0051"
  Base = -> Cut012035015003002009024006019011009006027002007011007005004011002017019010022
  Refine = true
  Tool = -> Box264
FEATURE [Part::MultiFuse] Fusion001005002004004005002010002003003003017007024041010023003003006006003006008021054006004013005009020003043002011002010006015002010005005003002003034  label="Fusion-0050"
  Refine = true
  Shapes = -> [Cut012035015003002009024006019011009006027002007011007005004011002017019010023,Box266]
FEATURE [Part::MultiFuse] Fusion001005002004004005002010002003003003017007024041010023003003006006003006008021054006004013005009020003043002011002010006015002010005005003002003035  label="Fusion-0051"
  Refine = true
  Shapes = -> [Fusion001005002004004005002010002003003003017007024041010023003003006006003006008021054006004013005009020003043002011002010006015002010005005003002003034,Cut012035015003002009024006019011009006027002007011007005004011002017019010018]
FEATURE [Part::Cut] Cut012035015003002009024006019011009006027002007011007005004011002017019010024  label="Cut-0052"
  Base = -> Fusion001005002004004005002010002003003003017007024041010023003003006006003006008021054006004013005009020003043002011002010006015002010005005003002003035
  Refine = true
  Tool = -> Box267
FEATURE [Part::Fillet] Fillet001025008004006
  Base = -> Chamfer007038020009
  Edges = 1 edges r=3: [Edge9]
FEATURE [Part::Cylinder] Cylinder1097  label="Cylinder1167"
  Angle = 360
  AttacherType = Attacher::AttachEngine3D
  Height = 16
  Placement = pos=(547,-80,6) rot=(-1,0,0;1.5708rad)
  Radius = 1.6
FEATURE [Part::Box] Box270  label="Cube272"
  AttacherType = Attacher::AttachEngine3D
  Height = 8
  Length = 14
  Placement = pos=(540,-80,2) rot=(0,0,1;0rad)
  Width = 2.5
FEATURE [Part::Fillet] Fillet001025008004007
  Base = -> Box270
  Edges = 1 edges r=5: [Edge4]
FEATURE [Part::Box] Box271  label="Cube273"
  AttacherType = Attacher::AttachEngine3D
  Height = 8
  Length = 14
  Placement = pos=(540,-80,2) rot=(0,0,1;0rad)
  Width = 2.5
FEATURE [Part::Fillet] Fillet001025008004008
  Base = -> Box271
  Edges = 1 edges r=5: [Edge4]
  Placement = pos=(0,13.5,0) rot=(0,0,1;0rad)
FEATURE [Part::Box] Box272  label="Cube274"
  AttacherType = Attacher::AttachEngine3D
  Height = 4
  Length = 3
  Placement = pos=(545.5,-80,2) rot=(0,0,1;0rad)
  Width = 2.5
FEATURE [Part::Chamfer] Chamfer007038020005012
  Base = -> Box272
  Edges = 2 edges: [Edge2 r1=3 r2=0.25,Edge6 r1=3 r2=0.25]
FEATURE [Part::Box] Box273  label="Cube275"
  AttacherType = Attacher::AttachEngine3D
  Height = 4
  Length = 3
  Placement = pos=(545.5,-80,2) rot=(0,0,1;0rad)
  Width = 2.5
FEATURE [Part::Chamfer] Chamfer007038020005013
  Base = -> Box273
  Edges = 2 edges: [Edge2 r1=3 r2=0.25,Edge6 r1=3 r2=0.25]
  Placement = pos=(0,13.5,0) rot=(0,0,1;0rad)
FEATURE [Part::MultiFuse] Fusion001005002004004005002010002003003003017007024041010023003003006006003006008021054006004013005009020003043002011002010006015002010005005003002003036  label="Fusion-0052"
  Refine = true
  Shapes = -> [Chamfer007038020005013,Chamfer007038020005012,Cylinder1097]
FEATURE [Part::MultiFuse] Fusion001005002004004005002010002003003003017007024041010023003003006006003006008021054006004013005009020003043002011002010006015002010005005003002003037  label="Fusion-0053"
  Refine = true
  Shapes = -> [Fillet001025008004007,Fillet001025008004008]
FEATURE [Part::MultiFuse] Fusion001005002004004005002010002003003003017007024041010023003003006006003006008021054006004013005009020003043002011002010006015002010005005003002003038  label="Fusion-0054"
  Refine = true
  Shapes = -> [Fusion001005002004004005002010002003003003017007024041010023003003006006003006008021054006004013005009020003043002011002010006015002010005005003002003037,Cut012035015003002009024006019011009006027002007011007005004011002017019010024]
FEATURE [Part::Chamfer] Chamfer007038020005014
  Base = -> Fusion001005002004004005002010002003003003017007024041010023003003006006003006008021054006004013005009020003043002011002010006015002010005005003002003038
  Edges = 1 edges: [Edge82 r1=9.2 r2=15]
FEATURE [Part::Cut] Cut012035015003002009024006019011009006027002007011007005004011002017019010025  label="Cut-0053"
  Base = -> Chamfer007038020005014
  Refine = true
  Tool = -> Fillet001025008004006
FEATURE [Part::Cut] Cut012035015003002009024006019011009006027002007011007005004011002017019010026  label="Cut-0054"
  Base = -> Cut012035015003002009024006019011009006027002007011007005004011002017019010025
  Refine = true
  Tool = -> Fusion001005002004004005002010002003003003017007024041010023003003006006003006008021054006004013005009020003043002011002010006015002010005005003002003036
FEATURE [Part::Cut] Cut012035015003002009024006019011009006027002007011007005004011002017019010027  label="Cut-0055"
  Base = -> Cut012035015003002009024006019011009006027002007011007005004011002017019010026
  Refine = true
  Tool = -> Fusion001005002004004005002010002003003003017007024041010023003003006006003006008021054006004013005009020003043002011002010006015002010005005003002003026
FEATURE [Part::Cylinder] Cylinder1098  label="Cylinder1168"
  Angle = 360
  AttacherType = Attacher::AttachEngine3D
  Height = 10
  Placement = pos=(540,-22,9) rot=(0,1,0;0.296706rad)
  Radius = 2
FEATURE [Part::MultiFuse] Fusion001005002004004005002010002003003003017007024041010023003003006006003006008021054006004013005009020003043002011002010006015002010005005003002003039  label="Fusion-0055"
  Refine = true
  Shapes = -> [Cut012035015003002009024006019011009006027002007011007005004011002017019010027,Cylinder1098]
FEATURE [Part::Box] Box632  label="Cube823"
  AttacherType = Attacher::AttachEngine3D
  Height = 20.5
  Length = 23.5
  Width = 12
FEATURE [Part::Box] Box634  label="Cube825"
  AttacherType = Attacher::AttachEngine3D
  Height = 1.5
  Length = 32
  Placement = pos=(-4.25,0,15) rot=(0,0,1;0rad)
  Width = 12
FEATURE [Part::Cylinder] Cylinder958  label="Cylinder1473"
  Angle = 360
  AttacherType = Attacher::AttachEngine3D
  Height = 5.5
  Placement = pos=(6,6,24) rot=(0,0,1;0rad)
  Radius = 3
FEATURE [Part::Box] Box635  label="Cube826"
  AttacherType = Attacher::AttachEngine3D
  Height = 1.5
  Length = 17
  Placement = pos=(-9,3,34.5) rot=(0,0,1;0rad)
  Width = 6
FEATURE [Part::Fillet] Fillet425
  Base = -> Box635
  Edges = 4 edges r=2: [Edge1,Edge3,Edge5,Edge7]
  Placement = pos=(0,12,-6.5) rot=(0,0,-1;1.5708rad)
FEATURE [Part::Cylinder] Cylinder960  label="Cylinder1475"
  Angle = 360
  AttacherType = Attacher::AttachEngine3D
  Height = 10
  Radius = 1
FEATURE [Part::Cylinder] Cylinder961  label="Cylinder1476"
  Angle = 360
  AttacherType = Attacher::AttachEngine3D
  Height = 10
  Placement = pos=(-2,6.5,29) rot=(0,0,1;0rad)
  Radius = 0.5
FEATURE [Part::Cylinder] Cylinder1100  label="Cylinder1478"
  Angle = 360
  AttacherType = Attacher::AttachEngine3D
  Height = 10
  Placement = pos=(-4.5,6.5,29) rot=(0,0,1;0rad)
  Radius = 0.5
FEATURE [Part::Cylinder] Cylinder1101  label="Cylinder1479"
  Angle = 360
  AttacherType = Attacher::AttachEngine3D
  Height = 10
  Placement = pos=(-7,6.5,29) rot=(0,0,1;0rad)
  Radius = 0.5
FEATURE [Part::Cylinder] Cylinder1104  label="Cylinder1485"
  Angle = 360
  AttacherType = Attacher::AttachEngine3D
  Height = 15
  Placement = pos=(370,72.5,-22.85) rot=(0,1,0;1.5708rad)
  Radius = 1
FEATURE [Part::Cylinder] Cylinder1105  label="Cylinder1486"
  Angle = 360
  AttacherType = Attacher::AttachEngine3D
  Height = 15
  Placement = pos=(370,72.5,-58.15) rot=(0,1,0;1.5708rad)
  Radius = 1
FEATURE [Part::MultiFuse] Fusion675
  Placement = pos=(-1,0,3) rot=(0,0,1;0rad)
  Refine = true
  Shapes = -> [Cylinder1105,Cylinder1104]
FEATURE [Part::Box] Box653  label="Cube844"
  AttacherType = Attacher::AttachEngine3D
  Height = 6
  Length = 9
  Placement = pos=(372.5,66,-22.5) rot=(0,0,1;0rad)
  Width = 13
FEATURE [Part::Box] Box654  label="Cube845"
  AttacherType = Attacher::AttachEngine3D
  Height = 6
  Length = 9
  Placement = pos=(372.5,66,-58.5) rot=(0,0,1;0rad)
  Width = 13
FEATURE [Part::MultiFuse] Fusion676
  Refine = true
  Shapes = -> [Box653,Box654]
FEATURE [Part::Cut] Cut014189  label="hitec-hs85bb-mount"
  Base = -> Fusion676
  Placement = pos=(500.9,-389.5,93) rot=(-0.498707,-0.498707,0.708931;1.9082rad)
  Refine = true
  Tool = -> Fusion675
FEATURE [Part::Cylinder] Cylinder1106  label="Cylinder1487"
  Angle = 360
  AttacherType = Attacher::AttachEngine3D
  Height = 3.5
  Placement = pos=(6,6,20.5) rot=(0,0,1;0rad)
  Radius = 6
FEATURE [Part::Chamfer] Chamfer007038020005015
  Base = -> Box632
  Edges = 1 edges: [Edge4 r1=3.5 r2=5]
FEATURE [Part::MultiFuse] Fusion001005002004004005002010002003003003017007024041010023003003006006003006008021054006004013005009020003043002011002010006015002010005005003002003040  label="Fusion-0056"
  Refine = true
  Shapes = -> [Fillet425,Box634,Cylinder958,Cylinder1106,Chamfer007038020005015]
FEATURE [Part::MultiFuse] Fusion001005002004004005002010002003003003017007024041010023003003006006003006008021054006004013005009020003043002011002010006015002010005005003002003041  label="Fusion-0057"
  Placement = pos=(0,-0.5,-4) rot=(0,0,1;0rad)
  Refine = true
  Shapes = -> [Cylinder1100,Cylinder961,Cylinder1101]
FEATURE [Part::Cylinder] Cylinder1107  label="Cylinder1488"
  Angle = 360
  AttacherType = Attacher::AttachEngine3D
  Height = 10
  Placement = pos=(27,0,0) rot=(0,0,1;0rad)
  Radius = 1
FEATURE [Part::MultiFuse] Fusion001005002004004005002010002003003003017007024041010023003003006006003006008021054006004013005009020003043002011002010006015002010005005003002003042  label="Fusion-0058"
  Placement = pos=(-1.75,6,10) rot=(0,0,1;0rad)
  Refine = true
  Shapes = -> [Cylinder1107,Cylinder960]
FEATURE [Part::MultiFuse] Fusion001005002004004005002010002003003003017007024041010023003003006006003006008021054006004013005009020003043002011002010006015002010005005003002003043  label="Fusion-0059"
  Refine = true
  Shapes = -> [Fusion001005002004004005002010002003003003017007024041010023003003006006003006008021054006004013005009020003043002011002010006015002010005005003002003041,Fusion001005002004004005002010002003003003017007024041010023003003006006003006008021054006004013005009020003043002011002010006015002010005005003002003042]
FEATURE [Part::Cut] Cut012035015003002009024006019011009006027002007011007005004011002017019010028  label="EMAX-ES08MA-II"
  Base = -> Fusion001005002004004005002010002003003003017007024041010023003003006006003006008021054006004013005009020003043002011002010006015002010005005003002003040
  Refine = true
  Tool = -> Fusion001005002004004005002010002003003003017007024041010023003003006006003006008021054006004013005009020003043002011002010006015002010005005003002003043
FEATURE [Part::Cylinder] Cylinder1108  label="Cylinder1489"
  Angle = 360
  AttacherType = Attacher::AttachEngine3D
  Height = 12
  Placement = pos=(0,0,0) rot=(-1,0,0;1.5708rad)
  Radius = 0.9
FEATURE [Part::Cylinder] Cylinder1109  label="Cylinder1490"
  Angle = 360
  AttacherType = Attacher::AttachEngine3D
  Height = 12
  Placement = pos=(27.5,0,0) rot=(-1,0,0;1.5708rad)
  Radius = 0.9
FEATURE [Part::Box] Box655  label="Cube846"
  AttacherType = Attacher::AttachEngine3D
  Height = 12
  Length = 37
  Placement = pos=(-5,0,-6) rot=(0,0,1;0rad)
  Width = 9
FEATURE [Part::Box] Box656  label="Cube847"
  AttacherType = Attacher::AttachEngine3D
  Height = 12
  Length = 24
  Placement = pos=(1.5,0,-6) rot=(0,0,1;0rad)
  Width = 9
FEATURE [Part::Cut] Cut012035015003002009024006019011009006027002007011007005004011002017019010028002  label="Cut-0056"
  Base = -> Box655
  Refine = true
  Tool = -> Box656
FEATURE [Part::MultiFuse] Fusion001005002004004005002010002003003003017007024041010023003003006006003006008021054006004013005009020003043002011002010006015002010005005003002003044  label="Fusion-0060"
  Placement = pos=(-0.25,0,-1.5) rot=(0,0,1;0rad)
  Refine = true
  Shapes = -> [Cylinder1108,Cylinder1109]
FEATURE [Part::Cut] Cut012035015003002009024006019011009006027002007011007005004011002017019010028003  label="Cut-0057"
  Base = -> Cut012035015003002009024006019011009006027002007011007005004011002017019010028002
  Placement = pos=(495.774,-17,18.3564) rot=(0,1,0;0.340339rad)
  Refine = true
  Tool = -> Fusion001005002004004005002010002003003003017007024041010023003003006006003006008021054006004013005009020003043002011002010006015002010005005003002003044
FEATURE [Part::Cut] Cut012035015003002009024006019011009006027002007011007005004011002017019010028004  label="rear-platform-LEFTBASE"
  Base = -> Fusion001005002004004005002010002003003003017007024041010023003003006006003006008021054006004013005009020003043002011002010006015002010005005003002003039
  Refine = true
  Tool = -> Fusion001005002004004005002010002003003003017007024041010023003003006006003006008021054006004013005009020003043002011002010006015002010005005003002003030
FEATURE [Part::Feature] Part__Mirroring005002002002002002002002002022004003003002002004003002003003002002001  label="rear-platform-RIGHTBASE"
  Placement = pos=(0,-16,0) rot=(0,0,1;0rad)
  shape: bbox 131.3 x 88 x 55.12 mm, 151 faces (baked)
FEATURE [Part::Feature] Fusion001005002004004005002010002003003003017007024041010023003003006006003006008021054006004013005009020003043002011002010006015002010005005003002003024001  label="rear-platform-joining-screws003"
  shape: bbox 87.5 x 118 x 20.5 mm, 28 faces, 4 solids (baked)
FEATURE [Part::Cut] Cut012035015003002009024006019011009006027002007011007005004011002017019010028005  label="Cut-0086"
  Base = -> Part__Mirroring005002002002002002002002002022004003003002002004003002003003002002001
  Refine = true
  Tool = -> Fusion001005002004004005002010002003003003017007024041010023003003006006003006008021054006004013005009020003043002011002010006015002010005005003002003024001
FEATURE [Part::MultiFuse] Fusion001005002004004005002010002003003003017007024041010023003003006006003006008021054006004013005009020003043002011002010006015002010005005003002003024002  label="Fusion-0061"
  Refine = true
  Shapes = -> [Cut012035015003002009024006019011009006027002007011007005004011002017019010028004,Cut012035015003002009024006019011009006027002007011007005004011002017019010028003]
FEATURE [Part::Chamfer] Chamfer007038020005016
  Base = -> Fusion001005002004004005002010002003003003017007024041010023003003006006003006008021054006004013005009020003043002011002010006015002010005005003002003024002
  Edges = 2 edges r=6: [Edge29,Edge163]
FEATURE [Part::Fillet] Fillet001025008004009
  Base = -> Chamfer007038020005016
  Edges = 2 edges r=4: [Edge87,Edge279]
FEATURE [Part::Box] Box657  label="Cube848"
  AttacherType = Attacher::AttachEngine3D
  Height = 10
  Length = 15
  Placement = pos=(499.33,-34.25,22.5) rot=(0,1,0;0.305433rad)
  Width = 6
FEATURE [Part::Cut] Cut012035015003002009024006019011009006027002007011007005004011002017019010028006  label="Cut-0058"
  Base = -> Fillet001025008004009
  Refine = true
  Tool = -> Box657
FEATURE [Part::Feature] Cut012035015003002009024006019011009006027002007011007005004011002017019010028008  label="EMAX-ES08MA-II002"
  Placement = pos=(495.639,-2.044,12.035) rot=(0.971727,0.166953,-0.166953;1.59947rad)
  shape: bbox 34.17 x 29.5 x 27.5 mm, 29 faces (baked)
FEATURE [Part::Feature] Cut012035015003002009024006019011009006027002007011007005004011002017019010028009  label="spur_gear_12T002"
  Placement = pos=(7.25,-9.75,0) rot=(1,0,0;1.5708rad)
  shape: bbox 9 x 4.25 x 9 mm, 8 faces (baked)
FEATURE [Part::Feature] Cut012035015003002009024006019011009006027002007011007005004011002017019010028010  label="spur_gear_12T003"
  Placement = pos=(10,-7,0) rot=(0.707107,0,0.707107;3.14159rad)
  shape: bbox 4.25 x 9 x 9 mm, 8 faces (baked)
FEATURE [Part::MultiFuse] Fusion001005002004004005002010002003003003017007024041010023003003006006003006008021054006004013005009020003043002011002010006015002010005005003002003024003  label="spur_gears_12T-12T"
  Placement = pos=(554.305,-80.95,11.4404) rot=(0,1,0;0.314159rad)
  Refine = true
  Shapes = -> [Cut012035015003002009024006019011009006027002007011007005004011002017019010028009,Cut012035015003002009024006019011009006027002007011007005004011002017019010028010]
FEATURE [Part::MultiFuse] Fusion001005002004004005002010002003003003017007024041010023003003006006003006008021054006004013005009020003043002011002003  label="Fusion-314"
  Refine = true
  Shapes = -> [Cylinder1003,Cylinder1005]
FEATURE [Part::Fillet] Fillet001025008004010
  Base = -> Box220
  Edges = 1 edges r=5.5: [Edge2]
FEATURE [Part::Chamfer] Chamfer007038020005018
  Base = -> Fillet001025008004010
  Edges = 1 edges: [Edge3 r1=8 r2=4]
FEATURE [Part::Fillet] Fillet001025008004011
  Base = -> Chamfer007038020005018
  Edges = 1 edges r=1: [Edge2]
FEATURE [Part::Fillet] Fillet001025008007
  Base = -> Fusion001005002004004005002010002003003003017007024041010023003003006006003006008021054006004013005009020003043002011002010006015002010005005003002003005
  Edges = 4 edges r=2: [Edge4,Edge8,Edge16,Edge20]
FEATURE [Part::Cut] Cut012035015003002009024006019011009006027002007011007005004011002017019010028011  label="Cut-0059"
  Base = -> Fillet001025008004011
  Refine = true
  Tool = -> Box225
FEATURE [Part::MultiFuse] Fusion001005002004004005002010002003003003017007024041010023003003006006003006008021054006004013005009020003043002011002010006015002010005005003002003024004  label="Fusion-0062"
  Refine = true
  Shapes = -> [Cut012035015003002009024006019011009006027002007011007005004011002017019010028011,Fillet001025008007]
FEATURE [Part::Cut] Cut012035015003002009024006019011009006027002007011007005004011002017019010028012  label="Cut-0060"
  Base = -> Fusion001005002004004005002010002003003003017007024041010023003003006006003006008021054006004013005009020003043002011002010006015002010005005003002003024004
  Refine = true
  Tool = -> Cylinder1015
FEATURE [Part::Cut] Cut012035015003002009024006019011009006027002007011007005004011002017019010028013  label="Cut-0061"
  Base = -> Cut012035015003002009024006019011009006027002007011007005004011002017019010028012
  Refine = true
  Tool = -> Cylinder1068
FEATURE [Part::Cut] Cut012035015003002009024006019011009006027002007011007005004011002017019010028014  label="Cut-0062"
  Base = -> Cut012035015003002009024006019011009006027002007011007005004011002017019010028013
  Refine = true
  Tool = -> Box228
FEATURE [Part::Box] Box658  label="Cube849"
  AttacherType = Attacher::AttachEngine3D
  Height = 14.2
  Length = 60
  Placement = pos=(552.2,-62.2,-5) rot=(0,1,0;0rad)
  Width = 12.4
FEATURE [Part::Cut] Cut012035015003002009024006019011009006027002007011007005004011002017019010028015  label="Cut-0063"
  Base = -> Cut012035015003002009024006019011009006027002007011007005004011002017019010028014
  Refine = true
  Tool = -> Box658
FEATURE [Part::Cut] Cut012035015003002009024006019011009006027002007011007005004011002017019010028016  label="Cut-0064"
  Base = -> Cut012035015003002009024006019011009006027002007011007005004011002017019010028015
  Refine = true
  Tool = -> Fusion001005002004004005002010002003003003017007024041010023003003006006003006008021054006004013005009020003043002011002010006015002010005005003002003007
FEATURE [Part::Cylinder] Cylinder1112  label="Cylinder1493"
  Angle = 360
  AttacherType = Attacher::AttachEngine3D
  Height = 5
  Placement = pos=(561,-62.2,9.2) rot=(-1,0,0;1.5708rad)
  Radius = 4.8
FEATURE [Part::Cut] Cut012035015003002009024006019011009006027002007011007005004011002017019010028017  label="Cut-0065"
  Base = -> Cut012035015003002009024006019011009006027002007011007005004011002017019010028016
  Refine = true
  Tool = -> Cylinder1112
FEATURE [Part::Cylinder] Cylinder1113  label="Cylinder1494"
  Angle = 360
  AttacherType = Attacher::AttachEngine3D
  Height = 15
  Placement = pos=(570,-60.5,0) rot=(0,0,1;0rad)
  Radius = 1.2
FEATURE [Part::Cylinder] Cylinder1114  label="Cylinder1495"
  Angle = 360
  AttacherType = Attacher::AttachEngine3D
  Height = 15
  Placement = pos=(570,-51.5,0) rot=(0,0,1;0rad)
  Radius = 1.2
FEATURE [Part::Cylinder] Cylinder1115  label="Cylinder1496"
  Angle = 360
  AttacherType = Attacher::AttachEngine3D
  Height = 15
  Placement = pos=(608,-56,0) rot=(0,0,1;0rad)
  Radius = 1.2
FEATURE [Part::Cylinder] Cylinder1116  label="Cylinder1497"
  Angle = 360
  AttacherType = Attacher::AttachEngine3D
  Height = 15
  Placement = pos=(570,-51.5,0) rot=(0,0,1;0rad)
  Radius = 0.9
FEATURE [Part::Cylinder] Cylinder1117  label="Cylinder1498"
  Angle = 360
  AttacherType = Attacher::AttachEngine3D
  Height = 15
  Placement = pos=(608,-56,0) rot=(0,0,1;0rad)
  Radius = 0.9
FEATURE [Part::Cylinder] Cylinder1118  label="Cylinder1499"
  Angle = 360
  AttacherType = Attacher::AttachEngine3D
  Height = 15
  Placement = pos=(570,-60.5,0) rot=(0,0,1;0rad)
  Radius = 0.9
FEATURE [Part::MultiFuse] Fusion001005002004004005002010002003003003017007024041010023003003006006003006008021054006004013005009020003043002011002010006015002010005005003002003024006  label="Fusion-0064"
  Placement = pos=(0.5,0,0) rot=(0,0,1;0rad)
  Refine = true
  Shapes = -> [Cylinder1117,Cylinder1116,Cylinder1118]
FEATURE [Part::Cut] Cut012035015003002009024006019011009006027002007011007005004011002017019010028018  label="Cut-0066"
  Base = -> Cut012035015003002009024006019011009006027002007011007005004011002017019010028017
  Placement = pos=(24.8143,0,173.809) rot=(0,1,0;0.314159rad)
  Refine = true
  Tool = -> Fusion001005002004004005002010002003003003017007024041010023003003006006003006008021054006004013005009020003043002011002010006015002010005005003002003024006
FEATURE [Part::Feature] Face024
  Placement = pos=(0,0.2,0) rot=(0,0,1;0rad)
  shape: bbox 63 x 2.001e-07 x 13.34 mm, 1 faces, 0 solids (baked)
FEATURE [Part::Extrusion] Extrude026
  Base = -> Face024
  Dir = (0,1,0)
  DirMode = 0
  FaceMakerClass = Part::FaceMakerBullseye
  LengthFwd = 12
  LengthRev = 0
  Solid = true
  Symmetric = false
FEATURE [Part::Cylinder] Cylinder1119  label="Cylinder1500"
  Angle = 360
  AttacherType = Attacher::AttachEngine3D
  Height = 5
  Placement = pos=(561,-62,9.2) rot=(-1,0,0;1.5708rad)
  Radius = 4.8
FEATURE [Part::Cylinder] Cylinder1120  label="Cylinder1501"
  Angle = 360
  AttacherType = Attacher::AttachEngine3D
  Height = 5
  Placement = pos=(564.2,-55.75,9.2) rot=(0,1,0;1.5708rad)
  Radius = 5.5
FEATURE [Part::Cylinder] Cylinder1121  label="Cylinder1502"
  Angle = 360
  AttacherType = Attacher::AttachEngine3D
  Height = 10
  Placement = pos=(564.2,-55.75,9.2) rot=(0,1,0;1.5708rad)
  Radius = 3.1
FEATURE [Part::MultiFuse] Fusion001005002004004005002010002003003003017007024041010023003003006006003006008021054006004013005009020003043002011002010006015002010005005003002003024007  label="Fusion-0065"
  Refine = true
  Shapes = -> [Cylinder1121,Cylinder1120]
FEATURE [Part::Feature] Part__Mirroring005002002002002002002002002022004003003002002004003002003003002002002  label="motor_12V_20RPM009"
  Placement = pos=(569.2,-63,9.19986) rot=(0,0,1;0rad)
  shape: bbox 39 x 12.4 x 10.4 mm, 20 faces (baked)
FEATURE [Part::MultiFuse] Fusion001005002004004005002010002003003003017007024041010023003003006006003006008021054006004013005009020003043002011002010006015002010005005003002003024008  label="ramp-motor-carving001"
  Placement = pos=(-1,-0.25,0) rot=(0,0,1;0rad)
  Refine = true
  Shapes = -> [Fusion001005002004004005002010002003003003017007024041010023003003006006003006008021054006004013005009020003043002011002010006015002010005005003002003024007,Part__Mirroring005002002002002002002002002022004003003002002004003002003003002002002]
FEATURE [Part::Box] Box661  label="Cube852"
  AttacherType = Attacher::AttachEngine3D
  Height = 11
  Length = 22
  Placement = pos=(611.7,-66,20) rot=(0,1,0;1.5708rad)
  Width = 18
FEATURE [Part::Cylinder] Cylinder1123  label="Cylinder1504"
  Angle = 180
  AttacherType = Attacher::AttachEngine3D
  Height = 7
  Placement = pos=(561,-62,9.2) rot=(-1,0,0;1.5708rad)
  Radius = 5.5
FEATURE [Part::MultiFuse] Fusion001005002004004005002010002003003003017007024041010023003003006006003006008021054006004013005009020003043002011002010006015002010005005003002003024009  label="Fusion-0066"
  Refine = true
  Shapes = -> [Cylinder1123,Extrude026]
FEATURE [Part::Cut] Cut012035015003002009024006019011009006027002007011007005004011002017019010028019  label="Cut-0067"
  Base = -> Fusion001005002004004005002010002003003003017007024041010023003003006006003006008021054006004013005009020003043002011002010006015002010005005003002003024009
  Refine = true
  Tool = -> Fusion001005002004004005002010002003003003017007024041010023003003006006003006008021054006004013005009020003043002011002010006015002010005005003002003024008
FEATURE [Part::Cut] Cut012035015003002009024006019011009006027002007011007005004011002017019010028020  label="Cut-0068"
  Base = -> Cut012035015003002009024006019011009006027002007011007005004011002017019010028019
  Refine = true
  Tool = -> Cylinder1119
FEATURE [Part::MultiFuse] Fusion001005002004004005002010002003003003017007024041010023003003006006003006008021054006004013005009020003043002011002010006015002010005005003002003024005  label="Fusion-0063"
  Placement = pos=(0.5,0,0) rot=(0,0,1;0rad)
  Refine = true
  Shapes = -> [Cylinder1115,Cylinder1114,Cylinder1113]
FEATURE [Part::Cylinder] Cylinder1124  label="Cylinder1505"
  Angle = 360
  AttacherType = Attacher::AttachEngine3D
  Height = 16
  Placement = pos=(561,-64,9.2) rot=(-1,0,0;1.5708rad)
  Radius = 2
FEATURE [Part::Cut] Cut012035015003002009024006019011009006027002007011007005004011002017019010028021  label="Cut-0069"
  Base = -> Cut012035015003002009024006019011009006027002007011007005004011002017019010028020
  Refine = true
  Tool = -> Cylinder1124
FEATURE [Part::Cut] Cut012035015003002009024006019011009006027002007011007005004011002017019010028022  label="Cut-0070"
  Base = -> Cut012035015003002009024006019011009006027002007011007005004011002017019010028021
  Refine = true
  Tool = -> Fusion001005002004004005002010002003003003017007024041010023003003006006003006008021054006004013005009020003043002011002010006015002010005005003002003024005
FEATURE [Part::Cut] Cut012035015003002009024006019011009006027002007011007005004011002017019010028023  label="Cut-0076"
  Base = -> Cut012035015003002009024006019011009006027002007011007005004011002017019010028022
  Placement = pos=(24.8143,0,173.809) rot=(0,1,0;0.314159rad)
  Refine = true
  Tool = -> Box661
FEATURE [Part::Cut] Cut012035015003002009024006019011009006027002007011007005004011002017019010028024  label="Cut-0072"
  Base = -> Cut012035015003002009024006019011009006027002007011007005004011002017019010028018
  Refine = true
  Tool = -> Box224
FEATURE [Part::Box] Box662  label="Cube853"
  AttacherType = Attacher::AttachEngine3D
  Height = 2
  Length = 2
  Placement = pos=(699.25,-100,-31) rot=(0,1,0;0.314159rad)
  Width = 56
FEATURE [Part::Cut] Cut012035015003002009024006019011009006027002007011007005004011002017019010028025  label="Cut-0073"
  Base = -> Cut012035015003002009024006019011009006027002007011007005004011002017019010028024
  Refine = true
  Tool = -> Box662
FEATURE [Part::Feature] Fusion001005002004004005002010002003003003017007024041010023003003006006003006008021054006004013005009020003043002011002010006015002010005005003002003024010  label="Fusion-0067"
  Placement = pos=(1.2,3.2,3.5) rot=(0,0,1;0rad)
  shape: bbox 4 x 6 x 4 mm, 6 faces (baked)
FEATURE [Part::Feature] Fusion001005002004004005002010002003003003017007024041010023003003006006003006008021054006004013005009020003043002011002010006015002010005005003002003024011  label="Fusion-0068"
  Placement = pos=(105.7,3.2,-26.5) rot=(0,0,1;0rad)
  shape: bbox 4 x 6 x 4 mm, 6 faces (baked)
FEATURE [Part::Feature] Fusion001005002004004005002010002003003003017007024041010023003003006006003006008021054006004013005009020003043002011002010006015002010005005003002003024012  label="Fusion-0069"
  Placement = pos=(51.7,3.2,-11.5) rot=(0,0,1;0rad)
  shape: bbox 4 x 6 x 4 mm, 6 faces (baked)
FEATURE [Part::MultiFuse] Fusion001005002004004005002010002003003003017007024041010023003003006006003006008021054006004013005009020003043002011002010006015002010005005003002003024013  label="Fusion-0070"
  Refine = true
  Shapes = -> [Fusion001005002004004005002010002003003003017007024041010023003003006006003006008021054006004013005009020003043002011002010006015002010005005003002003024010,Fusion001005002004004005002010002003003003017007024041010023003003006006003006008021054006004013005009020003043002011002010006015002010005005003002003024011,+1 more]
FEATURE [Part::Feature] Part__Mirroring005002002002002002002002002022004003003002002004003002003003002002003001  label="Fusion-0071"
  Placement = pos=(0,-144,0) rot=(0,0,1;0rad)
  shape: bbox 108.5 x 6 x 34 mm, 18 faces, 3 solids (baked)
FEATURE [Part::MultiFuse] Fusion001005002004004005002010002003003003017007024041010023003003006006003006008021054006004013005009020003043002011002010006015002010005005003002003024014  label="Fusion-0072"
  Refine = true
  Shapes = -> [Part__Mirroring005002002002002002002002002022004003003002002004003002003003002002003001,Fusion001005002004004005002010002003003003017007024041010023003003006006003006008021054006004013005009020003043002011002010006015002010005005003002003024013]
FEATURE [Part::Feature] Fillet001025008004012  label="ramp-right-int-side"
  Placement = pos=(-0.04,128,0) rot=(0,0,1;0rad)
  shape: bbox 152.6 x 4.2 x 60.33 mm, 23 faces (baked)
FEATURE [Part::Feature] Part__Mirroring005002002002002002002002002022004003003002002004003002001001  label="ramp-right-ext-side"
  Placement = pos=(0,-16,0) rot=(0,0,1;0rad)
  shape: bbox 152.6 x 4.2 x 60.33 mm, 23 faces (baked)
FEATURE [Part::Chamfer] Chamfer007038020005019
  Base = -> Cut012035015003002009024006019011009006027002007011007005004011002017019010028025
  Edges = 1 edges r=3.2: [Edge44]
FEATURE [Part::Cut] Cut012035015003002009024006019011009006027002007011007005004011002017019010028026  label="Cut-0074"
  Base = -> Chamfer007038020005019
  Refine = true
  Tool = -> Fusion001005002004004005002010002003003003017007024041010023003003006006003006008021054006004013005009020003043002011002010006015002010005005003002003024014
FEATURE [Part::Box] Box663  label="Cube854"
  AttacherType = Attacher::AttachEngine3D
  Height = 3
  Length = 3
  Placement = pos=(599,-64.8,-6) rot=(0,1,0;0.314159rad)
  Width = 15
FEATURE [Part::Cut] Cut012035015003002009024006019011009006027002007011007005004011002017019010028027  label="Cut-0077"
  Base = -> Cut012035015003002009024006019011009006027002007011007005004011002017019010028026
  Refine = true
  Tool = -> Box663
FEATURE [Part::Box] Box664  label="Cube855"
  AttacherType = Attacher::AttachEngine3D
  Height = 3
  Length = 3
  Placement = pos=(599,-64.8,-6) rot=(0,1,0;0.314159rad)
  Width = 15
FEATURE [Part::Cut] Cut012035015003002009024006019011009006027002007011007005004011002017019010028028  label="ramp-right-body-motor-cover"
  Base = -> Cut012035015003002009024006019011009006027002007011007005004011002017019010028023
  Placement = pos=(0,128,0) rot=(0,0,1;0rad)
  Refine = true
  Tool = -> Box664
FEATURE [Part::Cylinder] Cylinder1125  label="Cylinder1506"
  Angle = 360
  AttacherType = Attacher::AttachEngine3D
  Height = 5
  Placement = pos=(561,-63,9.2) rot=(-1,0,0;1.5708rad)
  Radius = 2.7
FEATURE [Part::Feature] Part__Mirroring005002002002002002002002002022004003003002002004003002003003002002003002001  label="ramp-left-body-motor-cover"
  Placement = pos=(0,-144,0) rot=(0,0,1;0rad)
  shape: bbox 62.57 x 12 x 31.9 mm, 36 faces (baked)
FEATURE [Part::Cut] Cut012035015003002009024006019011009006027002007011007005004011002017019010028029  label="ramp-right-body"
  Base = -> Cut012035015003002009024006019011009006027002007011007005004011002017019010028027
  Placement = pos=(0,128,0) rot=(0,0,1;0rad)
  Refine = true
  Tool = -> Cylinder1125
FEATURE [Part::Feature] Part__Mirroring005002002002002002002002002022004003003002002004003002003003002002003003002001  label="ramp-left-body"
  Placement = pos=(0,-144,0) rot=(0,0,1;0rad)
  shape: bbox 143.7 x 47.6 x 45.18 mm, 83 faces (baked)
FEATURE [App::DocumentObjectGroup] Group007  label="Rear ramp"
  Group = -> [Fillet001025008004,Part__Mirroring005002002002002002002002002022004003003002002004003002001,Part__Mirroring005002002002002002002002002022004003003002002004003002002,Cylinder941,Fusion001005002004004005002010002003003003017007024041010023003003006006003006008021054006004013005009020003043002011002010006015002010005005003002003024003,Fillet001025008004012,+5 more]
FEATURE [Part::Cylinder] Cylinder1127  label="Cylinder1508"
  Angle = 360
  AttacherType = Attacher::AttachEngine3D
  Height = 83
  Placement = pos=(538,-98,16) rot=(-1,0,0;1.5708rad)
  Radius = 3.25
FEATURE [Part::Cylinder] Cylinder1128  label="Cylinder1509"
  Angle = 360
  AttacherType = Attacher::AttachEngine3D
  Height = 88
  Placement = pos=(538,-96,16) rot=(-1,0,0;1.5708rad)
  Radius = 1.7
FEATURE [Part::Cylinder] Cylinder1129  label="Cylinder1510"
  Angle = 360
  AttacherType = Attacher::AttachEngine3D
  Height = 118
  Placement = pos=(538,-98,16) rot=(-1,0,0;1.5708rad)
  Radius = 1.25
FEATURE [Part::MultiFuse] Fusion001005002004004005002010002003003003017007024041010023003003006006003006008021054006004013005009020003043002011002010006015002010005005003002003024015  label="Fusion-0073"
  Refine = true
  Shapes = -> [Cylinder1129,Cylinder1128,Cylinder1127]
FEATURE [Part::Feature] Fusion001005002004004005002010002003003003017007024041010023003003006006003006008021054006004013005009020003043002011002010006015002010005005003002003024015001  label="Fusion-0074"
  Placement = pos=(-26,0,9) rot=(0,0,1;0rad)
  shape: bbox 6.5 x 118 x 6.5 mm, 7 faces (baked)
FEATURE [Part::Feature] Fusion001005002004004005002010002003003003017007024041010023003003006006003006008021054006004013005009020003043002011002010006015002010005005003002003024015002  label="Fusion-0075"
  Placement = pos=(-81,0,14) rot=(0,0,1;0rad)
  shape: bbox 6.5 x 118 x 6.5 mm, 7 faces (baked)
FEATURE [Part::Feature] Fusion001005002004004005002010002003003003017007024041010023003003006006003006008021054006004013005009020003043002011002010006015002010005005003002003024015003  label="Fusion-0076"
  Placement = pos=(-67,0,14) rot=(0,0,1;0rad)
  shape: bbox 6.5 x 118 x 6.5 mm, 7 faces (baked)
FEATURE [Part::MultiFuse] Fusion001005002004004005002010002003003003017007024041010023003003006006003006008021054006004013005009020003043002011002010006015002010005005003002003024015004  label="rear-platform-joining-screws004"
  Refine = true
  Shapes = -> [Fusion001005002004004005002010002003003003017007024041010023003003006006003006008021054006004013005009020003043002011002010006015002010005005003002003024015,Fusion001005002004004005002010002003003003017007024041010023003003006006003006008021054006004013005009020003043002011002010006015002010005005003002003024015002,+2 more]
FEATURE [Part::Cut] Cut012035015003002009024006019011009006027002007011007005004011002017019010028031  label="Cut-0085"
  Base = -> Cut012035015003002009024006019011009006027002007011007005004011002017019010028006
  Refine = true
  Tool = -> Fusion001005002004004005002010002003003003017007024041010023003003006006003006008021054006004013005009020003043002011002010006015002010005005003002003024015004
FEATURE [Part::Box] Box665  label="Cube856"
  AttacherType = Attacher::AttachEngine3D
  Height = 32.5
  Length = 10
  Placement = pos=(542,-77,-19) rot=(0,0,1;0rad)
  Width = 10
FEATURE [Part::Chamfer] Chamfer007038020005020
  Base = -> Box665
  Edges = 2 edges: [Edge2 r1=10 r2=1.25,Edge6 r1=10 r2=1.25]
FEATURE [Part::Cylinder] Cylinder1130  label="Cylinder1511"
  Angle = 360
  AttacherType = Attacher::AttachEngine3D
  Height = 16
  Placement = pos=(547,-80,9) rot=(-1,0,0;1.5708rad)
  Radius = 1.5
FEATURE [Part::Feature] Fusion001005002004004005002010002003003003017007024041010023003003006006003006008021054006004013005009020003043002011002010006015002010005005003002003024015005  label="Fusion-0077"
  Placement = pos=(0,8,1) rot=(0,0,1;0rad)
  shape: bbox 6.4 x 6.4 x 16 mm, 6 faces (baked)
FEATURE [Part::Cut] Cut012035015003002009024006019011009006027002007011007005004011002017019010028032  label="Cut-0078"
  Base = -> Chamfer007038020005020
  Refine = true
  Tool = -> Fusion001005002004004005002010002003003003017007024041010023003003006006003006008021054006004013005009020003043002011002010006015002010005005003002003024015005
FEATURE [Part::Cut] Cut012035015003002009024006019011009006027002007011007005004011002017019010028033  label="Cut-0079"
  Base = -> Cut012035015003002009024006019011009006027002007011007005004011002017019010028032
  Refine = true
  Tool = -> Cylinder1130
FEATURE [Part::Fillet] Fillet001025008004013
  Base = -> Cut012035015003002009024006019011009006027002007011007005004011002017019010028033
  Edges = 2 edges r=3.75: [Edge11,Edge21]
FEATURE [Part::Fillet] Fillet001025008004014
  Base = -> Fillet001025008004013
  Edges = 2 edges r=8: [Edge11,Edge24]
FEATURE [Part::Cylinder] Cylinder1131  label="Cylinder1512"
  Angle = 360
  AttacherType = Attacher::AttachEngine3D
  Height = 138
  Placement = pos=(549.5,-77,-3) rot=(-1,0,0;1.5708rad)
  Radius = 1.5
FEATURE [Part::Cut] Cut012035015003002009024006019011009006027002007011007005004011002017019010028034  label="Cut-0080"
  Base = -> Fillet001025008004014
  Placement = pos=(0,0,-3) rot=(0,0,1;0rad)
  Refine = true
  Tool = -> Cylinder1131
FEATURE [Part::Cylinder] Cylinder1132  label="Cylinder1513"
  Angle = 360
  AttacherType = Attacher::AttachEngine3D
  Height = 10
  Placement = pos=(547,-77,6) rot=(-1,0,0;1.5708rad)
  Radius = 2.1
FEATURE [Part::Cut] Cut012035015003002009024006019011009006027002007011007005004011002017019010028035  label="rear-stabilizer-body-left"
  Base = -> Cut012035015003002009024006019011009006027002007011007005004011002017019010028034
  Refine = true
  Tool = -> Cylinder1132
FEATURE [Part::Box] Box666  label="Cube857"
  AttacherType = Attacher::AttachEngine3D
  Height = 10
  Length = 10
  Placement = pos=(475,-96,26) rot=(0,0,1;0rad)
  Width = 5
FEATURE [Part::Box] Box667  label="Cube858"
  AttacherType = Attacher::AttachEngine3D
  Height = 5
  Length = 5
  Placement = pos=(477.5,-96,25) rot=(0,0,1;0rad)
  Width = 5
FEATURE [Part::Cylinder] Cylinder1133  label="Cylinder1514"
  Angle = 360
  AttacherType = Attacher::AttachEngine3D
  Height = 5
  Placement = pos=(480,-96,30) rot=(-1,0,0;1.5708rad)
  Radius = 2.7
FEATURE [Part::MultiFuse] Fusion001005002004004005002010002003003003017007024041010023003003006006003006008021054006004013005009020003043002011002010006015002010005005003002003024015006  label="Fusion-0078"
  Refine = true
  Shapes = -> [Box667,Cylinder1133]
FEATURE [Part::Cut] Cut012035015003002009024006019011009006027002007011007005004011002017019010028036  label="Cut-0081"
  Base = -> Box666
  Refine = true
  Tool = -> Fusion001005002004004005002010002003003003017007024041010023003003006006003006008021054006004013005009020003043002011002010006015002010005005003002003024015006
FEATURE [Part::Chamfer] Chamfer007038020005021
  Base = -> Cut012035015003002009024006019011009006027002007011007005004011002017019010028036
  Edges = 1 edges: [Edge22 r1=0.5 r2=1.5]
FEATURE [Part::Chamfer] Chamfer007038020005022
  Base = -> Chamfer007038020005021
  Edges = 1 edges: [Edge28 r1=0.5 r2=1.5]
  Placement = pos=(883,63.5,60) rot=(0,1,0;3.14159rad)
FEATURE [App::DocumentObjectGroup] Group005  label="Parts"
  Group = -> [Cut012035015003002009024006019011009006027002007011007005004011002,Fusion001005002004004005002010002003003003017007024041010023003003006006003006008021054006004013005009020003043002011002010006012,Fusion001005002004004005002010002003003003017007024041010023003003006006003006008021054006004013005009020003043002011002010006010,Part__Mirroring005002002002002002002002002021,+23 more]
FEATURE [Part::Feature] Chamfer007038020005022001  label="Chamfer007038020005023"
  Placement = pos=(883,63.5,60) rot=(0,1,0;3.14159rad)
  shape: bbox 10 x 5 x 10 mm, 12 faces (baked)
FEATURE [Part::Feature] Chamfer007038020005022002  label="Chamfer007038020005024"
  Placement = pos=(883,107.5,60) rot=(0,1,0;3.14159rad)
  shape: bbox 10 x 5 x 10 mm, 12 faces (baked)
FEATURE [Part::Feature] Chamfer007038020005022003  label="Chamfer007038020005025"
  Placement = pos=(797,63.5,60) rot=(0,1,0;3.14159rad)
  shape: bbox 10 x 5 x 10 mm, 12 faces (baked)
FEATURE [Part::Feature] Chamfer007038020005022004  label="Chamfer007038020005026"
  Placement = pos=(797,107.5,60) rot=(0,1,0;3.14159rad)
  shape: bbox 10 x 5 x 10 mm, 12 faces (baked)
FEATURE [Part::Box] Box669  label="Cube860"
  AttacherType = Attacher::AttachEngine3D
  Height = 8
  Length = 10
  Placement = pos=(312,-32.5,16) rot=(0,0,1;0rad)
  Width = 5
FEATURE [Part::Box] Box670  label="Cube861"
  AttacherType = Attacher::AttachEngine3D
  Height = 2
  Length = 96
  Placement = pos=(312,-32.5,14) rot=(0,0,1;0rad)
  Width = 49
FEATURE [Part::Box] Box671  label="Cube862"
  AttacherType = Attacher::AttachEngine3D
  Height = 14
  Length = 2
  Placement = pos=(406,-32.5,16) rot=(0,0,1;0rad)
  Width = 49
FEATURE [Part::Box] Box672  label="Cube863"
  AttacherType = Attacher::AttachEngine3D
  Height = 12
  Length = 2
  Placement = pos=(406,-10,18) rot=(0,0,1;0rad)
  Width = 4
FEATURE [Part::Box] Box673  label="Cube864"
  AttacherType = Attacher::AttachEngine3D
  Height = 14
  Length = 2
  Placement = pos=(312,-32.5,16) rot=(0,0,1;0rad)
  Width = 49
FEATURE [Part::Feature] Chamfer007038020005022005  label="Chamfer007038020005027"
  Placement = pos=(797,102,60) rot=(0,1,0;3.14159rad)
  shape: bbox 10 x 5 x 10 mm, 12 faces (baked)
FEATURE [Part::Feature] Chamfer007038020005022006  label="Chamfer007038020005028"
  Placement = pos=(797,69,60) rot=(0,1,0;3.14159rad)
  shape: bbox 10 x 5 x 10 mm, 12 faces (baked)
FEATURE [Part::Box] Box674  label="Cube865"
  AttacherType = Attacher::AttachEngine3D
  Height = 18
  Length = 12
  Placement = pos=(312,-27.5,13) rot=(0,0,1;0rad)
  Width = 39
FEATURE [Part::Box] Box675  label="Cube866"
  AttacherType = Attacher::AttachEngine3D
  Height = 2
  Length = 12
  Placement = pos=(311,-27,16) rot=(0,0,1;0rad)
  Width = 38
FEATURE [Part::Box] Box676  label="Cube867"
  AttacherType = Attacher::AttachEngine3D
  Height = 3.5
  Length = 9
  Placement = pos=(324,-13,16) rot=(0,0,1;0rad)
  Width = 10
FEATURE [Part::Box] Box677  label="Cube868"
  AttacherType = Attacher::AttachEngine3D
  Height = 2
  Length = 5
  Placement = pos=(326,-13,16) rot=(0,0,1;0rad)
  Width = 10
FEATURE [Part::Cut] Cut012035015003002009024006019011009006027002007011007005004011002017019010028039  label="Cut-0084"
  Base = -> Box676
  Placement = pos=(10,0,0) rot=(0,0,1;0rad)
  Refine = true
  Tool = -> Box677
FEATURE [Part::Box] Box679  label="Cube870"
  AttacherType = Attacher::AttachEngine3D
  Height = 2
  Length = 85
  Placement = pos=(226,-32.5,16) rot=(0,0,1;0rad)
  Width = 49
FEATURE [Part::Feature] Chamfer007038020005022007  label="Chamfer007038020005029"
  Placement = pos=(711,107.5,60) rot=(0,1,0;3.14159rad)
  shape: bbox 10 x 5 x 10 mm, 12 faces (baked)
FEATURE [Part::Feature] Chamfer007038020005022008  label="Chamfer007038020005030"
  Placement = pos=(711,63.5,60) rot=(0,1,0;3.14159rad)
  shape: bbox 10 x 5 x 10 mm, 12 faces (baked)
FEATURE [Part::Box] Box680  label="Cube871"
  AttacherType = Attacher::AttachEngine3D
  Height = 8
  Length = 85
  Placement = pos=(226,11.5,16) rot=(0,0,1;0rad)
  Width = 5
FEATURE [Part::MultiFuse] Fusion001005002004004005002010002003003003017007024041010023003003006006003006008021054006004013005009020003043002011002010006015002010005005003002003024015010  label="Fusion-0082"
  Refine = true
  Shapes = -> [Box675,Box679]
FEATURE [Part::Box] Box681  label="Cube872"
  AttacherType = Attacher::AttachEngine3D
  Height = 8
  Length = 85
  Placement = pos=(226,-32.5,16) rot=(0,0,1;0rad)
  Width = 5
FEATURE [Part::Box] Box682  label="Cube873"
  AttacherType = Attacher::AttachEngine3D
  Height = 8
  Length = 13
  Placement = pos=(309,-27,16) rot=(0,0,1;0rad)
  Width = 5
FEATURE [Part::Box] Box683  label="Cube874"
  AttacherType = Attacher::AttachEngine3D
  Height = 8
  Length = 2
  Placement = pos=(309,-32.5,16) rot=(0,0,1;0rad)
  Width = 10.5
FEATURE [Part::Box] Box684  label="Cube875"
  AttacherType = Attacher::AttachEngine3D
  Height = 8
  Length = 2
  Placement = pos=(309,6,16) rot=(0,0,1;0rad)
  Width = 10.5
FEATURE [Part::Box] Box685  label="Cube876"
  AttacherType = Attacher::AttachEngine3D
  Height = 8
  Length = 13
  Placement = pos=(309,6,16) rot=(0,0,1;0rad)
  Width = 5
FEATURE [Part::Box] Box686  label="Cube877"
  AttacherType = Attacher::AttachEngine3D
  Height = 7
  Length = 2
  Placement = pos=(226,-32.5,16) rot=(0,0,1;0rad)
  Width = 49
FEATURE [Part::MultiFuse] Fusion001005002004004005002010002003003003017007024041010023003003006006003006008021054006004013005009020003043002011002010006015002010005005003002003024015011  label="Fusion-0083"
  Refine = true
  Shapes = -> [Box686,Chamfer007038020005022008,Chamfer007038020005022007,Fusion001005002004004005002010002003003003017007024041010023003003006006003006008021054006004013005009020003043002011002010006015002010005005003002003024015010,Chamfer007038020005022006,Box685,Box682,Chamfer007038020005022005,Box684,Box681,Box680,Box683]
FEATURE [Part::Fillet] Fillet001025008004015002
  Base = -> Fusion001005002004004005002010002003003003017007024041010023003003006006003006008021054006004013005009020003043002011002010006015002010005005003002003024015011
  Edges = 2 edges r=4: [Edge85,Edge88]
FEATURE [Part::Chamfer] Chamfer007038020005022009
  Base = -> Fillet001025008004015002
  Edges = 1 edges r=1: [Edge21]
FEATURE [Part::Box] Box687  label="Cube878"
  AttacherType = Attacher::AttachEngine3D
  Height = 2
  Length = 5
  Placement = pos=(232,-32.5,32) rot=(0,0,1;0rad)
  Width = 49
FEATURE [Part::Cut] Cut012035015003002009024006019011009006027002007011007005004011002017019010028040  label="battery-holder"
  Base = -> Chamfer007038020005022009
  Refine = true
  Tool = -> Box687
FEATURE [Part::Cylinder] Cylinder1134  label="Cylinder1515"
  Angle = 360
  AttacherType = Attacher::AttachEngine3D
  Height = 25
  Placement = pos=(550,59.5,-14) rot=(0,1,0;0.610865rad)
  Radius = 1.1
FEATURE [Part::Cylinder] Cylinder1135  label="Cylinder1516"
  Angle = 360
  AttacherType = Attacher::AttachEngine3D
  Height = 25
  Placement = pos=(550,52.5,-14) rot=(0,1,0;0.610865rad)
  Radius = 1.1
FEATURE [Part::MultiFuse] Fusion001005002004004005002010002003003003017007024041010023003003006006003006008021054006004013005009020003043002011002010006015002010005005003002003024015012  label="Fusion-0084"
  Refine = true
  Shapes = -> [Cylinder1134,Cylinder1135]
FEATURE [Part::Cylinder] Cylinder1136  label="Cylinder1517"
  Angle = 360
  AttacherType = Attacher::AttachEngine3D
  Height = 25
  Placement = pos=(550,52.5,-14) rot=(0,1,0;0.610865rad)
  Radius = 1.1
FEATURE [Part::Cylinder] Cylinder1137  label="Cylinder1518"
  Angle = 360
  AttacherType = Attacher::AttachEngine3D
  Height = 25
  Placement = pos=(550,59.5,-14) rot=(0,1,0;0.610865rad)
  Radius = 1.1
FEATURE [Part::MultiFuse] Fusion001005002004004005002010002003003003017007024041010023003003006006003006008021054006004013005009020003043002011002010006015002010005005003002003024015013  label="Fusion-0085"
  Placement = pos=(0,-128,0) rot=(0,0,1;0rad)
  Refine = true
  Shapes = -> [Cylinder1137,Cylinder1136]
FEATURE [Part::MultiFuse] Fusion001005002004004005002010002003003003017007024041010023003003006006003006008021054006004013005009020003043002011002010006015002010005005003002003024015014  label="Fusion-0086"
  Refine = true
  Shapes = -> [Fusion001005002004004005002010002003003003017007024041010023003003006006003006008021054006004013005009020003043002011002010006015002010005005003002003024015013,Fusion001005002004004005002010002003003003017007024041010023003003006006003006008021054006004013005009020003043002011002010006015002010005005003002003024015012]
FEATURE [Part::Cut] Cut012035015003002009024006019011009006027002007011007005004011002017019010028041  label="rear-platform-left"
  Base = -> Cut012035015003002009024006019011009006027002007011007005004011002017019010028031
  Refine = true
  Tool = -> Fusion001005002004004005002010002003003003017007024041010023003003006006003006008021054006004013005009020003043002011002010006015002010005005003002003024015014
FEATURE [Part::Cylinder] Cylinder1138  label="Cylinder1519"
  Angle = 360
  AttacherType = Attacher::AttachEngine3D
  Height = 25
  Placement = pos=(550,52.5,-14) rot=(0,1,0;0.610865rad)
  Radius = 1.1
FEATURE [Part::Cylinder] Cylinder1139  label="Cylinder1520"
  Angle = 360
  AttacherType = Attacher::AttachEngine3D
  Height = 25
  Placement = pos=(550,59.5,-14) rot=(0,1,0;0.610865rad)
  Radius = 1.1
FEATURE [Part::Cylinder] Cylinder1140  label="Cylinder1521"
  Angle = 360
  AttacherType = Attacher::AttachEngine3D
  Height = 25
  Placement = pos=(550,52.5,-14) rot=(0,1,0;0.610865rad)
  Radius = 1.1
FEATURE [Part::MultiFuse] Fusion001005002004004005002010002003003003017007024041010023003003006006003006008021054006004013005009020003043002011002010006015002010005005003002003024015016  label="Fusion-0088"
  Placement = pos=(0,-128,0) rot=(0,0,1;0rad)
  Refine = true
  Shapes = -> [Cylinder1139,Cylinder1140]
FEATURE [Part::Cylinder] Cylinder1141  label="Cylinder1522"
  Angle = 360
  AttacherType = Attacher::AttachEngine3D
  Height = 25
  Placement = pos=(550,59.5,-14) rot=(0,1,0;0.610865rad)
  Radius = 1.1
FEATURE [Part::MultiFuse] Fusion001005002004004005002010002003003003017007024041010023003003006006003006008021054006004013005009020003043002011002010006015002010005005003002003024015017  label="Fusion-0089"
  Refine = true
  Shapes = -> [Cylinder1141,Cylinder1138]
FEATURE [Part::MultiFuse] Fusion001005002004004005002010002003003003017007024041010023003003006006003006008021054006004013005009020003043002011002010006015002010005005003002003024015015  label="Fusion-0087"
  Refine = true
  Shapes = -> [Fusion001005002004004005002010002003003003017007024041010023003003006006003006008021054006004013005009020003043002011002010006015002010005005003002003024015016,Fusion001005002004004005002010002003003003017007024041010023003003006006003006008021054006004013005009020003043002011002010006015002010005005003002003024015017]
FEATURE [Part::Cut] Cut012035015003002009024006019011009006027002007011007005004011002017019010028042  label="rear-platform-right"
  Base = -> Cut012035015003002009024006019011009006027002007011007005004011002017019010028005
  Refine = true
  Tool = -> Fusion001005002004004005002010002003003003017007024041010023003003006006003006008021054006004013005009020003043002011002010006015002010005005003002003024015015
FEATURE [Part::Box] Box688  label="Cube879"
  AttacherType = Attacher::AttachEngine3D
  Height = 5
  Length = 12
  Placement = pos=(540.5,-29,-8.5) rot=(0,0,1;0rad)
  Width = 10
FEATURE [Part::Box] Box689  label="Cube880"
  AttacherType = Attacher::AttachEngine3D
  Height = 5
  Length = 11
  Placement = pos=(531.5,-34,-8.5) rot=(0,0,1;0rad)
  Width = 5
FEATURE [Part::Cylinder] Cylinder1142  label="Cylinder1523"
  Angle = 360
  AttacherType = Attacher::AttachEngine3D
  Height = 10
  Placement = pos=(549.5,-29,-6) rot=(-1,0,0;1.5708rad)
  Radius = 1.7
FEATURE [Part::Box] Box690  label="Cube881"
  AttacherType = Attacher::AttachEngine3D
  Height = 3
  Length = 2.4
  Placement = pos=(548.3,-29,-6.5) rot=(0,0,1;0rad)
  Width = 10
FEATURE [Part::MultiFuse] Fusion001005002004004005002010002003003003017007024041010023003003006006003006008021054006004013005009020003043002011002010006015002010005005003002003024015018  label="Fusion-0090"
  Refine = true
  Shapes = -> [Box690,Cylinder1142]
FEATURE [Part::MultiFuse] Fusion001005002004004005002010002003003003017007024041010023003003006006003006008021054006004013005009020003043002011002010006015002010005005003002003024015019  label="Fusion-0091"
  Refine = true
  Shapes = -> [Box688,Box689]
FEATURE [Part::Cut] Cut012035015003002009024006019011009006027002007011007005004011002017019010028043  label="Cut-0087"
  Base = -> Fusion001005002004004005002010002003003003017007024041010023003003006006003006008021054006004013005009020003043002011002010006015002010005005003002003024015019
  Refine = true
  Tool = -> Fusion001005002004004005002010002003003003017007024041010023003003006006003006008021054006004013005009020003043002011002010006015002010005005003002003024015018
FEATURE [Part::Cylinder] Cylinder1143  label="Cylinder1524"
  Angle = 360
  AttacherType = Attacher::AttachEngine3D
  Height = 11
  Placement = pos=(531.5,-31.5,-6) rot=(0,1,0;1.5708rad)
  Radius = 1.1
FEATURE [Part::Cut] Cut012035015003002009024006019011009006027002007011007005004011002017019010028044  label="Cut-0088"
  Base = -> Cut012035015003002009024006019011009006027002007011007005004011002017019010028043
  Refine = true
  Tool = -> Cylinder1143
FEATURE [Part::Cylinder] Cylinder1144  label="Cylinder1525"
  Angle = 360
  AttacherType = Attacher::AttachEngine3D
  Height = 10
  Placement = pos=(543,43,-6) rot=(0,1,0;0rad)
  Radius = 1.2
FEATURE [Part::Box] Box691  label="Cube882"
  AttacherType = Attacher::AttachEngine3D
  Height = 5
  Length = 6
  Placement = pos=(540,28,-2.5) rot=(0,0,1;0rad)
  Width = 19
FEATURE [Part::Cylinder] Cylinder1145  label="Cylinder1526"
  Angle = 360
  AttacherType = Attacher::AttachEngine3D
  Height = 10
  Placement = pos=(543,32,-6) rot=(0,1,0;0rad)
  Radius = 1.2
FEATURE [Part::MultiFuse] Fusion001005002004004005002010002003003003017007024041010023003003006006003006008021054006004013005009020003043002011002010006015002010005005003002003024015020  label="Fusion-0092"
  Refine = true
  Shapes = -> [Cylinder1144,Cylinder1145]
FEATURE [Part::Cylinder] Cylinder1146  label="Cylinder1527"
  Angle = 360
  AttacherType = Attacher::AttachEngine3D
  Height = 10
  Placement = pos=(539,39,0) rot=(0,1,0;1.65806rad)
  Radius = 1
FEATURE [Part::Cylinder] Cylinder1147  label="Cylinder1528"
  Angle = 360
  AttacherType = Attacher::AttachEngine3D
  Height = 10
  Placement = pos=(539,36,0) rot=(0,1,0;1.65806rad)
  Radius = 1
FEATURE [Part::MultiFuse] Fusion001005002004004005002010002003003003017007024041010023003003006006003006008021054006004013005009020003043002011002010006015002010005005003002003024015021  label="Fusion-0093"
  Refine = true
  Shapes = -> [Cylinder1146,Cylinder1147]
FEATURE [Part::MultiFuse] Fusion001005002004004005002010002003003003017007024041010023003003006006003006008021054006004013005009020003043002011002010006015002010005005003002003024015022  label="Fusion-0094"
  Refine = true
  Shapes = -> [Fusion001005002004004005002010002003003003017007024041010023003003006006003006008021054006004013005009020003043002011002010006015002010005005003002003024015020,Fusion001005002004004005002010002003003003017007024041010023003003006006003006008021054006004013005009020003043002011002010006015002010005005003002003024015021]
FEATURE [Part::Cut] Cut012035015003002009024006019011009006027002007011007005004011002017019010028045  label="Cut-0089"
  Base = -> Box691
  Refine = true
  Tool = -> Fusion001005002004004005002010002003003003017007024041010023003003006006003006008021054006004013005009020003043002011002010006015002010005005003002003024015022
FEATURE [Part::Chamfer] Chamfer007038020005022011
  Base = -> Cut012035015003002009024006019011009006027002007011007005004011002017019010028045
  Edges = 2 edges r=1.2: [Edge16,Edge17]
FEATURE [Part::Chamfer] Chamfer007038020005022012  label="rear-platform-left-wires-holder"
  Base = -> Chamfer007038020005022011
  Edges = 2 edges r=1.25: [Edge3,Edge4]
  Placement = pos=(26.5339,-91,172.803) rot=(0,1,0;0.314159rad)
FEATURE [Part::Feature] Chamfer007038020005022012001  label="rear-platform-right-wires-holder"
  Placement = pos=(26.5339,0,172.803) rot=(0,1,0;0.314159rad)
  shape: bbox 7.251 x 19 x 6.609 mm, 14 faces (baked)
FEATURE [Part::Box] Box692  label="Cube883"
  AttacherType = Attacher::AttachEngine3D
  Height = 5
  Length = 8
  Placement = pos=(447,-25,20) rot=(0,0,1;0rad)
  Width = 34
FEATURE [Part::Cylinder] Cylinder1151  label="Cylinder1532"
  Angle = 360
  AttacherType = Attacher::AttachEngine3D
  Height = 10
  Placement = pos=(451,4,-6) rot=(0,1,0;0rad)
  Radius = 1.2
FEATURE [Part::Cylinder] Cylinder1152  label="Cylinder1533"
  Angle = 360
  AttacherType = Attacher::AttachEngine3D
  Height = 10
  Placement = pos=(451,-20,-6) rot=(0,1,0;0rad)
  Radius = 1.2
FEATURE [Part::MultiFuse] Fusion001005002004004005002010002003003003017007024041010023003003006006003006008021054006004013005009020003043002011002010006015002010005005003002003024015025  label="Fusion-0097"
  Placement = pos=(0,0,25) rot=(0,0,1;0rad)
  Refine = true
  Shapes = -> [Cylinder1151,Cylinder1152]
FEATURE [Part::Box] Box693  label="Cube884"
  AttacherType = Attacher::AttachEngine3D
  Height = 2
  Length = 8
  Placement = pos=(447,-16,23) rot=(0,0,1;0rad)
  Width = 16
FEATURE [Part::Fillet] Fillet001025008004015003
  Base = -> Box693
  Edges = 2 edges r=1.8: [Edge9,Edge11]
FEATURE [Part::Cut] Cut012035015003002009024006019011009006027002007011007005004011002017019010028046  label="Cut-0090"
  Base = -> Box692
  Refine = true
  Tool = -> Fillet001025008004015003
FEATURE [Part::Cut] Cut012035015003002009024006019011009006027002007011007005004011002017019010028047  label="Cut-0091"
  Base = -> Cut012035015003002009024006019011009006027002007011007005004011002017019010028046
  Refine = true
  Tool = -> Fusion001005002004004005002010002003003003017007024041010023003003006006003006008021054006004013005009020003043002011002010006015002010005005003002003024015025
FEATURE [Part::Chamfer] Chamfer007038020005022012002
  Base = -> Cut012035015003002009024006019011009006027002007011007005004011002017019010028047
  Edges = 2 edges r=2: [Edge28,Edge30]
FEATURE [Part::Chamfer] Chamfer007038020005022012003  label="main-frame-wires-holder"
  Base = -> Chamfer007038020005022012002
  Edges = 2 edges r=1.2: [Edge23,Edge24]
FEATURE [Part::Box] Box694  label="Cube885"
  AttacherType = Attacher::AttachEngine3D
  Height = 8
  Length = 96
  Placement = pos=(312,-32.5,16) rot=(0,0,1;0rad)
  Width = 2
FEATURE [Part::Box] Box695  label="Cube886"
  AttacherType = Attacher::AttachEngine3D
  Height = 8
  Length = 10
  Placement = pos=(398,-32.5,16) rot=(0,0,1;0rad)
  Width = 5
FEATURE [Part::MultiFuse] Fusion001005002004004005002010002003003003017007024041010023003003006006003006008021054006004013005009020003043002011002010006015002010005005003002003024015026  label="Fusion-0098"
  Refine = true
  Shapes = -> [Box669,Box695,Box694]
FEATURE [Part::Box] Box696  label="Cube887"
  AttacherType = Attacher::AttachEngine3D
  Height = 8
  Length = 10
  Placement = pos=(312,11.5,16) rot=(0,0,1;0rad)
  Width = 5
FEATURE [Part::Box] Box697  label="Cube888"
  AttacherType = Attacher::AttachEngine3D
  Height = 8
  Length = 10
  Placement = pos=(398,11.5,16) rot=(0,0,1;0rad)
  Width = 5
FEATURE [Part::Box] Box698  label="Cube889"
  AttacherType = Attacher::AttachEngine3D
  Height = 8
  Length = 96
  Placement = pos=(312,14.5,16) rot=(0,0,1;0rad)
  Width = 2
FEATURE [Part::MultiFuse] Fusion001005002004004005002010002003003003017007024041010023003003006006003006008021054006004013005009020003043002011002010006015002010005005003002003024015027  label="Fusion-0099"
  Refine = true
  Shapes = -> [Box696,Box698,Box697]
FEATURE [Part::MultiFuse] Fusion001005002004004005002010002003003003017007024041010023003003006006003006008021054006004013005009020003043002011002010006015002010005005003002003024015028  label="Fusion-0100"
  Refine = true
  Shapes = -> [Box670,Box673,Box671,Fusion001005002004004005002010002003003003017007024041010023003003006006003006008021054006004013005009020003043002011002010006015002010005005003002003024015026,Fusion001005002004004005002010002003003003017007024041010023003003006006003006008021054006004013005009020003043002011002010006015002010005005003002003024015027]
FEATURE [Part::Cut] Cut012035015003002009024006019011009006027002007011007005004011002017019010028048  label="Cut-0092"
  Base = -> Fusion001005002004004005002010002003003003017007024041010023003003006006003006008021054006004013005009020003043002011002010006015002010005005003002003024015028
  Refine = true
  Tool = -> Box672
FEATURE [Part::MultiFuse] Fusion001005002004004005002010002003003003017007024041010023003003006006003006008021054006004013005009020003043002011002010006015002010005005003002003024015029  label="Fusion-0101"
  Refine = true
  Shapes = -> [Cut012035015003002009024006019011009006027002007011007005004011002017019010028048,Chamfer007038020005022001,Chamfer007038020005022002,Chamfer007038020005022003,Chamfer007038020005022004]
FEATURE [Part::Cut] Cut012035015003002009024006019011009006027002007011007005004011002017019010028049  label="Cut-0093"
  Base = -> Fusion001005002004004005002010002003003003017007024041010023003003006006003006008021054006004013005009020003043002011002010006015002010005005003002003024015029
  Refine = true
  Tool = -> Box674
FEATURE [Part::Box] Box699  label="Cube890"
  AttacherType = Attacher::AttachEngine3D
  Height = 1
  Length = 5
  Placement = pos=(346,-18.5,15) rot=(0,0,1;0rad)
  Width = 21
FEATURE [Part::Fillet] Fillet001025008004015004
  Base = -> Cut012035015003002009024006019011009006027002007011007005004011002017019010028039
  Edges = 2 edges r=3: [Edge2,Edge13]
  Placement = pos=(10,0,0) rot=(0,0,1;0rad)
FEATURE [Part::Feature] Fillet001025008004015004001  label="Fillet001025008004015005"
  Placement = pos=(40,0,0) rot=(0,0,1;0rad)
  shape: bbox 9 x 10 x 3.5 mm, 12 faces (baked)
FEATURE [Part::Feature] Box699001  label="Cube891"
  Placement = pos=(376,-18.5,15) rot=(0,0,1;0rad)
  shape: bbox 5 x 21 x 1 mm, 6 faces (baked)
FEATURE [Part::MultiFuse] Fusion001005002004004005002010002003003003017007024041010023003003006006003006008021054006004013005009020003043002011002010006015002010005005003002003024015030  label="Fusion-0102"
  Refine = true
  Shapes = -> [Box699001,Box699]
FEATURE [Part::MultiFuse] Fusion001005002004004005002010002003003003017007024041010023003003006006003006008021054006004013005009020003043002011002010006015002010005005003002003024015031  label="Fusion-0103"
  Refine = true
  Shapes = -> [Cut012035015003002009024006019011009006027002007011007005004011002017019010028049,Fillet001025008004015004,Fillet001025008004015004001]
FEATURE [Part::Cut] Cut012035015003002009024006019011009006027002007011007005004011002017019010028050  label="Cut-0094"
  Base = -> Fusion001005002004004005002010002003003003017007024041010023003003006006003006008021054006004013005009020003043002011002010006015002010005005003002003024015031
  Refine = true
  Tool = -> Fusion001005002004004005002010002003003003017007024041010023003003006006003006008021054006004013005009020003043002011002010006015002010005005003002003024015030
FEATURE [Part::Chamfer] Chamfer007038020005022012006
  Base = -> Cut012035015003002009024006019011009006027002007011007005004011002017019010028050
  Edges = 4 edges: [Edge112 r1=6 r2=0.999,Edge118 r1=6 r2=0.999,Edge125 r1=6 r2=0.999,Edge131 r1=6 r2=0.999]
FEATURE [Part::Box] Box699002  label="Cube892"
  AttacherType = Attacher::AttachEngine3D
  Height = 18
  Length = 13
  Placement = pos=(330,-30.5,7) rot=(0,0,1;0rad)
  Width = 6.5
FEATURE [Part::Cut] Cut012035015003002009024006019011009006027002007011007005004011002017019010028051  label="circuits-holder"
  Base = -> Chamfer007038020005022012006
  Refine = true
  Tool = -> Box699002
FEATURE [App::DocumentObjectGroup] Group  label="Main Frame"
  Group = -> [Fusion,Fusion001005002004004005002010002003003003005,Cylinder967,Cylinder888,Cylinder903,Cylinder904,Cylinder905,Cylinder928,Cut012035015003002009024006019011009006027002007009,Cut012035015003002009024006019011009006027002007011,Part__Mirroring005002002002002002002002002015,Part__Mirroring005002002002002002002002002016,+12 more]
FEATURE [Part::Chamfer] Chamfer007038020005022012007
  Base = -> Cut012035015003002009024006019011009006027002007011007005004011002017019010028044
  Edges = 2 edges: [Edge9 r1=0.5 r2=1,Edge38 r1=0.5 r2=1]
FEATURE [Part::Chamfer] Chamfer007038020005022012008
  Base = -> Chamfer007038020005022012007
  Edges = 1 edges: [Edge21 r1=4 r2=7]
FEATURE [Part::Chamfer] Chamfer007038020005022012009  label="rear-stabilizer-servo-link"
  Base = -> Chamfer007038020005022012008
  Edges = 1 edges r=5.99: [Edge11]
FEATURE [App::DocumentObjectGroup] Group008  label="Rear stabilizers"
  Group = -> [Cylinder1027,Cylinder1029,Cut012035015003002009024006019011009006027002007011007005004011002005,Cut012035015003002009024006019011009006027002007011007005004011002017019010028008,Cut012035015003002009024006019011009006027002007011007005004011002017019010028035,Chamfer007038020005022012009]
